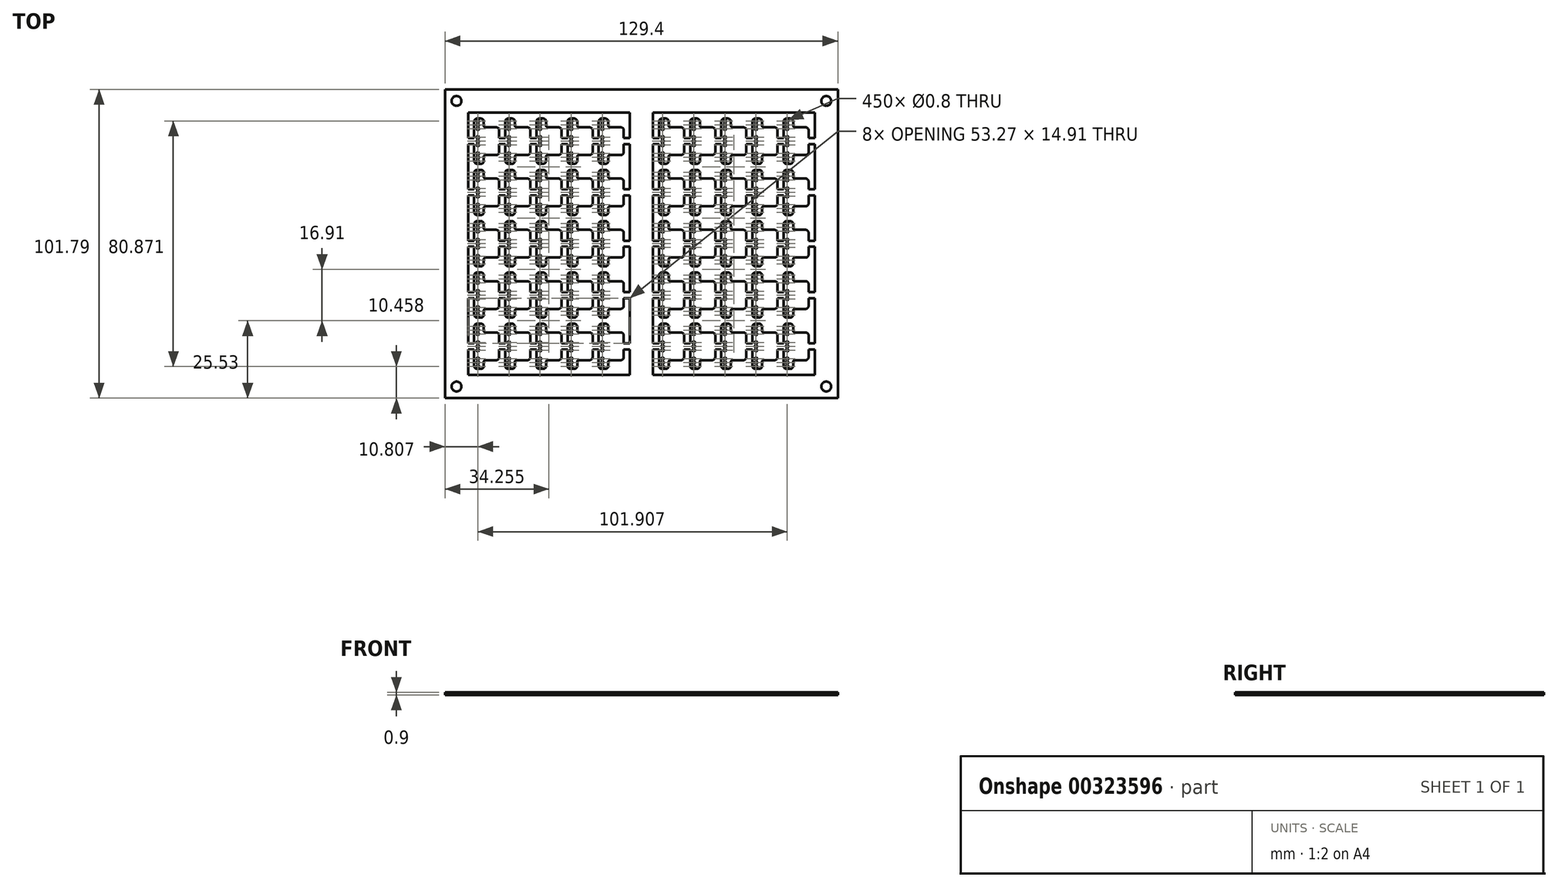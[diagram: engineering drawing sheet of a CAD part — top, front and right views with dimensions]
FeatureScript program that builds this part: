
annotation { "Feature Type Name" : "Feature", "Feature Type Description" : "" }
export const myFeature = defineFeature(function(context is Context, id is Id, definition is map)
    precondition{}
    {
        {
            var Q0;
            Q0=qCreatedBy(makeId("Top.planeOp"),FACE);
            var sketch = newSketch(context, id + "F0", { "sketchPlane" : qUnion([Q0])});
            skLineSegment(sketch, "E0.bottom", {"start": v(0, 0) * mm, "end": v(129.4, 0) * mm});
            skLineSegment(sketch, "E0.top", {"start": v(0, 101.79) * mm, "end": v(129.4, 101.79) * mm});
            skLineSegment(sketch, "E0.left", {"start": v(0, 0) * mm, "end": v(0, 101.79) * mm});
            skLineSegment(sketch, "E0.right", {"start": v(129.4, 0) * mm, "end": v(129.4, 101.79) * mm});
            skCircle(sketch, "E1", {"center": v(3.8, 3.8) * mm, "radius": 1.63 * mm});
            skCircle(sketch, "E2", {"center": v(3.8, 97.98) * mm, "radius": 1.63 * mm});
            skCircle(sketch, "E3", {"center": v(125.6, 97.98) * mm, "radius": 1.63 * mm});
            skCircle(sketch, "E4", {"center": v(125.6, 3.81) * mm, "radius": 1.63 * mm});
            skLineSegment(sketch, "E5.bottom", {"start": v(7.62, 7.62) * mm, "end": v(60.9, 7.62) * mm});
            skLineSegment(sketch, "E5.top", {"start": v(7.62, 94.17) * mm, "end": v(60.9, 94.17) * mm});
            skLineSegment(sketch, "E5.left", {"start": v(7.62, 7.62) * mm, "end": v(7.62, 94.17) * mm});
            skLineSegment(sketch, "E5.right", {"start": v(60.9, 7.62) * mm, "end": v(60.9, 94.17) * mm});
            skLineSegment(sketch, "E6.bottom", {"start": v(68.51, 7.62) * mm, "end": v(121.78, 7.62) * mm});
            skLineSegment(sketch, "E6.top", {"start": v(68.51, 94.17) * mm, "end": v(121.78, 94.17) * mm});
            skLineSegment(sketch, "E6.left", {"start": v(68.51, 7.62) * mm, "end": v(68.51, 94.17) * mm});
            skLineSegment(sketch, "E6.right", {"start": v(121.78, 7.62) * mm, "end": v(121.78, 94.17) * mm});
            skSolve(sketch);
        }
        {
            var Q0;
            Q0 = qSketchRegion(id + "F0", true);
            extrude(context, id + "F1", {"entities" : qUnion([Q0]), "depth" : .9 * mm, "offsetDistance" : 25 * mm});
        }
        {
            var Q0;
            Q0=makeQuery(id+"F1.opExtrude","CAP_FACE",FACE,{"disambiguationData":[OSD([sQuery(id+"F0.wireOp",EDGE,"E0.bottom"),sQuery(id+"F0.wireOp",EDGE,"E0.top"),sQuery(id+"F0.wireOp",EDGE,"E0.left"),sQuery(id+"F0.wireOp",EDGE,"E0.right"),sQuery(id+"F0.wireOp",EDGE,"E1"),sQuery(id+"F0.wireOp",EDGE,"E2"),sQuery(id+"F0.wireOp",EDGE,"E3"),sQuery(id+"F0.wireOp",EDGE,"E4"),sQuery(id+"F0.wireOp",EDGE,"E5.bottom"),sQuery(id+"F0.wireOp",EDGE,"E5.top"),sQuery(id+"F0.wireOp",EDGE,"E5.left"),sQuery(id+"F0.wireOp",EDGE,"E5.right"),sQuery(id+"F0.wireOp",EDGE,"E6.bottom"),sQuery(id+"F0.wireOp",EDGE,"E6.top"),sQuery(id+"F0.wireOp",EDGE,"E6.left"),sQuery(id+"F0.wireOp",EDGE,"E6.right")])],"isStart":false});
            var sketch = newSketch(context, id + "F2", { "sketchPlane" : qUnion([Q0])});
            skLineSegment(sketch, "E7.bottom", {"start": v(10.62, 24.53) * mm, "end": v(11.8, 24.53) * mm});
            skLineSegment(sketch, "E7.top", {"start": v(10.62, 9.62) * mm, "end": v(11.8, 9.62) * mm});
            skLineSegment(sketch, "E7.left", {"start": v(9.62, 23.53) * mm, "end": v(9.62, 18.07) * mm});
            skLineSegment(sketch, "E7.right", {"start": v(12.8, 23.53) * mm, "end": v(12.8, 22.15) * mm});
            skLineSegment(sketch, "E8.bottom", {"start": v(13.3, 21.65) * mm, "end": v(16.87, 21.65) * mm});
            skLineSegment(sketch, "E8.top", {"start": v(13.3, 12.5) * mm, "end": v(16.87, 12.5) * mm});
            skLineSegment(sketch, "E8.right", {"start": v(17.87, 20.65) * mm, "end": v(17.87, 13.5) * mm});
            skLineSegment(sketch, "E9.bottom", {"start": v(9.62, 18.07) * mm, "end": v(7.62, 18.07) * mm});
            skLineSegment(sketch, "E9.top", {"start": v(9.62, 16.07) * mm, "end": v(7.62, 16.07) * mm});
            skLineSegment(sketch, "E9.right", {"start": v(7.62, 18.07) * mm, "end": v(7.62, 16.07) * mm});
            skPoint(sketch, "E10.visualSharp", {"position": v(9.62, 24.53) * mm});
            skArc(sketch, "E10.filletArc", {"start": v(10.62, 24.53) * mm, "mid": v(9.91, 24.24) * mm, "end": v(9.62, 23.53) * mm});
            skPoint(sketch, "E11.visualSharp", {"position": v(12.8, 24.53) * mm});
            skArc(sketch, "E11.filletArc", {"start": v(12.8, 23.53) * mm, "mid": v(12.5, 24.24) * mm, "end": v(11.8, 24.53) * mm});
            skPoint(sketch, "E12.visualSharp", {"position": v(9.62, 9.62) * mm});
            skArc(sketch, "E12.filletArc", {"start": v(9.62, 10.62) * mm, "mid": v(9.91, 9.91) * mm, "end": v(10.62, 9.62) * mm});
            skPoint(sketch, "E13.visualSharp", {"position": v(12.8, 9.62) * mm});
            skArc(sketch, "E13.filletArc", {"start": v(11.8, 9.62) * mm, "mid": v(12.5, 9.91) * mm, "end": v(12.8, 10.62) * mm});
            skPoint(sketch, "E14.visualSharp", {"position": v(17.87, 21.65) * mm});
            skArc(sketch, "E14.filletArc", {"start": v(17.87, 20.65) * mm, "mid": v(17.58, 21.35) * mm, "end": v(16.87, 21.65) * mm});
            skPoint(sketch, "E15.visualSharp", {"position": v(17.87, 12.5) * mm});
            skArc(sketch, "E15.filletArc", {"start": v(16.87, 12.5) * mm, "mid": v(17.58, 12.8) * mm, "end": v(17.87, 13.5) * mm});
            skLineSegment(sketch, "E16.trimOffspring", {"start": v(12.8, 12) * mm, "end": v(12.8, 10.62) * mm});
            skLineSegment(sketch, "E17.trimOffspring", {"start": v(9.62, 16.07) * mm, "end": v(9.62, 10.62) * mm});
            skPoint(sketch, "E18.visualSharp", {"position": v(12.8, 21.65) * mm});
            skArc(sketch, "E18.filletArc", {"start": v(12.8, 22.15) * mm, "mid": v(12.94, 21.8) * mm, "end": v(13.3, 21.65) * mm});
            skPoint(sketch, "E19.visualSharp", {"position": v(12.8, 12.5) * mm});
            skArc(sketch, "E19.filletArc", {"start": v(13.3, 12.5) * mm, "mid": v(12.94, 12.36) * mm, "end": v(12.8, 12) * mm});
            skLineSegment(sketch, "E20.0.1.0", {"start": v(17.87, 37.56) * mm, "end": v(17.87, 30.41) * mm});
            skLineSegment(sketch, "E20.0.1.1", {"start": v(9.62, 34.98) * mm, "end": v(7.62, 34.98) * mm});
            skLineSegment(sketch, "E20.0.1.2", {"start": v(9.62, 40.44) * mm, "end": v(9.62, 34.98) * mm});
            skLineSegment(sketch, "E20.0.1.3", {"start": v(12.8, 40.44) * mm, "end": v(12.8, 39.06) * mm});
            skPoint(sketch, "E20.0.1.4", {"position": v(9.62, 26.53) * mm});
            skPoint(sketch, "E20.0.1.5", {"position": v(12.8, 29.41) * mm});
            skLineSegment(sketch, "E20.0.1.6", {"start": v(13.3, 38.56) * mm, "end": v(16.87, 38.56) * mm});
            skLineSegment(sketch, "E20.0.1.7", {"start": v(12.8, 28.91) * mm, "end": v(12.8, 27.53) * mm});
            skPoint(sketch, "E20.0.1.8", {"position": v(12.8, 41.44) * mm});
            skLineSegment(sketch, "E20.0.1.9", {"start": v(9.62, 32.98) * mm, "end": v(9.62, 27.53) * mm});
            skLineSegment(sketch, "E20.0.1.10", {"start": v(10.62, 41.44) * mm, "end": v(11.8, 41.44) * mm});
            skLineSegment(sketch, "E20.0.1.11", {"start": v(10.62, 26.53) * mm, "end": v(11.8, 26.53) * mm});
            skLineSegment(sketch, "E20.0.1.12", {"start": v(7.62, 34.98) * mm, "end": v(7.62, 32.98) * mm});
            skLineSegment(sketch, "E20.0.1.13", {"start": v(9.62, 32.98) * mm, "end": v(7.62, 32.98) * mm});
            skLineSegment(sketch, "E20.0.1.14", {"start": v(13.3, 29.41) * mm, "end": v(16.87, 29.41) * mm});
            skPoint(sketch, "E20.0.1.15", {"position": v(12.8, 38.56) * mm});
            skPoint(sketch, "E20.0.1.16", {"position": v(12.8, 26.53) * mm});
            skPoint(sketch, "E20.0.1.17", {"position": v(9.62, 41.44) * mm});
            skPoint(sketch, "E20.0.1.18", {"position": v(17.87, 38.56) * mm});
            skPoint(sketch, "E20.0.1.19", {"position": v(17.87, 29.41) * mm});
            skArc(sketch, "E20.0.1.20", {"start": v(10.62, 41.44) * mm, "mid": v(9.91, 41.15) * mm, "end": v(9.62, 40.44) * mm});
            skArc(sketch, "E20.0.1.21", {"start": v(17.87, 37.56) * mm, "mid": v(17.58, 38.26) * mm, "end": v(16.87, 38.56) * mm});
            skArc(sketch, "E20.0.1.22", {"start": v(12.8, 40.44) * mm, "mid": v(12.5, 41.15) * mm, "end": v(11.8, 41.44) * mm});
            skArc(sketch, "E20.0.1.23", {"start": v(9.62, 27.53) * mm, "mid": v(9.91, 26.82) * mm, "end": v(10.62, 26.53) * mm});
            skArc(sketch, "E20.0.1.24", {"start": v(11.8, 26.53) * mm, "mid": v(12.5, 26.82) * mm, "end": v(12.8, 27.53) * mm});
            skArc(sketch, "E20.0.1.25", {"start": v(16.87, 29.41) * mm, "mid": v(17.58, 29.7) * mm, "end": v(17.87, 30.41) * mm});
            skArc(sketch, "E20.0.1.26", {"start": v(13.3, 29.41) * mm, "mid": v(12.94, 29.27) * mm, "end": v(12.8, 28.91) * mm});
            skArc(sketch, "E20.0.1.27", {"start": v(12.8, 39.06) * mm, "mid": v(12.94, 38.7) * mm, "end": v(13.3, 38.56) * mm});
            skLineSegment(sketch, "E20.0.2.0", {"start": v(17.87, 54.47) * mm, "end": v(17.87, 47.32) * mm});
            skLineSegment(sketch, "E20.0.2.1", {"start": v(9.62, 51.9) * mm, "end": v(7.62, 51.9) * mm});
            skLineSegment(sketch, "E20.0.2.2", {"start": v(9.62, 57.35) * mm, "end": v(9.62, 51.9) * mm});
            skLineSegment(sketch, "E20.0.2.3", {"start": v(12.8, 57.35) * mm, "end": v(12.8, 55.97) * mm});
            skPoint(sketch, "E20.0.2.4", {"position": v(9.62, 43.44) * mm});
            skPoint(sketch, "E20.0.2.5", {"position": v(12.8, 46.32) * mm});
            skLineSegment(sketch, "E20.0.2.6", {"start": v(13.3, 55.47) * mm, "end": v(16.87, 55.47) * mm});
            skLineSegment(sketch, "E20.0.2.7", {"start": v(12.8, 45.82) * mm, "end": v(12.8, 44.44) * mm});
            skPoint(sketch, "E20.0.2.8", {"position": v(12.8, 58.35) * mm});
            skLineSegment(sketch, "E20.0.2.9", {"start": v(9.62, 49.9) * mm, "end": v(9.62, 44.44) * mm});
            skLineSegment(sketch, "E20.0.2.10", {"start": v(10.62, 58.35) * mm, "end": v(11.8, 58.35) * mm});
            skLineSegment(sketch, "E20.0.2.11", {"start": v(10.62, 43.44) * mm, "end": v(11.8, 43.44) * mm});
            skLineSegment(sketch, "E20.0.2.12", {"start": v(7.62, 51.9) * mm, "end": v(7.62, 49.9) * mm});
            skLineSegment(sketch, "E20.0.2.13", {"start": v(9.62, 49.9) * mm, "end": v(7.62, 49.9) * mm});
            skLineSegment(sketch, "E20.0.2.14", {"start": v(13.3, 46.32) * mm, "end": v(16.87, 46.32) * mm});
            skPoint(sketch, "E20.0.2.15", {"position": v(12.8, 55.47) * mm});
            skPoint(sketch, "E20.0.2.16", {"position": v(12.8, 43.44) * mm});
            skPoint(sketch, "E20.0.2.17", {"position": v(9.62, 58.35) * mm});
            skPoint(sketch, "E20.0.2.18", {"position": v(17.87, 55.47) * mm});
            skPoint(sketch, "E20.0.2.19", {"position": v(17.87, 46.32) * mm});
            skArc(sketch, "E20.0.2.20", {"start": v(10.62, 58.35) * mm, "mid": v(9.91, 58.06) * mm, "end": v(9.62, 57.35) * mm});
            skArc(sketch, "E20.0.2.21", {"start": v(17.87, 54.47) * mm, "mid": v(17.58, 55.17) * mm, "end": v(16.87, 55.47) * mm});
            skArc(sketch, "E20.0.2.22", {"start": v(12.8, 57.35) * mm, "mid": v(12.5, 58.06) * mm, "end": v(11.8, 58.35) * mm});
            skArc(sketch, "E20.0.2.23", {"start": v(9.62, 44.44) * mm, "mid": v(9.91, 43.73) * mm, "end": v(10.62, 43.44) * mm});
            skArc(sketch, "E20.0.2.24", {"start": v(11.8, 43.44) * mm, "mid": v(12.5, 43.73) * mm, "end": v(12.8, 44.44) * mm});
            skArc(sketch, "E20.0.2.25", {"start": v(16.87, 46.32) * mm, "mid": v(17.58, 46.62) * mm, "end": v(17.87, 47.32) * mm});
            skArc(sketch, "E20.0.2.26", {"start": v(13.3, 46.32) * mm, "mid": v(12.94, 46.18) * mm, "end": v(12.8, 45.82) * mm});
            skArc(sketch, "E20.0.2.27", {"start": v(12.8, 55.97) * mm, "mid": v(12.94, 55.61) * mm, "end": v(13.3, 55.47) * mm});
            skLineSegment(sketch, "E20.0.3.0", {"start": v(17.87, 71.38) * mm, "end": v(17.87, 64.23) * mm});
            skLineSegment(sketch, "E20.0.3.1", {"start": v(9.62, 68.8) * mm, "end": v(7.62, 68.8) * mm});
            skLineSegment(sketch, "E20.0.3.2", {"start": v(9.62, 74.26) * mm, "end": v(9.62, 68.8) * mm});
            skLineSegment(sketch, "E20.0.3.3", {"start": v(12.8, 74.26) * mm, "end": v(12.8, 72.88) * mm});
            skPoint(sketch, "E20.0.3.4", {"position": v(9.62, 60.35) * mm});
            skPoint(sketch, "E20.0.3.5", {"position": v(12.8, 63.23) * mm});
            skLineSegment(sketch, "E20.0.3.6", {"start": v(13.3, 72.38) * mm, "end": v(16.87, 72.38) * mm});
            skLineSegment(sketch, "E20.0.3.7", {"start": v(12.8, 62.73) * mm, "end": v(12.8, 61.35) * mm});
            skPoint(sketch, "E20.0.3.8", {"position": v(12.8, 75.26) * mm});
            skLineSegment(sketch, "E20.0.3.9", {"start": v(9.62, 66.8) * mm, "end": v(9.62, 61.35) * mm});
            skLineSegment(sketch, "E20.0.3.10", {"start": v(10.62, 75.26) * mm, "end": v(11.8, 75.26) * mm});
            skLineSegment(sketch, "E20.0.3.11", {"start": v(10.62, 60.35) * mm, "end": v(11.8, 60.35) * mm});
            skLineSegment(sketch, "E20.0.3.12", {"start": v(7.62, 68.8) * mm, "end": v(7.62, 66.8) * mm});
            skLineSegment(sketch, "E20.0.3.13", {"start": v(9.62, 66.8) * mm, "end": v(7.62, 66.8) * mm});
            skLineSegment(sketch, "E20.0.3.14", {"start": v(13.3, 63.23) * mm, "end": v(16.87, 63.23) * mm});
            skPoint(sketch, "E20.0.3.15", {"position": v(12.8, 72.38) * mm});
            skPoint(sketch, "E20.0.3.16", {"position": v(12.8, 60.35) * mm});
            skPoint(sketch, "E20.0.3.17", {"position": v(9.62, 75.26) * mm});
            skPoint(sketch, "E20.0.3.18", {"position": v(17.87, 72.38) * mm});
            skPoint(sketch, "E20.0.3.19", {"position": v(17.87, 63.23) * mm});
            skArc(sketch, "E20.0.3.20", {"start": v(10.62, 75.26) * mm, "mid": v(9.91, 74.97) * mm, "end": v(9.62, 74.26) * mm});
            skArc(sketch, "E20.0.3.21", {"start": v(17.87, 71.38) * mm, "mid": v(17.58, 72.08) * mm, "end": v(16.87, 72.38) * mm});
            skArc(sketch, "E20.0.3.22", {"start": v(12.8, 74.26) * mm, "mid": v(12.5, 74.97) * mm, "end": v(11.8, 75.26) * mm});
            skArc(sketch, "E20.0.3.23", {"start": v(9.62, 61.35) * mm, "mid": v(9.91, 60.64) * mm, "end": v(10.62, 60.35) * mm});
            skArc(sketch, "E20.0.3.24", {"start": v(11.8, 60.35) * mm, "mid": v(12.5, 60.64) * mm, "end": v(12.8, 61.35) * mm});
            skArc(sketch, "E20.0.3.25", {"start": v(16.87, 63.23) * mm, "mid": v(17.58, 63.53) * mm, "end": v(17.87, 64.23) * mm});
            skArc(sketch, "E20.0.3.26", {"start": v(13.3, 63.23) * mm, "mid": v(12.94, 63.09) * mm, "end": v(12.8, 62.73) * mm});
            skArc(sketch, "E20.0.3.27", {"start": v(12.8, 72.88) * mm, "mid": v(12.94, 72.52) * mm, "end": v(13.3, 72.38) * mm});
            skLineSegment(sketch, "E20.0.4.0", {"start": v(17.87, 88.29) * mm, "end": v(17.87, 81.14) * mm});
            skLineSegment(sketch, "E20.0.4.1", {"start": v(9.62, 85.71) * mm, "end": v(7.62, 85.71) * mm});
            skLineSegment(sketch, "E20.0.4.2", {"start": v(9.62, 91.17) * mm, "end": v(9.62, 85.71) * mm});
            skLineSegment(sketch, "E20.0.4.3", {"start": v(12.8, 91.17) * mm, "end": v(12.8, 89.79) * mm});
            skPoint(sketch, "E20.0.4.4", {"position": v(9.62, 77.26) * mm});
            skPoint(sketch, "E20.0.4.5", {"position": v(12.8, 80.14) * mm});
            skLineSegment(sketch, "E20.0.4.6", {"start": v(13.3, 89.29) * mm, "end": v(16.87, 89.29) * mm});
            skLineSegment(sketch, "E20.0.4.7", {"start": v(12.8, 79.64) * mm, "end": v(12.8, 78.26) * mm});
            skPoint(sketch, "E20.0.4.8", {"position": v(12.8, 92.17) * mm});
            skLineSegment(sketch, "E20.0.4.9", {"start": v(9.62, 83.71) * mm, "end": v(9.62, 78.26) * mm});
            skLineSegment(sketch, "E20.0.4.10", {"start": v(10.62, 92.17) * mm, "end": v(11.8, 92.17) * mm});
            skLineSegment(sketch, "E20.0.4.11", {"start": v(10.62, 77.26) * mm, "end": v(11.8, 77.26) * mm});
            skLineSegment(sketch, "E20.0.4.12", {"start": v(7.62, 85.71) * mm, "end": v(7.62, 83.71) * mm});
            skLineSegment(sketch, "E20.0.4.13", {"start": v(9.62, 83.71) * mm, "end": v(7.62, 83.71) * mm});
            skLineSegment(sketch, "E20.0.4.14", {"start": v(13.3, 80.14) * mm, "end": v(16.87, 80.14) * mm});
            skPoint(sketch, "E20.0.4.15", {"position": v(12.8, 89.29) * mm});
            skPoint(sketch, "E20.0.4.16", {"position": v(12.8, 77.26) * mm});
            skPoint(sketch, "E20.0.4.17", {"position": v(9.62, 92.17) * mm});
            skPoint(sketch, "E20.0.4.18", {"position": v(17.87, 89.29) * mm});
            skPoint(sketch, "E20.0.4.19", {"position": v(17.87, 80.14) * mm});
            skArc(sketch, "E20.0.4.20", {"start": v(10.62, 92.17) * mm, "mid": v(9.91, 91.88) * mm, "end": v(9.62, 91.17) * mm});
            skArc(sketch, "E20.0.4.21", {"start": v(17.87, 88.29) * mm, "mid": v(17.58, 89) * mm, "end": v(16.87, 89.29) * mm});
            skArc(sketch, "E20.0.4.22", {"start": v(12.8, 91.17) * mm, "mid": v(12.5, 91.88) * mm, "end": v(11.8, 92.17) * mm});
            skArc(sketch, "E20.0.4.23", {"start": v(9.62, 78.26) * mm, "mid": v(9.91, 77.55) * mm, "end": v(10.62, 77.26) * mm});
            skArc(sketch, "E20.0.4.24", {"start": v(11.8, 77.26) * mm, "mid": v(12.5, 77.55) * mm, "end": v(12.8, 78.26) * mm});
            skArc(sketch, "E20.0.4.25", {"start": v(16.87, 80.14) * mm, "mid": v(17.58, 80.44) * mm, "end": v(17.87, 81.14) * mm});
            skArc(sketch, "E20.0.4.26", {"start": v(13.3, 80.14) * mm, "mid": v(12.94, 80) * mm, "end": v(12.8, 79.64) * mm});
            skArc(sketch, "E20.0.4.27", {"start": v(12.8, 89.79) * mm, "mid": v(12.94, 89.43) * mm, "end": v(13.3, 89.29) * mm});
            skLineSegment(sketch, "E20.1.0.0", {"start": v(28.13, 20.65) * mm, "end": v(28.13, 13.5) * mm});
            skLineSegment(sketch, "E20.1.0.1", {"start": v(19.87, 18.07) * mm, "end": v(17.87, 18.07) * mm});
            skLineSegment(sketch, "E20.1.0.2", {"start": v(19.87, 23.53) * mm, "end": v(19.87, 18.07) * mm});
            skLineSegment(sketch, "E20.1.0.3", {"start": v(23.05, 23.53) * mm, "end": v(23.05, 22.15) * mm});
            skPoint(sketch, "E20.1.0.4", {"position": v(19.87, 9.62) * mm});
            skPoint(sketch, "E20.1.0.5", {"position": v(23.05, 12.5) * mm});
            skLineSegment(sketch, "E20.1.0.6", {"start": v(23.55, 21.65) * mm, "end": v(27.13, 21.65) * mm});
            skLineSegment(sketch, "E20.1.0.7", {"start": v(23.05, 12) * mm, "end": v(23.05, 10.62) * mm});
            skPoint(sketch, "E20.1.0.8", {"position": v(23.05, 24.53) * mm});
            skLineSegment(sketch, "E20.1.0.9", {"start": v(19.87, 16.07) * mm, "end": v(19.87, 10.62) * mm});
            skLineSegment(sketch, "E20.1.0.10", {"start": v(20.87, 24.53) * mm, "end": v(22.05, 24.53) * mm});
            skLineSegment(sketch, "E20.1.0.11", {"start": v(20.87, 9.62) * mm, "end": v(22.05, 9.62) * mm});
            skLineSegment(sketch, "E20.1.0.12", {"start": v(17.87, 18.07) * mm, "end": v(17.87, 16.07) * mm});
            skLineSegment(sketch, "E20.1.0.13", {"start": v(19.87, 16.07) * mm, "end": v(17.87, 16.07) * mm});
            skLineSegment(sketch, "E20.1.0.14", {"start": v(23.55, 12.5) * mm, "end": v(27.13, 12.5) * mm});
            skPoint(sketch, "E20.1.0.15", {"position": v(23.05, 21.65) * mm});
            skPoint(sketch, "E20.1.0.16", {"position": v(23.05, 9.62) * mm});
            skPoint(sketch, "E20.1.0.17", {"position": v(19.87, 24.53) * mm});
            skPoint(sketch, "E20.1.0.18", {"position": v(28.13, 21.65) * mm});
            skPoint(sketch, "E20.1.0.19", {"position": v(28.13, 12.5) * mm});
            skArc(sketch, "E20.1.0.20", {"start": v(20.87, 24.53) * mm, "mid": v(20.17, 24.24) * mm, "end": v(19.87, 23.53) * mm});
            skArc(sketch, "E20.1.0.21", {"start": v(28.13, 20.65) * mm, "mid": v(27.84, 21.35) * mm, "end": v(27.13, 21.65) * mm});
            skArc(sketch, "E20.1.0.22", {"start": v(23.05, 23.53) * mm, "mid": v(22.76, 24.24) * mm, "end": v(22.05, 24.53) * mm});
            skArc(sketch, "E20.1.0.23", {"start": v(19.87, 10.62) * mm, "mid": v(20.17, 9.91) * mm, "end": v(20.87, 9.62) * mm});
            skArc(sketch, "E20.1.0.24", {"start": v(22.05, 9.62) * mm, "mid": v(22.76, 9.91) * mm, "end": v(23.05, 10.62) * mm});
            skArc(sketch, "E20.1.0.25", {"start": v(27.13, 12.5) * mm, "mid": v(27.84, 12.8) * mm, "end": v(28.13, 13.5) * mm});
            skArc(sketch, "E20.1.0.26", {"start": v(23.55, 12.5) * mm, "mid": v(23.2, 12.36) * mm, "end": v(23.05, 12) * mm});
            skArc(sketch, "E20.1.0.27", {"start": v(23.05, 22.15) * mm, "mid": v(23.2, 21.8) * mm, "end": v(23.55, 21.65) * mm});
            skLineSegment(sketch, "E20.1.1.0", {"start": v(28.13, 37.56) * mm, "end": v(28.13, 30.41) * mm});
            skLineSegment(sketch, "E20.1.1.1", {"start": v(19.87, 34.98) * mm, "end": v(17.87, 34.98) * mm});
            skLineSegment(sketch, "E20.1.1.2", {"start": v(19.87, 40.44) * mm, "end": v(19.87, 34.98) * mm});
            skLineSegment(sketch, "E20.1.1.3", {"start": v(23.05, 40.44) * mm, "end": v(23.05, 39.06) * mm});
            skPoint(sketch, "E20.1.1.4", {"position": v(19.87, 26.53) * mm});
            skPoint(sketch, "E20.1.1.5", {"position": v(23.05, 29.41) * mm});
            skLineSegment(sketch, "E20.1.1.6", {"start": v(23.55, 38.56) * mm, "end": v(27.13, 38.56) * mm});
            skLineSegment(sketch, "E20.1.1.7", {"start": v(23.05, 28.91) * mm, "end": v(23.05, 27.53) * mm});
            skPoint(sketch, "E20.1.1.8", {"position": v(23.05, 41.44) * mm});
            skLineSegment(sketch, "E20.1.1.9", {"start": v(19.87, 32.98) * mm, "end": v(19.87, 27.53) * mm});
            skLineSegment(sketch, "E20.1.1.10", {"start": v(20.87, 41.44) * mm, "end": v(22.05, 41.44) * mm});
            skLineSegment(sketch, "E20.1.1.11", {"start": v(20.87, 26.53) * mm, "end": v(22.05, 26.53) * mm});
            skLineSegment(sketch, "E20.1.1.12", {"start": v(17.87, 34.98) * mm, "end": v(17.87, 32.98) * mm});
            skLineSegment(sketch, "E20.1.1.13", {"start": v(19.87, 32.98) * mm, "end": v(17.87, 32.98) * mm});
            skLineSegment(sketch, "E20.1.1.14", {"start": v(23.55, 29.41) * mm, "end": v(27.13, 29.41) * mm});
            skPoint(sketch, "E20.1.1.15", {"position": v(23.05, 38.56) * mm});
            skPoint(sketch, "E20.1.1.16", {"position": v(23.05, 26.53) * mm});
            skPoint(sketch, "E20.1.1.17", {"position": v(19.87, 41.44) * mm});
            skPoint(sketch, "E20.1.1.18", {"position": v(28.13, 38.56) * mm});
            skPoint(sketch, "E20.1.1.19", {"position": v(28.13, 29.41) * mm});
            skArc(sketch, "E20.1.1.20", {"start": v(20.87, 41.44) * mm, "mid": v(20.17, 41.15) * mm, "end": v(19.87, 40.44) * mm});
            skArc(sketch, "E20.1.1.21", {"start": v(28.13, 37.56) * mm, "mid": v(27.84, 38.26) * mm, "end": v(27.13, 38.56) * mm});
            skArc(sketch, "E20.1.1.22", {"start": v(23.05, 40.44) * mm, "mid": v(22.76, 41.15) * mm, "end": v(22.05, 41.44) * mm});
            skArc(sketch, "E20.1.1.23", {"start": v(19.87, 27.53) * mm, "mid": v(20.17, 26.82) * mm, "end": v(20.87, 26.53) * mm});
            skArc(sketch, "E20.1.1.24", {"start": v(22.05, 26.53) * mm, "mid": v(22.76, 26.82) * mm, "end": v(23.05, 27.53) * mm});
            skArc(sketch, "E20.1.1.25", {"start": v(27.13, 29.41) * mm, "mid": v(27.84, 29.7) * mm, "end": v(28.13, 30.41) * mm});
            skArc(sketch, "E20.1.1.26", {"start": v(23.55, 29.41) * mm, "mid": v(23.2, 29.27) * mm, "end": v(23.05, 28.91) * mm});
            skArc(sketch, "E20.1.1.27", {"start": v(23.05, 39.06) * mm, "mid": v(23.2, 38.7) * mm, "end": v(23.55, 38.56) * mm});
            skLineSegment(sketch, "E20.1.2.0", {"start": v(28.13, 54.47) * mm, "end": v(28.13, 47.32) * mm});
            skLineSegment(sketch, "E20.1.2.1", {"start": v(19.87, 51.9) * mm, "end": v(17.87, 51.9) * mm});
            skLineSegment(sketch, "E20.1.2.2", {"start": v(19.87, 57.35) * mm, "end": v(19.87, 51.9) * mm});
            skLineSegment(sketch, "E20.1.2.3", {"start": v(23.05, 57.35) * mm, "end": v(23.05, 55.97) * mm});
            skPoint(sketch, "E20.1.2.4", {"position": v(19.87, 43.44) * mm});
            skPoint(sketch, "E20.1.2.5", {"position": v(23.05, 46.32) * mm});
            skLineSegment(sketch, "E20.1.2.6", {"start": v(23.55, 55.47) * mm, "end": v(27.13, 55.47) * mm});
            skLineSegment(sketch, "E20.1.2.7", {"start": v(23.05, 45.82) * mm, "end": v(23.05, 44.44) * mm});
            skPoint(sketch, "E20.1.2.8", {"position": v(23.05, 58.35) * mm});
            skLineSegment(sketch, "E20.1.2.9", {"start": v(19.87, 49.9) * mm, "end": v(19.87, 44.44) * mm});
            skLineSegment(sketch, "E20.1.2.10", {"start": v(20.87, 58.35) * mm, "end": v(22.05, 58.35) * mm});
            skLineSegment(sketch, "E20.1.2.11", {"start": v(20.87, 43.44) * mm, "end": v(22.05, 43.44) * mm});
            skLineSegment(sketch, "E20.1.2.12", {"start": v(17.87, 51.9) * mm, "end": v(17.87, 49.9) * mm});
            skLineSegment(sketch, "E20.1.2.13", {"start": v(19.87, 49.9) * mm, "end": v(17.87, 49.9) * mm});
            skLineSegment(sketch, "E20.1.2.14", {"start": v(23.55, 46.32) * mm, "end": v(27.13, 46.32) * mm});
            skPoint(sketch, "E20.1.2.15", {"position": v(23.05, 55.47) * mm});
            skPoint(sketch, "E20.1.2.16", {"position": v(23.05, 43.44) * mm});
            skPoint(sketch, "E20.1.2.17", {"position": v(19.87, 58.35) * mm});
            skPoint(sketch, "E20.1.2.18", {"position": v(28.13, 55.47) * mm});
            skPoint(sketch, "E20.1.2.19", {"position": v(28.13, 46.32) * mm});
            skArc(sketch, "E20.1.2.20", {"start": v(20.87, 58.35) * mm, "mid": v(20.17, 58.06) * mm, "end": v(19.87, 57.35) * mm});
            skArc(sketch, "E20.1.2.21", {"start": v(28.13, 54.47) * mm, "mid": v(27.84, 55.17) * mm, "end": v(27.13, 55.47) * mm});
            skArc(sketch, "E20.1.2.22", {"start": v(23.05, 57.35) * mm, "mid": v(22.76, 58.06) * mm, "end": v(22.05, 58.35) * mm});
            skArc(sketch, "E20.1.2.23", {"start": v(19.87, 44.44) * mm, "mid": v(20.17, 43.73) * mm, "end": v(20.87, 43.44) * mm});
            skArc(sketch, "E20.1.2.24", {"start": v(22.05, 43.44) * mm, "mid": v(22.76, 43.73) * mm, "end": v(23.05, 44.44) * mm});
            skArc(sketch, "E20.1.2.25", {"start": v(27.13, 46.32) * mm, "mid": v(27.84, 46.62) * mm, "end": v(28.13, 47.32) * mm});
            skArc(sketch, "E20.1.2.26", {"start": v(23.55, 46.32) * mm, "mid": v(23.2, 46.18) * mm, "end": v(23.05, 45.82) * mm});
            skArc(sketch, "E20.1.2.27", {"start": v(23.05, 55.97) * mm, "mid": v(23.2, 55.61) * mm, "end": v(23.55, 55.47) * mm});
            skLineSegment(sketch, "E20.1.3.0", {"start": v(28.13, 71.38) * mm, "end": v(28.13, 64.23) * mm});
            skLineSegment(sketch, "E20.1.3.1", {"start": v(19.87, 68.8) * mm, "end": v(17.87, 68.8) * mm});
            skLineSegment(sketch, "E20.1.3.2", {"start": v(19.87, 74.26) * mm, "end": v(19.87, 68.8) * mm});
            skLineSegment(sketch, "E20.1.3.3", {"start": v(23.05, 74.26) * mm, "end": v(23.05, 72.88) * mm});
            skPoint(sketch, "E20.1.3.4", {"position": v(19.87, 60.35) * mm});
            skPoint(sketch, "E20.1.3.5", {"position": v(23.05, 63.23) * mm});
            skLineSegment(sketch, "E20.1.3.6", {"start": v(23.55, 72.38) * mm, "end": v(27.13, 72.38) * mm});
            skLineSegment(sketch, "E20.1.3.7", {"start": v(23.05, 62.73) * mm, "end": v(23.05, 61.35) * mm});
            skPoint(sketch, "E20.1.3.8", {"position": v(23.05, 75.26) * mm});
            skLineSegment(sketch, "E20.1.3.9", {"start": v(19.87, 66.8) * mm, "end": v(19.87, 61.35) * mm});
            skLineSegment(sketch, "E20.1.3.10", {"start": v(20.87, 75.26) * mm, "end": v(22.05, 75.26) * mm});
            skLineSegment(sketch, "E20.1.3.11", {"start": v(20.87, 60.35) * mm, "end": v(22.05, 60.35) * mm});
            skLineSegment(sketch, "E20.1.3.12", {"start": v(17.87, 68.8) * mm, "end": v(17.87, 66.8) * mm});
            skLineSegment(sketch, "E20.1.3.13", {"start": v(19.87, 66.8) * mm, "end": v(17.87, 66.8) * mm});
            skLineSegment(sketch, "E20.1.3.14", {"start": v(23.55, 63.23) * mm, "end": v(27.13, 63.23) * mm});
            skPoint(sketch, "E20.1.3.15", {"position": v(23.05, 72.38) * mm});
            skPoint(sketch, "E20.1.3.16", {"position": v(23.05, 60.35) * mm});
            skPoint(sketch, "E20.1.3.17", {"position": v(19.87, 75.26) * mm});
            skPoint(sketch, "E20.1.3.18", {"position": v(28.13, 72.38) * mm});
            skPoint(sketch, "E20.1.3.19", {"position": v(28.13, 63.23) * mm});
            skArc(sketch, "E20.1.3.20", {"start": v(20.87, 75.26) * mm, "mid": v(20.17, 74.97) * mm, "end": v(19.87, 74.26) * mm});
            skArc(sketch, "E20.1.3.21", {"start": v(28.13, 71.38) * mm, "mid": v(27.84, 72.08) * mm, "end": v(27.13, 72.38) * mm});
            skArc(sketch, "E20.1.3.22", {"start": v(23.05, 74.26) * mm, "mid": v(22.76, 74.97) * mm, "end": v(22.05, 75.26) * mm});
            skArc(sketch, "E20.1.3.23", {"start": v(19.87, 61.35) * mm, "mid": v(20.17, 60.64) * mm, "end": v(20.87, 60.35) * mm});
            skArc(sketch, "E20.1.3.24", {"start": v(22.05, 60.35) * mm, "mid": v(22.76, 60.64) * mm, "end": v(23.05, 61.35) * mm});
            skArc(sketch, "E20.1.3.25", {"start": v(27.13, 63.23) * mm, "mid": v(27.84, 63.53) * mm, "end": v(28.13, 64.23) * mm});
            skArc(sketch, "E20.1.3.26", {"start": v(23.55, 63.23) * mm, "mid": v(23.2, 63.09) * mm, "end": v(23.05, 62.73) * mm});
            skArc(sketch, "E20.1.3.27", {"start": v(23.05, 72.88) * mm, "mid": v(23.2, 72.52) * mm, "end": v(23.55, 72.38) * mm});
            skLineSegment(sketch, "E20.1.4.0", {"start": v(28.13, 88.29) * mm, "end": v(28.13, 81.14) * mm});
            skLineSegment(sketch, "E20.1.4.1", {"start": v(19.87, 85.71) * mm, "end": v(17.87, 85.71) * mm});
            skLineSegment(sketch, "E20.1.4.2", {"start": v(19.87, 91.17) * mm, "end": v(19.87, 85.71) * mm});
            skLineSegment(sketch, "E20.1.4.3", {"start": v(23.05, 91.17) * mm, "end": v(23.05, 89.79) * mm});
            skPoint(sketch, "E20.1.4.4", {"position": v(19.87, 77.26) * mm});
            skPoint(sketch, "E20.1.4.5", {"position": v(23.05, 80.14) * mm});
            skLineSegment(sketch, "E20.1.4.6", {"start": v(23.55, 89.29) * mm, "end": v(27.13, 89.29) * mm});
            skLineSegment(sketch, "E20.1.4.7", {"start": v(23.05, 79.64) * mm, "end": v(23.05, 78.26) * mm});
            skPoint(sketch, "E20.1.4.8", {"position": v(23.05, 92.17) * mm});
            skLineSegment(sketch, "E20.1.4.9", {"start": v(19.87, 83.71) * mm, "end": v(19.87, 78.26) * mm});
            skLineSegment(sketch, "E20.1.4.10", {"start": v(20.87, 92.17) * mm, "end": v(22.05, 92.17) * mm});
            skLineSegment(sketch, "E20.1.4.11", {"start": v(20.87, 77.26) * mm, "end": v(22.05, 77.26) * mm});
            skLineSegment(sketch, "E20.1.4.12", {"start": v(17.87, 85.71) * mm, "end": v(17.87, 83.71) * mm});
            skLineSegment(sketch, "E20.1.4.13", {"start": v(19.87, 83.71) * mm, "end": v(17.87, 83.71) * mm});
            skLineSegment(sketch, "E20.1.4.14", {"start": v(23.55, 80.14) * mm, "end": v(27.13, 80.14) * mm});
            skPoint(sketch, "E20.1.4.15", {"position": v(23.05, 89.29) * mm});
            skPoint(sketch, "E20.1.4.16", {"position": v(23.05, 77.26) * mm});
            skPoint(sketch, "E20.1.4.17", {"position": v(19.87, 92.17) * mm});
            skPoint(sketch, "E20.1.4.18", {"position": v(28.13, 89.29) * mm});
            skPoint(sketch, "E20.1.4.19", {"position": v(28.13, 80.14) * mm});
            skArc(sketch, "E20.1.4.20", {"start": v(20.87, 92.17) * mm, "mid": v(20.17, 91.88) * mm, "end": v(19.87, 91.17) * mm});
            skArc(sketch, "E20.1.4.21", {"start": v(28.13, 88.29) * mm, "mid": v(27.84, 89) * mm, "end": v(27.13, 89.29) * mm});
            skArc(sketch, "E20.1.4.22", {"start": v(23.05, 91.17) * mm, "mid": v(22.76, 91.88) * mm, "end": v(22.05, 92.17) * mm});
            skArc(sketch, "E20.1.4.23", {"start": v(19.87, 78.26) * mm, "mid": v(20.17, 77.55) * mm, "end": v(20.87, 77.26) * mm});
            skArc(sketch, "E20.1.4.24", {"start": v(22.05, 77.26) * mm, "mid": v(22.76, 77.55) * mm, "end": v(23.05, 78.26) * mm});
            skArc(sketch, "E20.1.4.25", {"start": v(27.13, 80.14) * mm, "mid": v(27.84, 80.44) * mm, "end": v(28.13, 81.14) * mm});
            skArc(sketch, "E20.1.4.26", {"start": v(23.55, 80.14) * mm, "mid": v(23.2, 80) * mm, "end": v(23.05, 79.64) * mm});
            skArc(sketch, "E20.1.4.27", {"start": v(23.05, 89.79) * mm, "mid": v(23.2, 89.43) * mm, "end": v(23.55, 89.29) * mm});
            skLineSegment(sketch, "E20.2.0.0", {"start": v(38.38, 20.65) * mm, "end": v(38.38, 13.5) * mm});
            skLineSegment(sketch, "E20.2.0.1", {"start": v(30.13, 18.07) * mm, "end": v(28.13, 18.07) * mm});
            skLineSegment(sketch, "E20.2.0.2", {"start": v(30.13, 23.53) * mm, "end": v(30.13, 18.07) * mm});
            skLineSegment(sketch, "E20.2.0.3", {"start": v(33.3, 23.53) * mm, "end": v(33.3, 22.15) * mm});
            skPoint(sketch, "E20.2.0.4", {"position": v(30.13, 9.62) * mm});
            skPoint(sketch, "E20.2.0.5", {"position": v(33.3, 12.5) * mm});
            skLineSegment(sketch, "E20.2.0.6", {"start": v(33.8, 21.65) * mm, "end": v(37.38, 21.65) * mm});
            skLineSegment(sketch, "E20.2.0.7", {"start": v(33.3, 12) * mm, "end": v(33.3, 10.62) * mm});
            skPoint(sketch, "E20.2.0.8", {"position": v(33.3, 24.53) * mm});
            skLineSegment(sketch, "E20.2.0.9", {"start": v(30.13, 16.07) * mm, "end": v(30.13, 10.62) * mm});
            skLineSegment(sketch, "E20.2.0.10", {"start": v(31.13, 24.53) * mm, "end": v(32.3, 24.53) * mm});
            skLineSegment(sketch, "E20.2.0.11", {"start": v(31.13, 9.62) * mm, "end": v(32.3, 9.62) * mm});
            skLineSegment(sketch, "E20.2.0.12", {"start": v(28.13, 18.07) * mm, "end": v(28.13, 16.07) * mm});
            skLineSegment(sketch, "E20.2.0.13", {"start": v(30.13, 16.07) * mm, "end": v(28.13, 16.07) * mm});
            skLineSegment(sketch, "E20.2.0.14", {"start": v(33.8, 12.5) * mm, "end": v(37.38, 12.5) * mm});
            skPoint(sketch, "E20.2.0.15", {"position": v(33.3, 21.65) * mm});
            skPoint(sketch, "E20.2.0.16", {"position": v(33.3, 9.62) * mm});
            skPoint(sketch, "E20.2.0.17", {"position": v(30.13, 24.53) * mm});
            skPoint(sketch, "E20.2.0.18", {"position": v(38.38, 21.65) * mm});
            skPoint(sketch, "E20.2.0.19", {"position": v(38.38, 12.5) * mm});
            skArc(sketch, "E20.2.0.20", {"start": v(31.13, 24.53) * mm, "mid": v(30.42, 24.24) * mm, "end": v(30.13, 23.53) * mm});
            skArc(sketch, "E20.2.0.21", {"start": v(38.38, 20.65) * mm, "mid": v(38.09, 21.35) * mm, "end": v(37.38, 21.65) * mm});
            skArc(sketch, "E20.2.0.22", {"start": v(33.3, 23.53) * mm, "mid": v(33, 24.24) * mm, "end": v(32.3, 24.53) * mm});
            skArc(sketch, "E20.2.0.23", {"start": v(30.13, 10.62) * mm, "mid": v(30.42, 9.91) * mm, "end": v(31.13, 9.62) * mm});
            skArc(sketch, "E20.2.0.24", {"start": v(32.3, 9.62) * mm, "mid": v(33, 9.91) * mm, "end": v(33.3, 10.62) * mm});
            skArc(sketch, "E20.2.0.25", {"start": v(37.38, 12.5) * mm, "mid": v(38.09, 12.8) * mm, "end": v(38.38, 13.5) * mm});
            skArc(sketch, "E20.2.0.26", {"start": v(33.8, 12.5) * mm, "mid": v(33.45, 12.36) * mm, "end": v(33.3, 12) * mm});
            skArc(sketch, "E20.2.0.27", {"start": v(33.3, 22.15) * mm, "mid": v(33.45, 21.8) * mm, "end": v(33.8, 21.65) * mm});
            skLineSegment(sketch, "E20.2.1.0", {"start": v(38.38, 37.56) * mm, "end": v(38.38, 30.41) * mm});
            skLineSegment(sketch, "E20.2.1.1", {"start": v(30.13, 34.98) * mm, "end": v(28.13, 34.98) * mm});
            skLineSegment(sketch, "E20.2.1.2", {"start": v(30.13, 40.44) * mm, "end": v(30.13, 34.98) * mm});
            skLineSegment(sketch, "E20.2.1.3", {"start": v(33.3, 40.44) * mm, "end": v(33.3, 39.06) * mm});
            skPoint(sketch, "E20.2.1.4", {"position": v(30.13, 26.53) * mm});
            skPoint(sketch, "E20.2.1.5", {"position": v(33.3, 29.41) * mm});
            skLineSegment(sketch, "E20.2.1.6", {"start": v(33.8, 38.56) * mm, "end": v(37.38, 38.56) * mm});
            skLineSegment(sketch, "E20.2.1.7", {"start": v(33.3, 28.91) * mm, "end": v(33.3, 27.53) * mm});
            skPoint(sketch, "E20.2.1.8", {"position": v(33.3, 41.44) * mm});
            skLineSegment(sketch, "E20.2.1.9", {"start": v(30.13, 32.98) * mm, "end": v(30.13, 27.53) * mm});
            skLineSegment(sketch, "E20.2.1.10", {"start": v(31.13, 41.44) * mm, "end": v(32.3, 41.44) * mm});
            skLineSegment(sketch, "E20.2.1.11", {"start": v(31.13, 26.53) * mm, "end": v(32.3, 26.53) * mm});
            skLineSegment(sketch, "E20.2.1.12", {"start": v(28.13, 34.98) * mm, "end": v(28.13, 32.98) * mm});
            skLineSegment(sketch, "E20.2.1.13", {"start": v(30.13, 32.98) * mm, "end": v(28.13, 32.98) * mm});
            skLineSegment(sketch, "E20.2.1.14", {"start": v(33.8, 29.41) * mm, "end": v(37.38, 29.41) * mm});
            skPoint(sketch, "E20.2.1.15", {"position": v(33.3, 38.56) * mm});
            skPoint(sketch, "E20.2.1.16", {"position": v(33.3, 26.53) * mm});
            skPoint(sketch, "E20.2.1.17", {"position": v(30.13, 41.44) * mm});
            skPoint(sketch, "E20.2.1.18", {"position": v(38.38, 38.56) * mm});
            skPoint(sketch, "E20.2.1.19", {"position": v(38.38, 29.41) * mm});
            skArc(sketch, "E20.2.1.20", {"start": v(31.13, 41.44) * mm, "mid": v(30.42, 41.15) * mm, "end": v(30.13, 40.44) * mm});
            skArc(sketch, "E20.2.1.21", {"start": v(38.38, 37.56) * mm, "mid": v(38.09, 38.26) * mm, "end": v(37.38, 38.56) * mm});
            skArc(sketch, "E20.2.1.22", {"start": v(33.3, 40.44) * mm, "mid": v(33, 41.15) * mm, "end": v(32.3, 41.44) * mm});
            skArc(sketch, "E20.2.1.23", {"start": v(30.13, 27.53) * mm, "mid": v(30.42, 26.82) * mm, "end": v(31.13, 26.53) * mm});
            skArc(sketch, "E20.2.1.24", {"start": v(32.3, 26.53) * mm, "mid": v(33, 26.82) * mm, "end": v(33.3, 27.53) * mm});
            skArc(sketch, "E20.2.1.25", {"start": v(37.38, 29.41) * mm, "mid": v(38.09, 29.7) * mm, "end": v(38.38, 30.41) * mm});
            skArc(sketch, "E20.2.1.26", {"start": v(33.8, 29.41) * mm, "mid": v(33.45, 29.27) * mm, "end": v(33.3, 28.91) * mm});
            skArc(sketch, "E20.2.1.27", {"start": v(33.3, 39.06) * mm, "mid": v(33.45, 38.7) * mm, "end": v(33.8, 38.56) * mm});
            skLineSegment(sketch, "E20.2.2.0", {"start": v(38.38, 54.47) * mm, "end": v(38.38, 47.32) * mm});
            skLineSegment(sketch, "E20.2.2.1", {"start": v(30.13, 51.9) * mm, "end": v(28.13, 51.9) * mm});
            skLineSegment(sketch, "E20.2.2.2", {"start": v(30.13, 57.35) * mm, "end": v(30.13, 51.9) * mm});
            skLineSegment(sketch, "E20.2.2.3", {"start": v(33.3, 57.35) * mm, "end": v(33.3, 55.97) * mm});
            skPoint(sketch, "E20.2.2.4", {"position": v(30.13, 43.44) * mm});
            skPoint(sketch, "E20.2.2.5", {"position": v(33.3, 46.32) * mm});
            skLineSegment(sketch, "E20.2.2.6", {"start": v(33.8, 55.47) * mm, "end": v(37.38, 55.47) * mm});
            skLineSegment(sketch, "E20.2.2.7", {"start": v(33.3, 45.82) * mm, "end": v(33.3, 44.44) * mm});
            skPoint(sketch, "E20.2.2.8", {"position": v(33.3, 58.35) * mm});
            skLineSegment(sketch, "E20.2.2.9", {"start": v(30.13, 49.9) * mm, "end": v(30.13, 44.44) * mm});
            skLineSegment(sketch, "E20.2.2.10", {"start": v(31.13, 58.35) * mm, "end": v(32.3, 58.35) * mm});
            skLineSegment(sketch, "E20.2.2.11", {"start": v(31.13, 43.44) * mm, "end": v(32.3, 43.44) * mm});
            skLineSegment(sketch, "E20.2.2.12", {"start": v(28.13, 51.9) * mm, "end": v(28.13, 49.9) * mm});
            skLineSegment(sketch, "E20.2.2.13", {"start": v(30.13, 49.9) * mm, "end": v(28.13, 49.9) * mm});
            skLineSegment(sketch, "E20.2.2.14", {"start": v(33.8, 46.32) * mm, "end": v(37.38, 46.32) * mm});
            skPoint(sketch, "E20.2.2.15", {"position": v(33.3, 55.47) * mm});
            skPoint(sketch, "E20.2.2.16", {"position": v(33.3, 43.44) * mm});
            skPoint(sketch, "E20.2.2.17", {"position": v(30.13, 58.35) * mm});
            skPoint(sketch, "E20.2.2.18", {"position": v(38.38, 55.47) * mm});
            skPoint(sketch, "E20.2.2.19", {"position": v(38.38, 46.32) * mm});
            skArc(sketch, "E20.2.2.20", {"start": v(31.13, 58.35) * mm, "mid": v(30.42, 58.06) * mm, "end": v(30.13, 57.35) * mm});
            skArc(sketch, "E20.2.2.21", {"start": v(38.38, 54.47) * mm, "mid": v(38.09, 55.17) * mm, "end": v(37.38, 55.47) * mm});
            skArc(sketch, "E20.2.2.22", {"start": v(33.3, 57.35) * mm, "mid": v(33, 58.06) * mm, "end": v(32.3, 58.35) * mm});
            skArc(sketch, "E20.2.2.23", {"start": v(30.13, 44.44) * mm, "mid": v(30.42, 43.73) * mm, "end": v(31.13, 43.44) * mm});
            skArc(sketch, "E20.2.2.24", {"start": v(32.3, 43.44) * mm, "mid": v(33, 43.73) * mm, "end": v(33.3, 44.44) * mm});
            skArc(sketch, "E20.2.2.25", {"start": v(37.38, 46.32) * mm, "mid": v(38.09, 46.62) * mm, "end": v(38.38, 47.32) * mm});
            skArc(sketch, "E20.2.2.26", {"start": v(33.8, 46.32) * mm, "mid": v(33.45, 46.18) * mm, "end": v(33.3, 45.82) * mm});
            skArc(sketch, "E20.2.2.27", {"start": v(33.3, 55.97) * mm, "mid": v(33.45, 55.61) * mm, "end": v(33.8, 55.47) * mm});
            skLineSegment(sketch, "E20.2.3.0", {"start": v(38.38, 71.38) * mm, "end": v(38.38, 64.23) * mm});
            skLineSegment(sketch, "E20.2.3.1", {"start": v(30.13, 68.8) * mm, "end": v(28.13, 68.8) * mm});
            skLineSegment(sketch, "E20.2.3.2", {"start": v(30.13, 74.26) * mm, "end": v(30.13, 68.8) * mm});
            skLineSegment(sketch, "E20.2.3.3", {"start": v(33.3, 74.26) * mm, "end": v(33.3, 72.88) * mm});
            skPoint(sketch, "E20.2.3.4", {"position": v(30.13, 60.35) * mm});
            skPoint(sketch, "E20.2.3.5", {"position": v(33.3, 63.23) * mm});
            skLineSegment(sketch, "E20.2.3.6", {"start": v(33.8, 72.38) * mm, "end": v(37.38, 72.38) * mm});
            skLineSegment(sketch, "E20.2.3.7", {"start": v(33.3, 62.73) * mm, "end": v(33.3, 61.35) * mm});
            skPoint(sketch, "E20.2.3.8", {"position": v(33.3, 75.26) * mm});
            skLineSegment(sketch, "E20.2.3.9", {"start": v(30.13, 66.8) * mm, "end": v(30.13, 61.35) * mm});
            skLineSegment(sketch, "E20.2.3.10", {"start": v(31.13, 75.26) * mm, "end": v(32.3, 75.26) * mm});
            skLineSegment(sketch, "E20.2.3.11", {"start": v(31.13, 60.35) * mm, "end": v(32.3, 60.35) * mm});
            skLineSegment(sketch, "E20.2.3.12", {"start": v(28.13, 68.8) * mm, "end": v(28.13, 66.8) * mm});
            skLineSegment(sketch, "E20.2.3.13", {"start": v(30.13, 66.8) * mm, "end": v(28.13, 66.8) * mm});
            skLineSegment(sketch, "E20.2.3.14", {"start": v(33.8, 63.23) * mm, "end": v(37.38, 63.23) * mm});
            skPoint(sketch, "E20.2.3.15", {"position": v(33.3, 72.38) * mm});
            skPoint(sketch, "E20.2.3.16", {"position": v(33.3, 60.35) * mm});
            skPoint(sketch, "E20.2.3.17", {"position": v(30.13, 75.26) * mm});
            skPoint(sketch, "E20.2.3.18", {"position": v(38.38, 72.38) * mm});
            skPoint(sketch, "E20.2.3.19", {"position": v(38.38, 63.23) * mm});
            skArc(sketch, "E20.2.3.20", {"start": v(31.13, 75.26) * mm, "mid": v(30.42, 74.97) * mm, "end": v(30.13, 74.26) * mm});
            skArc(sketch, "E20.2.3.21", {"start": v(38.38, 71.38) * mm, "mid": v(38.09, 72.08) * mm, "end": v(37.38, 72.38) * mm});
            skArc(sketch, "E20.2.3.22", {"start": v(33.3, 74.26) * mm, "mid": v(33, 74.97) * mm, "end": v(32.3, 75.26) * mm});
            skArc(sketch, "E20.2.3.23", {"start": v(30.13, 61.35) * mm, "mid": v(30.42, 60.64) * mm, "end": v(31.13, 60.35) * mm});
            skArc(sketch, "E20.2.3.24", {"start": v(32.3, 60.35) * mm, "mid": v(33, 60.64) * mm, "end": v(33.3, 61.35) * mm});
            skArc(sketch, "E20.2.3.25", {"start": v(37.38, 63.23) * mm, "mid": v(38.09, 63.53) * mm, "end": v(38.38, 64.23) * mm});
            skArc(sketch, "E20.2.3.26", {"start": v(33.8, 63.23) * mm, "mid": v(33.45, 63.09) * mm, "end": v(33.3, 62.73) * mm});
            skArc(sketch, "E20.2.3.27", {"start": v(33.3, 72.88) * mm, "mid": v(33.45, 72.52) * mm, "end": v(33.8, 72.38) * mm});
            skLineSegment(sketch, "E20.2.4.0", {"start": v(38.38, 88.29) * mm, "end": v(38.38, 81.14) * mm});
            skLineSegment(sketch, "E20.2.4.1", {"start": v(30.13, 85.71) * mm, "end": v(28.13, 85.71) * mm});
            skLineSegment(sketch, "E20.2.4.2", {"start": v(30.13, 91.17) * mm, "end": v(30.13, 85.71) * mm});
            skLineSegment(sketch, "E20.2.4.3", {"start": v(33.3, 91.17) * mm, "end": v(33.3, 89.79) * mm});
            skPoint(sketch, "E20.2.4.4", {"position": v(30.13, 77.26) * mm});
            skPoint(sketch, "E20.2.4.5", {"position": v(33.3, 80.14) * mm});
            skLineSegment(sketch, "E20.2.4.6", {"start": v(33.8, 89.29) * mm, "end": v(37.38, 89.29) * mm});
            skLineSegment(sketch, "E20.2.4.7", {"start": v(33.3, 79.64) * mm, "end": v(33.3, 78.26) * mm});
            skPoint(sketch, "E20.2.4.8", {"position": v(33.3, 92.17) * mm});
            skLineSegment(sketch, "E20.2.4.9", {"start": v(30.13, 83.71) * mm, "end": v(30.13, 78.26) * mm});
            skLineSegment(sketch, "E20.2.4.10", {"start": v(31.13, 92.17) * mm, "end": v(32.3, 92.17) * mm});
            skLineSegment(sketch, "E20.2.4.11", {"start": v(31.13, 77.26) * mm, "end": v(32.3, 77.26) * mm});
            skLineSegment(sketch, "E20.2.4.12", {"start": v(28.13, 85.71) * mm, "end": v(28.13, 83.71) * mm});
            skLineSegment(sketch, "E20.2.4.13", {"start": v(30.13, 83.71) * mm, "end": v(28.13, 83.71) * mm});
            skLineSegment(sketch, "E20.2.4.14", {"start": v(33.8, 80.14) * mm, "end": v(37.38, 80.14) * mm});
            skPoint(sketch, "E20.2.4.15", {"position": v(33.3, 89.29) * mm});
            skPoint(sketch, "E20.2.4.16", {"position": v(33.3, 77.26) * mm});
            skPoint(sketch, "E20.2.4.17", {"position": v(30.13, 92.17) * mm});
            skPoint(sketch, "E20.2.4.18", {"position": v(38.38, 89.29) * mm});
            skPoint(sketch, "E20.2.4.19", {"position": v(38.38, 80.14) * mm});
            skArc(sketch, "E20.2.4.20", {"start": v(31.13, 92.17) * mm, "mid": v(30.42, 91.88) * mm, "end": v(30.13, 91.17) * mm});
            skArc(sketch, "E20.2.4.21", {"start": v(38.38, 88.29) * mm, "mid": v(38.09, 89) * mm, "end": v(37.38, 89.29) * mm});
            skArc(sketch, "E20.2.4.22", {"start": v(33.3, 91.17) * mm, "mid": v(33, 91.88) * mm, "end": v(32.3, 92.17) * mm});
            skArc(sketch, "E20.2.4.23", {"start": v(30.13, 78.26) * mm, "mid": v(30.42, 77.55) * mm, "end": v(31.13, 77.26) * mm});
            skArc(sketch, "E20.2.4.24", {"start": v(32.3, 77.26) * mm, "mid": v(33, 77.55) * mm, "end": v(33.3, 78.26) * mm});
            skArc(sketch, "E20.2.4.25", {"start": v(37.38, 80.14) * mm, "mid": v(38.09, 80.44) * mm, "end": v(38.38, 81.14) * mm});
            skArc(sketch, "E20.2.4.26", {"start": v(33.8, 80.14) * mm, "mid": v(33.45, 80) * mm, "end": v(33.3, 79.64) * mm});
            skArc(sketch, "E20.2.4.27", {"start": v(33.3, 89.79) * mm, "mid": v(33.45, 89.43) * mm, "end": v(33.8, 89.29) * mm});
            skLineSegment(sketch, "E20.3.0.0", {"start": v(48.64, 20.65) * mm, "end": v(48.64, 13.5) * mm});
            skLineSegment(sketch, "E20.3.0.1", {"start": v(40.38, 18.07) * mm, "end": v(38.38, 18.07) * mm});
            skLineSegment(sketch, "E20.3.0.2", {"start": v(40.38, 23.53) * mm, "end": v(40.38, 18.07) * mm});
            skLineSegment(sketch, "E20.3.0.3", {"start": v(43.56, 23.53) * mm, "end": v(43.56, 22.15) * mm});
            skPoint(sketch, "E20.3.0.4", {"position": v(40.38, 9.62) * mm});
            skPoint(sketch, "E20.3.0.5", {"position": v(43.56, 12.5) * mm});
            skLineSegment(sketch, "E20.3.0.6", {"start": v(44.06, 21.65) * mm, "end": v(47.64, 21.65) * mm});
            skLineSegment(sketch, "E20.3.0.7", {"start": v(43.56, 12) * mm, "end": v(43.56, 10.62) * mm});
            skPoint(sketch, "E20.3.0.8", {"position": v(43.56, 24.53) * mm});
            skLineSegment(sketch, "E20.3.0.9", {"start": v(40.38, 16.07) * mm, "end": v(40.38, 10.62) * mm});
            skLineSegment(sketch, "E20.3.0.10", {"start": v(41.38, 24.53) * mm, "end": v(42.56, 24.53) * mm});
            skLineSegment(sketch, "E20.3.0.11", {"start": v(41.38, 9.62) * mm, "end": v(42.56, 9.62) * mm});
            skLineSegment(sketch, "E20.3.0.12", {"start": v(38.38, 18.07) * mm, "end": v(38.38, 16.07) * mm});
            skLineSegment(sketch, "E20.3.0.13", {"start": v(40.38, 16.07) * mm, "end": v(38.38, 16.07) * mm});
            skLineSegment(sketch, "E20.3.0.14", {"start": v(44.06, 12.5) * mm, "end": v(47.64, 12.5) * mm});
            skPoint(sketch, "E20.3.0.15", {"position": v(43.56, 21.65) * mm});
            skPoint(sketch, "E20.3.0.16", {"position": v(43.56, 9.62) * mm});
            skPoint(sketch, "E20.3.0.17", {"position": v(40.38, 24.53) * mm});
            skPoint(sketch, "E20.3.0.18", {"position": v(48.64, 21.65) * mm});
            skPoint(sketch, "E20.3.0.19", {"position": v(48.64, 12.5) * mm});
            skArc(sketch, "E20.3.0.20", {"start": v(41.38, 24.53) * mm, "mid": v(40.67, 24.24) * mm, "end": v(40.38, 23.53) * mm});
            skArc(sketch, "E20.3.0.21", {"start": v(48.64, 20.65) * mm, "mid": v(48.34, 21.35) * mm, "end": v(47.64, 21.65) * mm});
            skArc(sketch, "E20.3.0.22", {"start": v(43.56, 23.53) * mm, "mid": v(43.26, 24.24) * mm, "end": v(42.56, 24.53) * mm});
            skArc(sketch, "E20.3.0.23", {"start": v(40.38, 10.62) * mm, "mid": v(40.67, 9.91) * mm, "end": v(41.38, 9.62) * mm});
            skArc(sketch, "E20.3.0.24", {"start": v(42.56, 9.62) * mm, "mid": v(43.26, 9.91) * mm, "end": v(43.56, 10.62) * mm});
            skArc(sketch, "E20.3.0.25", {"start": v(47.64, 12.5) * mm, "mid": v(48.34, 12.8) * mm, "end": v(48.64, 13.5) * mm});
            skArc(sketch, "E20.3.0.26", {"start": v(44.06, 12.5) * mm, "mid": v(43.7, 12.36) * mm, "end": v(43.56, 12) * mm});
            skArc(sketch, "E20.3.0.27", {"start": v(43.56, 22.15) * mm, "mid": v(43.7, 21.8) * mm, "end": v(44.06, 21.65) * mm});
            skLineSegment(sketch, "E20.3.1.0", {"start": v(48.64, 37.56) * mm, "end": v(48.64, 30.41) * mm});
            skLineSegment(sketch, "E20.3.1.1", {"start": v(40.38, 34.98) * mm, "end": v(38.38, 34.98) * mm});
            skLineSegment(sketch, "E20.3.1.2", {"start": v(40.38, 40.44) * mm, "end": v(40.38, 34.98) * mm});
            skLineSegment(sketch, "E20.3.1.3", {"start": v(43.56, 40.44) * mm, "end": v(43.56, 39.06) * mm});
            skPoint(sketch, "E20.3.1.4", {"position": v(40.38, 26.53) * mm});
            skPoint(sketch, "E20.3.1.5", {"position": v(43.56, 29.41) * mm});
            skLineSegment(sketch, "E20.3.1.6", {"start": v(44.06, 38.56) * mm, "end": v(47.64, 38.56) * mm});
            skLineSegment(sketch, "E20.3.1.7", {"start": v(43.56, 28.91) * mm, "end": v(43.56, 27.53) * mm});
            skPoint(sketch, "E20.3.1.8", {"position": v(43.56, 41.44) * mm});
            skLineSegment(sketch, "E20.3.1.9", {"start": v(40.38, 32.98) * mm, "end": v(40.38, 27.53) * mm});
            skLineSegment(sketch, "E20.3.1.10", {"start": v(41.38, 41.44) * mm, "end": v(42.56, 41.44) * mm});
            skLineSegment(sketch, "E20.3.1.11", {"start": v(41.38, 26.53) * mm, "end": v(42.56, 26.53) * mm});
            skLineSegment(sketch, "E20.3.1.12", {"start": v(38.38, 34.98) * mm, "end": v(38.38, 32.98) * mm});
            skLineSegment(sketch, "E20.3.1.13", {"start": v(40.38, 32.98) * mm, "end": v(38.38, 32.98) * mm});
            skLineSegment(sketch, "E20.3.1.14", {"start": v(44.06, 29.41) * mm, "end": v(47.64, 29.41) * mm});
            skPoint(sketch, "E20.3.1.15", {"position": v(43.56, 38.56) * mm});
            skPoint(sketch, "E20.3.1.16", {"position": v(43.56, 26.53) * mm});
            skPoint(sketch, "E20.3.1.17", {"position": v(40.38, 41.44) * mm});
            skPoint(sketch, "E20.3.1.18", {"position": v(48.64, 38.56) * mm});
            skPoint(sketch, "E20.3.1.19", {"position": v(48.64, 29.41) * mm});
            skArc(sketch, "E20.3.1.20", {"start": v(41.38, 41.44) * mm, "mid": v(40.67, 41.15) * mm, "end": v(40.38, 40.44) * mm});
            skArc(sketch, "E20.3.1.21", {"start": v(48.64, 37.56) * mm, "mid": v(48.34, 38.26) * mm, "end": v(47.64, 38.56) * mm});
            skArc(sketch, "E20.3.1.22", {"start": v(43.56, 40.44) * mm, "mid": v(43.26, 41.15) * mm, "end": v(42.56, 41.44) * mm});
            skArc(sketch, "E20.3.1.23", {"start": v(40.38, 27.53) * mm, "mid": v(40.67, 26.82) * mm, "end": v(41.38, 26.53) * mm});
            skArc(sketch, "E20.3.1.24", {"start": v(42.56, 26.53) * mm, "mid": v(43.26, 26.82) * mm, "end": v(43.56, 27.53) * mm});
            skArc(sketch, "E20.3.1.25", {"start": v(47.64, 29.41) * mm, "mid": v(48.34, 29.7) * mm, "end": v(48.64, 30.41) * mm});
            skArc(sketch, "E20.3.1.26", {"start": v(44.06, 29.41) * mm, "mid": v(43.7, 29.27) * mm, "end": v(43.56, 28.91) * mm});
            skArc(sketch, "E20.3.1.27", {"start": v(43.56, 39.06) * mm, "mid": v(43.7, 38.7) * mm, "end": v(44.06, 38.56) * mm});
            skLineSegment(sketch, "E20.3.2.0", {"start": v(48.64, 54.47) * mm, "end": v(48.64, 47.32) * mm});
            skLineSegment(sketch, "E20.3.2.1", {"start": v(40.38, 51.9) * mm, "end": v(38.38, 51.9) * mm});
            skLineSegment(sketch, "E20.3.2.2", {"start": v(40.38, 57.35) * mm, "end": v(40.38, 51.9) * mm});
            skLineSegment(sketch, "E20.3.2.3", {"start": v(43.56, 57.35) * mm, "end": v(43.56, 55.97) * mm});
            skPoint(sketch, "E20.3.2.4", {"position": v(40.38, 43.44) * mm});
            skPoint(sketch, "E20.3.2.5", {"position": v(43.56, 46.32) * mm});
            skLineSegment(sketch, "E20.3.2.6", {"start": v(44.06, 55.47) * mm, "end": v(47.64, 55.47) * mm});
            skLineSegment(sketch, "E20.3.2.7", {"start": v(43.56, 45.82) * mm, "end": v(43.56, 44.44) * mm});
            skPoint(sketch, "E20.3.2.8", {"position": v(43.56, 58.35) * mm});
            skLineSegment(sketch, "E20.3.2.9", {"start": v(40.38, 49.9) * mm, "end": v(40.38, 44.44) * mm});
            skLineSegment(sketch, "E20.3.2.10", {"start": v(41.38, 58.35) * mm, "end": v(42.56, 58.35) * mm});
            skLineSegment(sketch, "E20.3.2.11", {"start": v(41.38, 43.44) * mm, "end": v(42.56, 43.44) * mm});
            skLineSegment(sketch, "E20.3.2.12", {"start": v(38.38, 51.9) * mm, "end": v(38.38, 49.9) * mm});
            skLineSegment(sketch, "E20.3.2.13", {"start": v(40.38, 49.9) * mm, "end": v(38.38, 49.9) * mm});
            skLineSegment(sketch, "E20.3.2.14", {"start": v(44.06, 46.32) * mm, "end": v(47.64, 46.32) * mm});
            skPoint(sketch, "E20.3.2.15", {"position": v(43.56, 55.47) * mm});
            skPoint(sketch, "E20.3.2.16", {"position": v(43.56, 43.44) * mm});
            skPoint(sketch, "E20.3.2.17", {"position": v(40.38, 58.35) * mm});
            skPoint(sketch, "E20.3.2.18", {"position": v(48.64, 55.47) * mm});
            skPoint(sketch, "E20.3.2.19", {"position": v(48.64, 46.32) * mm});
            skArc(sketch, "E20.3.2.20", {"start": v(41.38, 58.35) * mm, "mid": v(40.67, 58.06) * mm, "end": v(40.38, 57.35) * mm});
            skArc(sketch, "E20.3.2.21", {"start": v(48.64, 54.47) * mm, "mid": v(48.34, 55.17) * mm, "end": v(47.64, 55.47) * mm});
            skArc(sketch, "E20.3.2.22", {"start": v(43.56, 57.35) * mm, "mid": v(43.26, 58.06) * mm, "end": v(42.56, 58.35) * mm});
            skArc(sketch, "E20.3.2.23", {"start": v(40.38, 44.44) * mm, "mid": v(40.67, 43.73) * mm, "end": v(41.38, 43.44) * mm});
            skArc(sketch, "E20.3.2.24", {"start": v(42.56, 43.44) * mm, "mid": v(43.26, 43.73) * mm, "end": v(43.56, 44.44) * mm});
            skArc(sketch, "E20.3.2.25", {"start": v(47.64, 46.32) * mm, "mid": v(48.34, 46.62) * mm, "end": v(48.64, 47.32) * mm});
            skArc(sketch, "E20.3.2.26", {"start": v(44.06, 46.32) * mm, "mid": v(43.7, 46.18) * mm, "end": v(43.56, 45.82) * mm});
            skArc(sketch, "E20.3.2.27", {"start": v(43.56, 55.97) * mm, "mid": v(43.7, 55.61) * mm, "end": v(44.06, 55.47) * mm});
            skLineSegment(sketch, "E20.3.3.0", {"start": v(48.64, 71.38) * mm, "end": v(48.64, 64.23) * mm});
            skLineSegment(sketch, "E20.3.3.1", {"start": v(40.38, 68.8) * mm, "end": v(38.38, 68.8) * mm});
            skLineSegment(sketch, "E20.3.3.2", {"start": v(40.38, 74.26) * mm, "end": v(40.38, 68.8) * mm});
            skLineSegment(sketch, "E20.3.3.3", {"start": v(43.56, 74.26) * mm, "end": v(43.56, 72.88) * mm});
            skPoint(sketch, "E20.3.3.4", {"position": v(40.38, 60.35) * mm});
            skPoint(sketch, "E20.3.3.5", {"position": v(43.56, 63.23) * mm});
            skLineSegment(sketch, "E20.3.3.6", {"start": v(44.06, 72.38) * mm, "end": v(47.64, 72.38) * mm});
            skLineSegment(sketch, "E20.3.3.7", {"start": v(43.56, 62.73) * mm, "end": v(43.56, 61.35) * mm});
            skPoint(sketch, "E20.3.3.8", {"position": v(43.56, 75.26) * mm});
            skLineSegment(sketch, "E20.3.3.9", {"start": v(40.38, 66.8) * mm, "end": v(40.38, 61.35) * mm});
            skLineSegment(sketch, "E20.3.3.10", {"start": v(41.38, 75.26) * mm, "end": v(42.56, 75.26) * mm});
            skLineSegment(sketch, "E20.3.3.11", {"start": v(41.38, 60.35) * mm, "end": v(42.56, 60.35) * mm});
            skLineSegment(sketch, "E20.3.3.12", {"start": v(38.38, 68.8) * mm, "end": v(38.38, 66.8) * mm});
            skLineSegment(sketch, "E20.3.3.13", {"start": v(40.38, 66.8) * mm, "end": v(38.38, 66.8) * mm});
            skLineSegment(sketch, "E20.3.3.14", {"start": v(44.06, 63.23) * mm, "end": v(47.64, 63.23) * mm});
            skPoint(sketch, "E20.3.3.15", {"position": v(43.56, 72.38) * mm});
            skPoint(sketch, "E20.3.3.16", {"position": v(43.56, 60.35) * mm});
            skPoint(sketch, "E20.3.3.17", {"position": v(40.38, 75.26) * mm});
            skPoint(sketch, "E20.3.3.18", {"position": v(48.64, 72.38) * mm});
            skPoint(sketch, "E20.3.3.19", {"position": v(48.64, 63.23) * mm});
            skArc(sketch, "E20.3.3.20", {"start": v(41.38, 75.26) * mm, "mid": v(40.67, 74.97) * mm, "end": v(40.38, 74.26) * mm});
            skArc(sketch, "E20.3.3.21", {"start": v(48.64, 71.38) * mm, "mid": v(48.34, 72.08) * mm, "end": v(47.64, 72.38) * mm});
            skArc(sketch, "E20.3.3.22", {"start": v(43.56, 74.26) * mm, "mid": v(43.26, 74.97) * mm, "end": v(42.56, 75.26) * mm});
            skArc(sketch, "E20.3.3.23", {"start": v(40.38, 61.35) * mm, "mid": v(40.67, 60.64) * mm, "end": v(41.38, 60.35) * mm});
            skArc(sketch, "E20.3.3.24", {"start": v(42.56, 60.35) * mm, "mid": v(43.26, 60.64) * mm, "end": v(43.56, 61.35) * mm});
            skArc(sketch, "E20.3.3.25", {"start": v(47.64, 63.23) * mm, "mid": v(48.34, 63.53) * mm, "end": v(48.64, 64.23) * mm});
            skArc(sketch, "E20.3.3.26", {"start": v(44.06, 63.23) * mm, "mid": v(43.7, 63.09) * mm, "end": v(43.56, 62.73) * mm});
            skArc(sketch, "E20.3.3.27", {"start": v(43.56, 72.88) * mm, "mid": v(43.7, 72.52) * mm, "end": v(44.06, 72.38) * mm});
            skLineSegment(sketch, "E20.3.4.0", {"start": v(48.64, 88.29) * mm, "end": v(48.64, 81.14) * mm});
            skLineSegment(sketch, "E20.3.4.1", {"start": v(40.38, 85.71) * mm, "end": v(38.38, 85.71) * mm});
            skLineSegment(sketch, "E20.3.4.2", {"start": v(40.38, 91.17) * mm, "end": v(40.38, 85.71) * mm});
            skLineSegment(sketch, "E20.3.4.3", {"start": v(43.56, 91.17) * mm, "end": v(43.56, 89.79) * mm});
            skPoint(sketch, "E20.3.4.4", {"position": v(40.38, 77.26) * mm});
            skPoint(sketch, "E20.3.4.5", {"position": v(43.56, 80.14) * mm});
            skLineSegment(sketch, "E20.3.4.6", {"start": v(44.06, 89.29) * mm, "end": v(47.64, 89.29) * mm});
            skLineSegment(sketch, "E20.3.4.7", {"start": v(43.56, 79.64) * mm, "end": v(43.56, 78.26) * mm});
            skPoint(sketch, "E20.3.4.8", {"position": v(43.56, 92.17) * mm});
            skLineSegment(sketch, "E20.3.4.9", {"start": v(40.38, 83.71) * mm, "end": v(40.38, 78.26) * mm});
            skLineSegment(sketch, "E20.3.4.10", {"start": v(41.38, 92.17) * mm, "end": v(42.56, 92.17) * mm});
            skLineSegment(sketch, "E20.3.4.11", {"start": v(41.38, 77.26) * mm, "end": v(42.56, 77.26) * mm});
            skLineSegment(sketch, "E20.3.4.12", {"start": v(38.38, 85.71) * mm, "end": v(38.38, 83.71) * mm});
            skLineSegment(sketch, "E20.3.4.13", {"start": v(40.38, 83.71) * mm, "end": v(38.38, 83.71) * mm});
            skLineSegment(sketch, "E20.3.4.14", {"start": v(44.06, 80.14) * mm, "end": v(47.64, 80.14) * mm});
            skPoint(sketch, "E20.3.4.15", {"position": v(43.56, 89.29) * mm});
            skPoint(sketch, "E20.3.4.16", {"position": v(43.56, 77.26) * mm});
            skPoint(sketch, "E20.3.4.17", {"position": v(40.38, 92.17) * mm});
            skPoint(sketch, "E20.3.4.18", {"position": v(48.64, 89.29) * mm});
            skPoint(sketch, "E20.3.4.19", {"position": v(48.64, 80.14) * mm});
            skArc(sketch, "E20.3.4.20", {"start": v(41.38, 92.17) * mm, "mid": v(40.67, 91.88) * mm, "end": v(40.38, 91.17) * mm});
            skArc(sketch, "E20.3.4.21", {"start": v(48.64, 88.29) * mm, "mid": v(48.34, 89) * mm, "end": v(47.64, 89.29) * mm});
            skArc(sketch, "E20.3.4.22", {"start": v(43.56, 91.17) * mm, "mid": v(43.26, 91.88) * mm, "end": v(42.56, 92.17) * mm});
            skArc(sketch, "E20.3.4.23", {"start": v(40.38, 78.26) * mm, "mid": v(40.67, 77.55) * mm, "end": v(41.38, 77.26) * mm});
            skArc(sketch, "E20.3.4.24", {"start": v(42.56, 77.26) * mm, "mid": v(43.26, 77.55) * mm, "end": v(43.56, 78.26) * mm});
            skArc(sketch, "E20.3.4.25", {"start": v(47.64, 80.14) * mm, "mid": v(48.34, 80.44) * mm, "end": v(48.64, 81.14) * mm});
            skArc(sketch, "E20.3.4.26", {"start": v(44.06, 80.14) * mm, "mid": v(43.7, 80) * mm, "end": v(43.56, 79.64) * mm});
            skArc(sketch, "E20.3.4.27", {"start": v(43.56, 89.79) * mm, "mid": v(43.7, 89.43) * mm, "end": v(44.06, 89.29) * mm});
            skLineSegment(sketch, "E20.4.0.0", {"start": v(58.9, 20.65) * mm, "end": v(58.9, 13.5) * mm});
            skLineSegment(sketch, "E20.4.0.1", {"start": v(50.64, 18.07) * mm, "end": v(48.64, 18.07) * mm});
            skLineSegment(sketch, "E20.4.0.2", {"start": v(50.64, 23.53) * mm, "end": v(50.64, 18.07) * mm});
            skLineSegment(sketch, "E20.4.0.3", {"start": v(53.81, 23.53) * mm, "end": v(53.81, 22.15) * mm});
            skPoint(sketch, "E20.4.0.4", {"position": v(50.64, 9.62) * mm});
            skPoint(sketch, "E20.4.0.5", {"position": v(53.81, 12.5) * mm});
            skLineSegment(sketch, "E20.4.0.6", {"start": v(54.31, 21.65) * mm, "end": v(57.9, 21.65) * mm});
            skLineSegment(sketch, "E20.4.0.7", {"start": v(53.81, 12) * mm, "end": v(53.81, 10.62) * mm});
            skPoint(sketch, "E20.4.0.8", {"position": v(53.81, 24.53) * mm});
            skLineSegment(sketch, "E20.4.0.9", {"start": v(50.64, 16.07) * mm, "end": v(50.64, 10.62) * mm});
            skLineSegment(sketch, "E20.4.0.10", {"start": v(51.64, 24.53) * mm, "end": v(52.81, 24.53) * mm});
            skLineSegment(sketch, "E20.4.0.11", {"start": v(51.64, 9.62) * mm, "end": v(52.81, 9.62) * mm});
            skLineSegment(sketch, "E20.4.0.12", {"start": v(48.64, 18.07) * mm, "end": v(48.64, 16.07) * mm});
            skLineSegment(sketch, "E20.4.0.13", {"start": v(50.64, 16.07) * mm, "end": v(48.64, 16.07) * mm});
            skLineSegment(sketch, "E20.4.0.14", {"start": v(54.31, 12.5) * mm, "end": v(57.9, 12.5) * mm});
            skPoint(sketch, "E20.4.0.15", {"position": v(53.81, 21.65) * mm});
            skPoint(sketch, "E20.4.0.16", {"position": v(53.81, 9.62) * mm});
            skPoint(sketch, "E20.4.0.17", {"position": v(50.64, 24.53) * mm});
            skPoint(sketch, "E20.4.0.18", {"position": v(58.9, 21.65) * mm});
            skPoint(sketch, "E20.4.0.19", {"position": v(58.9, 12.5) * mm});
            skArc(sketch, "E20.4.0.20", {"start": v(51.64, 24.53) * mm, "mid": v(50.93, 24.24) * mm, "end": v(50.64, 23.53) * mm});
            skArc(sketch, "E20.4.0.21", {"start": v(58.9, 20.65) * mm, "mid": v(58.6, 21.35) * mm, "end": v(57.9, 21.65) * mm});
            skArc(sketch, "E20.4.0.22", {"start": v(53.81, 23.53) * mm, "mid": v(53.52, 24.24) * mm, "end": v(52.81, 24.53) * mm});
            skArc(sketch, "E20.4.0.23", {"start": v(50.64, 10.62) * mm, "mid": v(50.93, 9.91) * mm, "end": v(51.64, 9.62) * mm});
            skArc(sketch, "E20.4.0.24", {"start": v(52.81, 9.62) * mm, "mid": v(53.52, 9.91) * mm, "end": v(53.81, 10.62) * mm});
            skArc(sketch, "E20.4.0.25", {"start": v(57.9, 12.5) * mm, "mid": v(58.6, 12.8) * mm, "end": v(58.9, 13.5) * mm});
            skArc(sketch, "E20.4.0.26", {"start": v(54.31, 12.5) * mm, "mid": v(53.96, 12.36) * mm, "end": v(53.81, 12) * mm});
            skArc(sketch, "E20.4.0.27", {"start": v(53.81, 22.15) * mm, "mid": v(53.96, 21.8) * mm, "end": v(54.31, 21.65) * mm});
            skLineSegment(sketch, "E20.4.1.0", {"start": v(58.9, 37.56) * mm, "end": v(58.9, 30.41) * mm});
            skLineSegment(sketch, "E20.4.1.1", {"start": v(50.64, 34.98) * mm, "end": v(48.64, 34.98) * mm});
            skLineSegment(sketch, "E20.4.1.2", {"start": v(50.64, 40.44) * mm, "end": v(50.64, 34.98) * mm});
            skLineSegment(sketch, "E20.4.1.3", {"start": v(53.81, 40.44) * mm, "end": v(53.81, 39.06) * mm});
            skPoint(sketch, "E20.4.1.4", {"position": v(50.64, 26.53) * mm});
            skPoint(sketch, "E20.4.1.5", {"position": v(53.81, 29.41) * mm});
            skLineSegment(sketch, "E20.4.1.6", {"start": v(54.31, 38.56) * mm, "end": v(57.9, 38.56) * mm});
            skLineSegment(sketch, "E20.4.1.7", {"start": v(53.81, 28.91) * mm, "end": v(53.81, 27.53) * mm});
            skPoint(sketch, "E20.4.1.8", {"position": v(53.81, 41.44) * mm});
            skLineSegment(sketch, "E20.4.1.9", {"start": v(50.64, 32.98) * mm, "end": v(50.64, 27.53) * mm});
            skLineSegment(sketch, "E20.4.1.10", {"start": v(51.64, 41.44) * mm, "end": v(52.81, 41.44) * mm});
            skLineSegment(sketch, "E20.4.1.11", {"start": v(51.64, 26.53) * mm, "end": v(52.81, 26.53) * mm});
            skLineSegment(sketch, "E20.4.1.12", {"start": v(48.64, 34.98) * mm, "end": v(48.64, 32.98) * mm});
            skLineSegment(sketch, "E20.4.1.13", {"start": v(50.64, 32.98) * mm, "end": v(48.64, 32.98) * mm});
            skLineSegment(sketch, "E20.4.1.14", {"start": v(54.31, 29.41) * mm, "end": v(57.9, 29.41) * mm});
            skPoint(sketch, "E20.4.1.15", {"position": v(53.81, 38.56) * mm});
            skPoint(sketch, "E20.4.1.16", {"position": v(53.81, 26.53) * mm});
            skPoint(sketch, "E20.4.1.17", {"position": v(50.64, 41.44) * mm});
            skPoint(sketch, "E20.4.1.18", {"position": v(58.9, 38.56) * mm});
            skPoint(sketch, "E20.4.1.19", {"position": v(58.9, 29.41) * mm});
            skArc(sketch, "E20.4.1.20", {"start": v(51.64, 41.44) * mm, "mid": v(50.93, 41.15) * mm, "end": v(50.64, 40.44) * mm});
            skArc(sketch, "E20.4.1.21", {"start": v(58.9, 37.56) * mm, "mid": v(58.6, 38.26) * mm, "end": v(57.9, 38.56) * mm});
            skArc(sketch, "E20.4.1.22", {"start": v(53.81, 40.44) * mm, "mid": v(53.52, 41.15) * mm, "end": v(52.81, 41.44) * mm});
            skArc(sketch, "E20.4.1.23", {"start": v(50.64, 27.53) * mm, "mid": v(50.93, 26.82) * mm, "end": v(51.64, 26.53) * mm});
            skArc(sketch, "E20.4.1.24", {"start": v(52.81, 26.53) * mm, "mid": v(53.52, 26.82) * mm, "end": v(53.81, 27.53) * mm});
            skArc(sketch, "E20.4.1.25", {"start": v(57.9, 29.41) * mm, "mid": v(58.6, 29.7) * mm, "end": v(58.9, 30.41) * mm});
            skArc(sketch, "E20.4.1.26", {"start": v(54.31, 29.41) * mm, "mid": v(53.96, 29.27) * mm, "end": v(53.81, 28.91) * mm});
            skArc(sketch, "E20.4.1.27", {"start": v(53.81, 39.06) * mm, "mid": v(53.96, 38.7) * mm, "end": v(54.31, 38.56) * mm});
            skLineSegment(sketch, "E20.4.2.0", {"start": v(58.9, 54.47) * mm, "end": v(58.9, 47.32) * mm});
            skLineSegment(sketch, "E20.4.2.1", {"start": v(50.64, 51.9) * mm, "end": v(48.64, 51.9) * mm});
            skLineSegment(sketch, "E20.4.2.2", {"start": v(50.64, 57.35) * mm, "end": v(50.64, 51.9) * mm});
            skLineSegment(sketch, "E20.4.2.3", {"start": v(53.81, 57.35) * mm, "end": v(53.81, 55.97) * mm});
            skPoint(sketch, "E20.4.2.4", {"position": v(50.64, 43.44) * mm});
            skPoint(sketch, "E20.4.2.5", {"position": v(53.81, 46.32) * mm});
            skLineSegment(sketch, "E20.4.2.6", {"start": v(54.31, 55.47) * mm, "end": v(57.9, 55.47) * mm});
            skLineSegment(sketch, "E20.4.2.7", {"start": v(53.81, 45.82) * mm, "end": v(53.81, 44.44) * mm});
            skPoint(sketch, "E20.4.2.8", {"position": v(53.81, 58.35) * mm});
            skLineSegment(sketch, "E20.4.2.9", {"start": v(50.64, 49.9) * mm, "end": v(50.64, 44.44) * mm});
            skLineSegment(sketch, "E20.4.2.10", {"start": v(51.64, 58.35) * mm, "end": v(52.81, 58.35) * mm});
            skLineSegment(sketch, "E20.4.2.11", {"start": v(51.64, 43.44) * mm, "end": v(52.81, 43.44) * mm});
            skLineSegment(sketch, "E20.4.2.12", {"start": v(48.64, 51.9) * mm, "end": v(48.64, 49.9) * mm});
            skLineSegment(sketch, "E20.4.2.13", {"start": v(50.64, 49.9) * mm, "end": v(48.64, 49.9) * mm});
            skLineSegment(sketch, "E20.4.2.14", {"start": v(54.31, 46.32) * mm, "end": v(57.9, 46.32) * mm});
            skPoint(sketch, "E20.4.2.15", {"position": v(53.81, 55.47) * mm});
            skPoint(sketch, "E20.4.2.16", {"position": v(53.81, 43.44) * mm});
            skPoint(sketch, "E20.4.2.17", {"position": v(50.64, 58.35) * mm});
            skPoint(sketch, "E20.4.2.18", {"position": v(58.9, 55.47) * mm});
            skPoint(sketch, "E20.4.2.19", {"position": v(58.9, 46.32) * mm});
            skArc(sketch, "E20.4.2.20", {"start": v(51.64, 58.35) * mm, "mid": v(50.93, 58.06) * mm, "end": v(50.64, 57.35) * mm});
            skArc(sketch, "E20.4.2.21", {"start": v(58.9, 54.47) * mm, "mid": v(58.6, 55.17) * mm, "end": v(57.9, 55.47) * mm});
            skArc(sketch, "E20.4.2.22", {"start": v(53.81, 57.35) * mm, "mid": v(53.52, 58.06) * mm, "end": v(52.81, 58.35) * mm});
            skArc(sketch, "E20.4.2.23", {"start": v(50.64, 44.44) * mm, "mid": v(50.93, 43.73) * mm, "end": v(51.64, 43.44) * mm});
            skArc(sketch, "E20.4.2.24", {"start": v(52.81, 43.44) * mm, "mid": v(53.52, 43.73) * mm, "end": v(53.81, 44.44) * mm});
            skArc(sketch, "E20.4.2.25", {"start": v(57.9, 46.32) * mm, "mid": v(58.6, 46.62) * mm, "end": v(58.9, 47.32) * mm});
            skArc(sketch, "E20.4.2.26", {"start": v(54.31, 46.32) * mm, "mid": v(53.96, 46.18) * mm, "end": v(53.81, 45.82) * mm});
            skArc(sketch, "E20.4.2.27", {"start": v(53.81, 55.97) * mm, "mid": v(53.96, 55.61) * mm, "end": v(54.31, 55.47) * mm});
            skLineSegment(sketch, "E20.4.3.0", {"start": v(58.9, 71.38) * mm, "end": v(58.9, 64.23) * mm});
            skLineSegment(sketch, "E20.4.3.1", {"start": v(50.64, 68.8) * mm, "end": v(48.64, 68.8) * mm});
            skLineSegment(sketch, "E20.4.3.2", {"start": v(50.64, 74.26) * mm, "end": v(50.64, 68.8) * mm});
            skLineSegment(sketch, "E20.4.3.3", {"start": v(53.81, 74.26) * mm, "end": v(53.81, 72.88) * mm});
            skPoint(sketch, "E20.4.3.4", {"position": v(50.64, 60.35) * mm});
            skPoint(sketch, "E20.4.3.5", {"position": v(53.81, 63.23) * mm});
            skLineSegment(sketch, "E20.4.3.6", {"start": v(54.31, 72.38) * mm, "end": v(57.9, 72.38) * mm});
            skLineSegment(sketch, "E20.4.3.7", {"start": v(53.81, 62.73) * mm, "end": v(53.81, 61.35) * mm});
            skPoint(sketch, "E20.4.3.8", {"position": v(53.81, 75.26) * mm});
            skLineSegment(sketch, "E20.4.3.9", {"start": v(50.64, 66.8) * mm, "end": v(50.64, 61.35) * mm});
            skLineSegment(sketch, "E20.4.3.10", {"start": v(51.64, 75.26) * mm, "end": v(52.81, 75.26) * mm});
            skLineSegment(sketch, "E20.4.3.11", {"start": v(51.64, 60.35) * mm, "end": v(52.81, 60.35) * mm});
            skLineSegment(sketch, "E20.4.3.12", {"start": v(48.64, 68.8) * mm, "end": v(48.64, 66.8) * mm});
            skLineSegment(sketch, "E20.4.3.13", {"start": v(50.64, 66.8) * mm, "end": v(48.64, 66.8) * mm});
            skLineSegment(sketch, "E20.4.3.14", {"start": v(54.31, 63.23) * mm, "end": v(57.9, 63.23) * mm});
            skPoint(sketch, "E20.4.3.15", {"position": v(53.81, 72.38) * mm});
            skPoint(sketch, "E20.4.3.16", {"position": v(53.81, 60.35) * mm});
            skPoint(sketch, "E20.4.3.17", {"position": v(50.64, 75.26) * mm});
            skPoint(sketch, "E20.4.3.18", {"position": v(58.9, 72.38) * mm});
            skPoint(sketch, "E20.4.3.19", {"position": v(58.9, 63.23) * mm});
            skArc(sketch, "E20.4.3.20", {"start": v(51.64, 75.26) * mm, "mid": v(50.93, 74.97) * mm, "end": v(50.64, 74.26) * mm});
            skArc(sketch, "E20.4.3.21", {"start": v(58.9, 71.38) * mm, "mid": v(58.6, 72.08) * mm, "end": v(57.9, 72.38) * mm});
            skArc(sketch, "E20.4.3.22", {"start": v(53.81, 74.26) * mm, "mid": v(53.52, 74.97) * mm, "end": v(52.81, 75.26) * mm});
            skArc(sketch, "E20.4.3.23", {"start": v(50.64, 61.35) * mm, "mid": v(50.93, 60.64) * mm, "end": v(51.64, 60.35) * mm});
            skArc(sketch, "E20.4.3.24", {"start": v(52.81, 60.35) * mm, "mid": v(53.52, 60.64) * mm, "end": v(53.81, 61.35) * mm});
            skArc(sketch, "E20.4.3.25", {"start": v(57.9, 63.23) * mm, "mid": v(58.6, 63.53) * mm, "end": v(58.9, 64.23) * mm});
            skArc(sketch, "E20.4.3.26", {"start": v(54.31, 63.23) * mm, "mid": v(53.96, 63.09) * mm, "end": v(53.81, 62.73) * mm});
            skArc(sketch, "E20.4.3.27", {"start": v(53.81, 72.88) * mm, "mid": v(53.96, 72.52) * mm, "end": v(54.31, 72.38) * mm});
            skLineSegment(sketch, "E20.4.4.0", {"start": v(58.9, 88.29) * mm, "end": v(58.9, 81.14) * mm});
            skLineSegment(sketch, "E20.4.4.1", {"start": v(50.64, 85.71) * mm, "end": v(48.64, 85.71) * mm});
            skLineSegment(sketch, "E20.4.4.2", {"start": v(50.64, 91.17) * mm, "end": v(50.64, 85.71) * mm});
            skLineSegment(sketch, "E20.4.4.3", {"start": v(53.81, 91.17) * mm, "end": v(53.81, 89.79) * mm});
            skPoint(sketch, "E20.4.4.4", {"position": v(50.64, 77.26) * mm});
            skPoint(sketch, "E20.4.4.5", {"position": v(53.81, 80.14) * mm});
            skLineSegment(sketch, "E20.4.4.6", {"start": v(54.31, 89.29) * mm, "end": v(57.9, 89.29) * mm});
            skLineSegment(sketch, "E20.4.4.7", {"start": v(53.81, 79.64) * mm, "end": v(53.81, 78.26) * mm});
            skPoint(sketch, "E20.4.4.8", {"position": v(53.81, 92.17) * mm});
            skLineSegment(sketch, "E20.4.4.9", {"start": v(50.64, 83.71) * mm, "end": v(50.64, 78.26) * mm});
            skLineSegment(sketch, "E20.4.4.10", {"start": v(51.64, 92.17) * mm, "end": v(52.81, 92.17) * mm});
            skLineSegment(sketch, "E20.4.4.11", {"start": v(51.64, 77.26) * mm, "end": v(52.81, 77.26) * mm});
            skLineSegment(sketch, "E20.4.4.12", {"start": v(48.64, 85.71) * mm, "end": v(48.64, 83.71) * mm});
            skLineSegment(sketch, "E20.4.4.13", {"start": v(50.64, 83.71) * mm, "end": v(48.64, 83.71) * mm});
            skLineSegment(sketch, "E20.4.4.14", {"start": v(54.31, 80.14) * mm, "end": v(57.9, 80.14) * mm});
            skPoint(sketch, "E20.4.4.15", {"position": v(53.81, 89.29) * mm});
            skPoint(sketch, "E20.4.4.16", {"position": v(53.81, 77.26) * mm});
            skPoint(sketch, "E20.4.4.17", {"position": v(50.64, 92.17) * mm});
            skPoint(sketch, "E20.4.4.18", {"position": v(58.9, 89.29) * mm});
            skPoint(sketch, "E20.4.4.19", {"position": v(58.9, 80.14) * mm});
            skArc(sketch, "E20.4.4.20", {"start": v(51.64, 92.17) * mm, "mid": v(50.93, 91.88) * mm, "end": v(50.64, 91.17) * mm});
            skArc(sketch, "E20.4.4.21", {"start": v(58.9, 88.29) * mm, "mid": v(58.6, 89) * mm, "end": v(57.9, 89.29) * mm});
            skArc(sketch, "E20.4.4.22", {"start": v(53.81, 91.17) * mm, "mid": v(53.52, 91.88) * mm, "end": v(52.81, 92.17) * mm});
            skArc(sketch, "E20.4.4.23", {"start": v(50.64, 78.26) * mm, "mid": v(50.93, 77.55) * mm, "end": v(51.64, 77.26) * mm});
            skArc(sketch, "E20.4.4.24", {"start": v(52.81, 77.26) * mm, "mid": v(53.52, 77.55) * mm, "end": v(53.81, 78.26) * mm});
            skArc(sketch, "E20.4.4.25", {"start": v(57.9, 80.14) * mm, "mid": v(58.6, 80.44) * mm, "end": v(58.9, 81.14) * mm});
            skArc(sketch, "E20.4.4.26", {"start": v(54.31, 80.14) * mm, "mid": v(53.96, 80) * mm, "end": v(53.81, 79.64) * mm});
            skArc(sketch, "E20.4.4.27", {"start": v(53.81, 89.79) * mm, "mid": v(53.96, 89.43) * mm, "end": v(54.31, 89.29) * mm});
            skLineSegment(sketch, "E20.direction1", {"start": v(9.62, 9.62) * mm, "end": v(19.87, 9.62) * mm, "construction": true});
            skLineSegment(sketch, "E20.direction2", {"start": v(9.62, 9.62) * mm, "end": v(9.62, 26.53) * mm, "construction": true});
            skLineSegment(sketch, "E21.bottom", {"start": v(58.9, 16.07) * mm, "end": v(60.9, 16.07) * mm});
            skLineSegment(sketch, "E21.top", {"start": v(58.9, 18.07) * mm, "end": v(60.9, 18.07) * mm});
            skLineSegment(sketch, "E21.left", {"start": v(58.9, 16.07) * mm, "end": v(58.9, 18.07) * mm});
            skLineSegment(sketch, "E21.right", {"start": v(60.9, 16.07) * mm, "end": v(60.9, 18.07) * mm});
            skLineSegment(sketch, "E22.bottom", {"start": v(58.9, 32.98) * mm, "end": v(60.9, 32.98) * mm});
            skLineSegment(sketch, "E22.top", {"start": v(58.9, 34.98) * mm, "end": v(60.9, 34.98) * mm});
            skLineSegment(sketch, "E22.left", {"start": v(58.9, 32.98) * mm, "end": v(58.9, 34.98) * mm});
            skLineSegment(sketch, "E22.right", {"start": v(60.9, 32.98) * mm, "end": v(60.9, 34.98) * mm});
            skLineSegment(sketch, "E23.bottom", {"start": v(58.9, 49.9) * mm, "end": v(60.9, 49.9) * mm});
            skLineSegment(sketch, "E23.top", {"start": v(58.9, 51.9) * mm, "end": v(60.9, 51.9) * mm});
            skLineSegment(sketch, "E23.left", {"start": v(58.9, 49.9) * mm, "end": v(58.9, 51.9) * mm});
            skLineSegment(sketch, "E23.right", {"start": v(60.9, 49.9) * mm, "end": v(60.9, 51.9) * mm});
            skLineSegment(sketch, "E24.bottom", {"start": v(58.9, 66.8) * mm, "end": v(60.9, 66.8) * mm});
            skLineSegment(sketch, "E24.top", {"start": v(58.9, 68.8) * mm, "end": v(60.9, 68.8) * mm});
            skLineSegment(sketch, "E24.left", {"start": v(58.9, 66.8) * mm, "end": v(58.9, 68.8) * mm});
            skLineSegment(sketch, "E24.right", {"start": v(60.9, 66.8) * mm, "end": v(60.9, 68.8) * mm});
            skLineSegment(sketch, "E25.bottom", {"start": v(58.9, 83.71) * mm, "end": v(60.9, 83.71) * mm});
            skLineSegment(sketch, "E25.top", {"start": v(58.9, 85.71) * mm, "end": v(60.9, 85.71) * mm});
            skLineSegment(sketch, "E25.left", {"start": v(58.9, 83.71) * mm, "end": v(58.9, 85.71) * mm});
            skLineSegment(sketch, "E25.right", {"start": v(60.9, 83.71) * mm, "end": v(60.9, 85.71) * mm});
            skPoint(sketch, "E26.1.0.0", {"position": v(89.02, 72.38) * mm});
            skPoint(sketch, "E26.1.0.1", {"position": v(104.45, 29.41) * mm});
            skPoint(sketch, "E26.1.0.2", {"position": v(114.7, 80.14) * mm});
            skPoint(sketch, "E26.1.0.3", {"position": v(111.53, 26.53) * mm});
            skPoint(sketch, "E26.1.0.4", {"position": v(104.45, 72.38) * mm});
            skPoint(sketch, "E26.1.0.5", {"position": v(104.45, 80.14) * mm});
            skPoint(sketch, "E26.1.0.6", {"position": v(83.94, 29.41) * mm});
            skPoint(sketch, "E26.1.0.7", {"position": v(104.45, 46.32) * mm});
            skPoint(sketch, "E26.1.0.8", {"position": v(91.02, 77.26) * mm});
            skPoint(sketch, "E26.1.0.9", {"position": v(73.69, 89.29) * mm});
            skPoint(sketch, "E26.1.0.10", {"position": v(70.51, 41.44) * mm});
            skPoint(sketch, "E26.1.0.11", {"position": v(83.94, 24.53) * mm});
            skPoint(sketch, "E26.1.0.12", {"position": v(104.45, 41.44) * mm});
            skPoint(sketch, "E26.1.0.13", {"position": v(119.78, 12.5) * mm});
            skPoint(sketch, "E26.1.0.14", {"position": v(83.94, 92.17) * mm});
            skPoint(sketch, "E26.1.0.15", {"position": v(109.53, 38.56) * mm});
            skLineSegment(sketch, "E26.1.0.16", {"start": v(91.02, 66.8) * mm, "end": v(91.02, 61.35) * mm});
            skLineSegment(sketch, "E26.1.0.17", {"start": v(70.51, 74.26) * mm, "end": v(70.51, 68.8) * mm});
            skPoint(sketch, "E26.1.0.18", {"position": v(111.53, 43.44) * mm});
            skPoint(sketch, "E26.1.0.19", {"position": v(104.45, 75.26) * mm});
            skPoint(sketch, "E26.1.0.20", {"position": v(111.53, 9.62) * mm});
            skPoint(sketch, "E26.1.0.21", {"position": v(114.7, 29.41) * mm});
            skPoint(sketch, "E26.1.0.22", {"position": v(78.77, 63.23) * mm});
            skPoint(sketch, "E26.1.0.23", {"position": v(70.51, 9.62) * mm});
            skPoint(sketch, "E26.1.0.24", {"position": v(94.2, 9.62) * mm});
            skLineSegment(sketch, "E26.1.0.25", {"start": v(91.02, 16.07) * mm, "end": v(91.02, 10.62) * mm});
            skPoint(sketch, "E26.1.0.26", {"position": v(114.7, 58.35) * mm});
            skLineSegment(sketch, "E26.1.0.27", {"start": v(91.02, 74.26) * mm, "end": v(91.02, 68.8) * mm});
            skPoint(sketch, "E26.1.0.28", {"position": v(114.7, 12.5) * mm});
            skPoint(sketch, "E26.1.0.29", {"position": v(94.2, 80.14) * mm});
            skPoint(sketch, "E26.1.0.30", {"position": v(104.45, 38.56) * mm});
            skLineSegment(sketch, "E26.1.0.31", {"start": v(70.51, 49.9) * mm, "end": v(70.51, 44.44) * mm});
            skPoint(sketch, "E26.1.0.32", {"position": v(94.2, 75.26) * mm});
            skPoint(sketch, "E26.1.0.33", {"position": v(111.53, 92.17) * mm});
            skPoint(sketch, "E26.1.0.34", {"position": v(94.2, 46.32) * mm});
            skPoint(sketch, "E26.1.0.35", {"position": v(83.94, 89.29) * mm});
            skPoint(sketch, "E26.1.0.36", {"position": v(99.27, 12.5) * mm});
            skPoint(sketch, "E26.1.0.37", {"position": v(78.77, 12.5) * mm});
            skPoint(sketch, "E26.1.0.38", {"position": v(78.77, 38.56) * mm});
            skPoint(sketch, "E26.1.0.39", {"position": v(114.7, 24.53) * mm});
            skPoint(sketch, "E26.1.0.40", {"position": v(104.45, 12.5) * mm});
            skPoint(sketch, "E26.1.0.41", {"position": v(94.2, 72.38) * mm});
            skPoint(sketch, "E26.1.0.42", {"position": v(91.02, 43.44) * mm});
            skPoint(sketch, "E26.1.0.43", {"position": v(101.27, 26.53) * mm});
            skPoint(sketch, "E26.1.0.44", {"position": v(119.78, 38.56) * mm});
            skPoint(sketch, "E26.1.0.45", {"position": v(89.02, 55.47) * mm});
            skPoint(sketch, "E26.1.0.46", {"position": v(91.02, 26.53) * mm});
            skPoint(sketch, "E26.1.0.47", {"position": v(80.76, 26.53) * mm});
            skPoint(sketch, "E26.1.0.48", {"position": v(73.69, 9.62) * mm});
            skPoint(sketch, "E26.1.0.49", {"position": v(104.45, 21.65) * mm});
            skPoint(sketch, "E26.1.0.50", {"position": v(70.51, 92.17) * mm});
            skPoint(sketch, "E26.1.0.51", {"position": v(91.02, 92.17) * mm});
            skPoint(sketch, "E26.1.0.52", {"position": v(119.78, 80.14) * mm});
            skPoint(sketch, "E26.1.0.53", {"position": v(80.76, 77.26) * mm});
            skPoint(sketch, "E26.1.0.54", {"position": v(78.77, 46.32) * mm});
            skPoint(sketch, "E26.1.0.55", {"position": v(83.94, 80.14) * mm});
            skPoint(sketch, "E26.1.0.56", {"position": v(109.53, 46.32) * mm});
            skPoint(sketch, "E26.1.0.57", {"position": v(94.2, 21.65) * mm});
            skPoint(sketch, "E26.1.0.58", {"position": v(104.45, 92.17) * mm});
            skPoint(sketch, "E26.1.0.59", {"position": v(101.27, 43.44) * mm});
            skPoint(sketch, "E26.1.0.60", {"position": v(70.51, 43.44) * mm});
            skPoint(sketch, "E26.1.0.61", {"position": v(99.27, 21.65) * mm});
            skPoint(sketch, "E26.1.0.62", {"position": v(101.27, 77.26) * mm});
            skPoint(sketch, "E26.1.0.63", {"position": v(83.94, 12.5) * mm});
            skPoint(sketch, "E26.1.0.64", {"position": v(101.27, 92.17) * mm});
            skPoint(sketch, "E26.1.0.65", {"position": v(109.53, 63.23) * mm});
            skLineSegment(sketch, "E26.1.0.66", {"start": v(91.02, 57.35) * mm, "end": v(91.02, 51.9) * mm});
            skPoint(sketch, "E26.1.0.67", {"position": v(89.02, 89.29) * mm});
            skPoint(sketch, "E26.1.0.68", {"position": v(99.27, 72.38) * mm});
            skPoint(sketch, "E26.1.0.69", {"position": v(73.69, 38.56) * mm});
            skPoint(sketch, "E26.1.0.70", {"position": v(73.69, 63.23) * mm});
            skLineSegment(sketch, "E26.1.0.71", {"start": v(91.02, 23.53) * mm, "end": v(91.02, 18.07) * mm});
            skPoint(sketch, "E26.1.0.72", {"position": v(89.02, 46.32) * mm});
            skPoint(sketch, "E26.1.0.73", {"position": v(104.45, 58.35) * mm});
            skPoint(sketch, "E26.1.0.74", {"position": v(94.2, 55.47) * mm});
            skPoint(sketch, "E26.1.0.75", {"position": v(114.7, 38.56) * mm});
            skPoint(sketch, "E26.1.0.76", {"position": v(73.69, 41.44) * mm});
            skPoint(sketch, "E26.1.0.77", {"position": v(89.02, 21.65) * mm});
            skPoint(sketch, "E26.1.0.78", {"position": v(119.78, 29.41) * mm});
            skPoint(sketch, "E26.1.0.79", {"position": v(119.78, 21.65) * mm});
            skPoint(sketch, "E26.1.0.80", {"position": v(78.77, 29.41) * mm});
            skPoint(sketch, "E26.1.0.81", {"position": v(119.78, 89.29) * mm});
            skPoint(sketch, "E26.1.0.82", {"position": v(104.45, 9.62) * mm});
            skPoint(sketch, "E26.1.0.83", {"position": v(94.2, 92.17) * mm});
            skPoint(sketch, "E26.1.0.84", {"position": v(89.02, 38.56) * mm});
            skPoint(sketch, "E26.1.0.85", {"position": v(78.77, 89.29) * mm});
            skPoint(sketch, "E26.1.0.86", {"position": v(91.02, 60.35) * mm});
            skPoint(sketch, "E26.1.0.87", {"position": v(94.2, 12.5) * mm});
            skPoint(sketch, "E26.1.0.88", {"position": v(83.94, 58.35) * mm});
            skPoint(sketch, "E26.1.0.89", {"position": v(94.2, 58.35) * mm});
            skPoint(sketch, "E26.1.0.90", {"position": v(111.53, 60.35) * mm});
            skPoint(sketch, "E26.1.0.91", {"position": v(94.2, 63.23) * mm});
            skPoint(sketch, "E26.1.0.92", {"position": v(80.76, 60.35) * mm});
            skPoint(sketch, "E26.1.0.93", {"position": v(73.69, 24.53) * mm});
            skPoint(sketch, "E26.1.0.94", {"position": v(111.53, 58.35) * mm});
            skPoint(sketch, "E26.1.0.95", {"position": v(99.27, 38.56) * mm});
            skPoint(sketch, "E26.1.0.96", {"position": v(119.78, 55.47) * mm});
            skPoint(sketch, "E26.1.0.97", {"position": v(109.53, 89.29) * mm});
            skPoint(sketch, "E26.1.0.98", {"position": v(94.2, 38.56) * mm});
            skPoint(sketch, "E26.1.0.99", {"position": v(104.45, 24.53) * mm});
            skPoint(sketch, "E26.1.0.100", {"position": v(99.27, 89.29) * mm});
            skPoint(sketch, "E26.1.0.101", {"position": v(89.02, 29.41) * mm});
            skPoint(sketch, "E26.1.0.102", {"position": v(99.27, 46.32) * mm});
            skPoint(sketch, "E26.1.0.103", {"position": v(73.69, 72.38) * mm});
            skPoint(sketch, "E26.1.0.104", {"position": v(99.27, 80.14) * mm});
            skPoint(sketch, "E26.1.0.105", {"position": v(109.53, 80.14) * mm});
            skPoint(sketch, "E26.1.0.106", {"position": v(80.76, 43.44) * mm});
            skPoint(sketch, "E26.1.0.107", {"position": v(94.2, 29.41) * mm});
            skPoint(sketch, "E26.1.0.108", {"position": v(83.94, 55.47) * mm});
            skPoint(sketch, "E26.1.0.109", {"position": v(101.27, 60.35) * mm});
            skPoint(sketch, "E26.1.0.110", {"position": v(80.76, 24.53) * mm});
            skPoint(sketch, "E26.1.0.111", {"position": v(109.53, 21.65) * mm});
            skPoint(sketch, "E26.1.0.112", {"position": v(73.69, 80.14) * mm});
            skLineSegment(sketch, "E26.1.0.113", {"start": v(91.02, 91.17) * mm, "end": v(91.02, 85.71) * mm});
            skPoint(sketch, "E26.1.0.114", {"position": v(73.69, 55.47) * mm});
            skPoint(sketch, "E26.1.0.115", {"position": v(73.69, 92.17) * mm});
            skPoint(sketch, "E26.1.0.116", {"position": v(83.94, 9.62) * mm});
            skLineSegment(sketch, "E26.1.0.117", {"start": v(91.02, 83.71) * mm, "end": v(91.02, 78.26) * mm});
            skPoint(sketch, "E26.1.0.118", {"position": v(119.78, 63.23) * mm});
            skPoint(sketch, "E26.1.0.119", {"position": v(109.53, 29.41) * mm});
            skPoint(sketch, "E26.1.0.120", {"position": v(73.69, 58.35) * mm});
            skPoint(sketch, "E26.1.0.121", {"position": v(80.76, 41.44) * mm});
            skPoint(sketch, "E26.1.0.122", {"position": v(111.53, 75.26) * mm});
            skPoint(sketch, "E26.1.0.123", {"position": v(94.2, 89.29) * mm});
            skPoint(sketch, "E26.1.0.124", {"position": v(114.7, 46.32) * mm});
            skPoint(sketch, "E26.1.0.125", {"position": v(94.2, 24.53) * mm});
            skPoint(sketch, "E26.1.0.126", {"position": v(73.69, 46.32) * mm});
            skPoint(sketch, "E26.1.0.127", {"position": v(104.45, 55.47) * mm});
            skPoint(sketch, "E26.1.0.128", {"position": v(70.51, 75.26) * mm});
            skPoint(sketch, "E26.1.0.129", {"position": v(114.7, 92.17) * mm});
            skPoint(sketch, "E26.1.0.130", {"position": v(111.53, 41.44) * mm});
            skPoint(sketch, "E26.1.0.131", {"position": v(114.7, 21.65) * mm});
            skPoint(sketch, "E26.1.0.132", {"position": v(83.94, 75.26) * mm});
            skPoint(sketch, "E26.1.0.133", {"position": v(114.7, 75.26) * mm});
            skPoint(sketch, "E26.1.0.134", {"position": v(83.94, 63.23) * mm});
            skPoint(sketch, "E26.1.0.135", {"position": v(78.77, 55.47) * mm});
            skPoint(sketch, "E26.1.0.136", {"position": v(99.27, 29.41) * mm});
            skPoint(sketch, "E26.1.0.137", {"position": v(73.69, 75.26) * mm});
            skLineSegment(sketch, "E26.1.0.138", {"start": v(70.51, 66.8) * mm, "end": v(70.51, 61.35) * mm});
            skPoint(sketch, "E26.1.0.139", {"position": v(78.77, 80.14) * mm});
            skPoint(sketch, "E26.1.0.140", {"position": v(109.53, 55.47) * mm});
            skPoint(sketch, "E26.1.0.141", {"position": v(70.51, 58.35) * mm});
            skPoint(sketch, "E26.1.0.142", {"position": v(73.69, 29.41) * mm});
            skPoint(sketch, "E26.1.0.143", {"position": v(80.76, 92.17) * mm});
            skLineSegment(sketch, "E26.1.0.144", {"start": v(70.51, 83.71) * mm, "end": v(70.51, 78.26) * mm});
            skPoint(sketch, "E26.1.0.145", {"position": v(114.7, 41.44) * mm});
            skPoint(sketch, "E26.1.0.146", {"position": v(70.51, 77.26) * mm});
            skLineSegment(sketch, "E26.1.0.147", {"start": v(70.51, 57.35) * mm, "end": v(70.51, 51.9) * mm});
            skPoint(sketch, "E26.1.0.148", {"position": v(83.94, 38.56) * mm});
            skLineSegment(sketch, "E26.1.0.149", {"start": v(91.02, 49.9) * mm, "end": v(91.02, 44.44) * mm});
            skPoint(sketch, "E26.1.0.150", {"position": v(109.53, 12.5) * mm});
            skLineSegment(sketch, "E26.1.0.151", {"start": v(70.51, 40.44) * mm, "end": v(70.51, 34.98) * mm});
            skPoint(sketch, "E26.1.0.152", {"position": v(114.7, 9.62) * mm});
            skPoint(sketch, "E26.1.0.153", {"position": v(101.27, 9.62) * mm});
            skPoint(sketch, "E26.1.0.154", {"position": v(114.7, 89.29) * mm});
            skPoint(sketch, "E26.1.0.155", {"position": v(99.27, 55.47) * mm});
            skPoint(sketch, "E26.1.0.156", {"position": v(111.53, 24.53) * mm});
            skPoint(sketch, "E26.1.0.157", {"position": v(70.51, 60.35) * mm});
            skPoint(sketch, "E26.1.0.158", {"position": v(91.02, 41.44) * mm});
            skPoint(sketch, "E26.1.0.159", {"position": v(80.76, 9.62) * mm});
            skPoint(sketch, "E26.1.0.160", {"position": v(91.02, 75.26) * mm});
            skPoint(sketch, "E26.1.0.161", {"position": v(83.94, 72.38) * mm});
            skPoint(sketch, "E26.1.0.162", {"position": v(119.78, 46.32) * mm});
            skPoint(sketch, "E26.1.0.163", {"position": v(99.27, 63.23) * mm});
            skPoint(sketch, "E26.1.0.164", {"position": v(111.53, 77.26) * mm});
            skPoint(sketch, "E26.1.0.165", {"position": v(70.51, 26.53) * mm});
            skPoint(sketch, "E26.1.0.166", {"position": v(83.94, 41.44) * mm});
            skPoint(sketch, "E26.1.0.167", {"position": v(89.02, 80.14) * mm});
            skLineSegment(sketch, "E26.1.0.168", {"start": v(91.02, 32.98) * mm, "end": v(91.02, 27.53) * mm});
            skPoint(sketch, "E26.1.0.169", {"position": v(83.94, 46.32) * mm});
            skPoint(sketch, "E26.1.0.170", {"position": v(78.77, 72.38) * mm});
            skLineSegment(sketch, "E26.1.0.171", {"start": v(70.51, 91.17) * mm, "end": v(70.51, 85.71) * mm});
            skPoint(sketch, "E26.1.0.172", {"position": v(114.7, 55.47) * mm});
            skPoint(sketch, "E26.1.0.173", {"position": v(89.02, 12.5) * mm});
            skPoint(sketch, "E26.1.0.174", {"position": v(109.53, 72.38) * mm});
            skPoint(sketch, "E26.1.0.175", {"position": v(80.76, 58.35) * mm});
            skPoint(sketch, "E26.1.0.176", {"position": v(89.02, 63.23) * mm});
            skPoint(sketch, "E26.1.0.177", {"position": v(73.69, 21.65) * mm});
            skLineSegment(sketch, "E26.1.0.178", {"start": v(70.51, 32.98) * mm, "end": v(70.51, 27.53) * mm});
            skPoint(sketch, "E26.1.0.179", {"position": v(104.45, 63.23) * mm});
            skPoint(sketch, "E26.1.0.180", {"position": v(119.78, 72.38) * mm});
            skLineSegment(sketch, "E26.1.0.181", {"start": v(91.02, 40.44) * mm, "end": v(91.02, 34.98) * mm});
            skPoint(sketch, "E26.1.0.182", {"position": v(80.76, 75.26) * mm});
            skPoint(sketch, "E26.1.0.183", {"position": v(114.7, 63.23) * mm});
            skPoint(sketch, "E26.1.0.184", {"position": v(91.02, 9.62) * mm});
            skPoint(sketch, "E26.1.0.185", {"position": v(91.02, 58.35) * mm});
            skPoint(sketch, "E26.1.0.186", {"position": v(91.02, 24.53) * mm});
            skPoint(sketch, "E26.1.0.187", {"position": v(114.7, 72.38) * mm});
            skPoint(sketch, "E26.1.0.188", {"position": v(94.2, 41.44) * mm});
            skPoint(sketch, "E26.1.0.189", {"position": v(104.45, 89.29) * mm});
            skLineSegment(sketch, "E26.1.0.190", {"start": v(111.53, 23.53) * mm, "end": v(111.53, 18.07) * mm});
            skLineSegment(sketch, "E26.1.0.191", {"start": v(111.53, 83.71) * mm, "end": v(111.53, 78.26) * mm});
            skLineSegment(sketch, "E26.1.0.192", {"start": v(101.27, 32.98) * mm, "end": v(101.27, 27.53) * mm});
            skPoint(sketch, "E26.1.0.193", {"position": v(73.69, 43.44) * mm});
            skLineSegment(sketch, "E26.1.0.194", {"start": v(101.27, 57.35) * mm, "end": v(101.27, 51.9) * mm});
            skPoint(sketch, "E26.1.0.195", {"position": v(104.45, 60.35) * mm});
            skPoint(sketch, "E26.1.0.196", {"position": v(73.69, 26.53) * mm});
            skLineSegment(sketch, "E26.1.0.197", {"start": v(101.27, 49.9) * mm, "end": v(101.27, 44.44) * mm});
            skLineSegment(sketch, "E26.1.0.198", {"start": v(111.53, 74.26) * mm, "end": v(111.53, 68.8) * mm});
            skPoint(sketch, "E26.1.0.199", {"position": v(83.94, 43.44) * mm});
            skPoint(sketch, "E26.1.0.200", {"position": v(104.45, 77.26) * mm});
            skPoint(sketch, "E26.1.0.201", {"position": v(94.2, 43.44) * mm});
            skLineSegment(sketch, "E26.1.0.202", {"start": v(101.27, 91.17) * mm, "end": v(101.27, 85.71) * mm});
            skLineSegment(sketch, "E26.1.0.203", {"start": v(111.53, 91.17) * mm, "end": v(111.53, 85.71) * mm});
            skLineSegment(sketch, "E26.1.0.204", {"start": v(111.53, 57.35) * mm, "end": v(111.53, 51.9) * mm});
            skPoint(sketch, "E26.1.0.205", {"position": v(114.7, 60.35) * mm});
            skPoint(sketch, "E26.1.0.206", {"position": v(104.45, 26.53) * mm});
            skLineSegment(sketch, "E26.1.0.207", {"start": v(80.76, 16.07) * mm, "end": v(80.76, 10.62) * mm});
            skPoint(sketch, "E26.1.0.208", {"position": v(73.69, 12.5) * mm});
            skPoint(sketch, "E26.1.0.209", {"position": v(104.45, 43.44) * mm});
            skLineSegment(sketch, "E26.1.0.210", {"start": v(101.27, 16.07) * mm, "end": v(101.27, 10.62) * mm});
            skPoint(sketch, "E26.1.0.211", {"position": v(73.69, 77.26) * mm});
            skPoint(sketch, "E26.1.0.212", {"position": v(114.7, 77.26) * mm});
            skPoint(sketch, "E26.1.0.213", {"position": v(101.27, 58.35) * mm});
            skLineSegment(sketch, "E26.1.0.214", {"start": v(80.76, 91.17) * mm, "end": v(80.76, 85.71) * mm});
            skPoint(sketch, "E26.1.0.215", {"position": v(70.51, 24.53) * mm});
            skLineSegment(sketch, "E26.1.0.216", {"start": v(111.53, 16.07) * mm, "end": v(111.53, 10.62) * mm});
            skLineSegment(sketch, "E26.1.0.217", {"start": v(111.53, 49.9) * mm, "end": v(111.53, 44.44) * mm});
            skLineSegment(sketch, "E26.1.0.218", {"start": v(101.27, 66.8) * mm, "end": v(101.27, 61.35) * mm});
            skPoint(sketch, "E26.1.0.219", {"position": v(94.2, 77.26) * mm});
            skLineSegment(sketch, "E26.1.0.220", {"start": v(101.27, 23.53) * mm, "end": v(101.27, 18.07) * mm});
            skLineSegment(sketch, "E26.1.0.221", {"start": v(80.76, 32.98) * mm, "end": v(80.76, 27.53) * mm});
            skLineSegment(sketch, "E26.1.0.222", {"start": v(80.76, 83.71) * mm, "end": v(80.76, 78.26) * mm});
            skPoint(sketch, "E26.1.0.223", {"position": v(83.94, 26.53) * mm});
            skLineSegment(sketch, "E26.1.0.224", {"start": v(70.51, 9.62) * mm, "end": v(70.51, 26.53) * mm, "construction": true});
            skLineSegment(sketch, "E26.1.0.225", {"start": v(101.27, 74.26) * mm, "end": v(101.27, 68.8) * mm});
            skPoint(sketch, "E26.1.0.226", {"position": v(83.94, 21.65) * mm});
            skLineSegment(sketch, "E26.1.0.227", {"start": v(101.27, 40.44) * mm, "end": v(101.27, 34.98) * mm});
            skLineSegment(sketch, "E26.1.0.228", {"start": v(80.76, 57.35) * mm, "end": v(80.76, 51.9) * mm});
            skLineSegment(sketch, "E26.1.0.229", {"start": v(80.76, 40.44) * mm, "end": v(80.76, 34.98) * mm});
            skPoint(sketch, "E26.1.0.230", {"position": v(73.69, 60.35) * mm});
            skPoint(sketch, "E26.1.0.231", {"position": v(94.2, 26.53) * mm});
            skPoint(sketch, "E26.1.0.232", {"position": v(114.7, 43.44) * mm});
            skPoint(sketch, "E26.1.0.233", {"position": v(83.94, 77.26) * mm});
            skPoint(sketch, "E26.1.0.234", {"position": v(83.94, 60.35) * mm});
            skLineSegment(sketch, "E26.1.0.235", {"start": v(111.53, 40.44) * mm, "end": v(111.53, 34.98) * mm});
            skPoint(sketch, "E26.1.0.236", {"position": v(114.7, 26.53) * mm});
            skLineSegment(sketch, "E26.1.0.237", {"start": v(70.51, 9.62) * mm, "end": v(80.76, 9.62) * mm, "construction": true});
            skLineSegment(sketch, "E26.1.0.238", {"start": v(111.53, 66.8) * mm, "end": v(111.53, 61.35) * mm});
            skLineSegment(sketch, "E26.1.0.239", {"start": v(80.76, 74.26) * mm, "end": v(80.76, 68.8) * mm});
            skPoint(sketch, "E26.1.0.240", {"position": v(78.77, 21.65) * mm});
            skPoint(sketch, "E26.1.0.241", {"position": v(101.27, 75.26) * mm});
            skLineSegment(sketch, "E26.1.0.242", {"start": v(80.76, 66.8) * mm, "end": v(80.76, 61.35) * mm});
            skLineSegment(sketch, "E26.1.0.243", {"start": v(80.76, 49.9) * mm, "end": v(80.76, 44.44) * mm});
            skLineSegment(sketch, "E26.1.0.244", {"start": v(101.27, 83.71) * mm, "end": v(101.27, 78.26) * mm});
            skPoint(sketch, "E26.1.0.245", {"position": v(101.27, 24.53) * mm});
            skPoint(sketch, "E26.1.0.246", {"position": v(94.2, 60.35) * mm});
            skPoint(sketch, "E26.1.0.247", {"position": v(101.27, 41.44) * mm});
            skLineSegment(sketch, "E26.1.0.248", {"start": v(111.53, 32.98) * mm, "end": v(111.53, 27.53) * mm});
            skLineSegment(sketch, "E26.1.0.249", {"start": v(121.78, 32.98) * mm, "end": v(121.78, 34.98) * mm});
            skLineSegment(sketch, "E26.1.0.250", {"start": v(119.78, 71.38) * mm, "end": v(119.78, 64.23) * mm});
            skLineSegment(sketch, "E26.1.0.251", {"start": v(80.76, 85.71) * mm, "end": v(78.77, 85.71) * mm});
            skLineSegment(sketch, "E26.1.0.252", {"start": v(119.78, 83.71) * mm, "end": v(119.78, 85.71) * mm});
            skLineSegment(sketch, "E26.1.0.253", {"start": v(78.77, 37.56) * mm, "end": v(78.77, 30.41) * mm});
            skLineSegment(sketch, "E26.1.0.254", {"start": v(89.02, 71.38) * mm, "end": v(89.02, 64.23) * mm});
            skLineSegment(sketch, "E26.1.0.255", {"start": v(119.78, 54.47) * mm, "end": v(119.78, 47.32) * mm});
            skLineSegment(sketch, "E26.1.0.256", {"start": v(80.76, 34.98) * mm, "end": v(78.77, 34.98) * mm});
            skLineSegment(sketch, "E26.1.0.257", {"start": v(99.27, 18.07) * mm, "end": v(99.27, 16.07) * mm});
            skLineSegment(sketch, "E26.1.0.258", {"start": v(111.53, 85.71) * mm, "end": v(109.53, 85.71) * mm});
            skLineSegment(sketch, "E26.1.0.259", {"start": v(119.78, 34.98) * mm, "end": v(121.78, 34.98) * mm});
            skLineSegment(sketch, "E26.1.0.260", {"start": v(68.51, 68.8) * mm, "end": v(68.51, 66.8) * mm});
            skLineSegment(sketch, "E26.1.0.261", {"start": v(101.27, 66.8) * mm, "end": v(99.27, 66.8) * mm});
            skLineSegment(sketch, "E26.1.0.262", {"start": v(91.02, 66.8) * mm, "end": v(89.02, 66.8) * mm});
            skLineSegment(sketch, "E26.1.0.263", {"start": v(119.78, 49.9) * mm, "end": v(121.78, 49.9) * mm});
            skLineSegment(sketch, "E26.1.0.264", {"start": v(119.78, 18.07) * mm, "end": v(121.78, 18.07) * mm});
            skLineSegment(sketch, "E26.1.0.265", {"start": v(99.27, 20.65) * mm, "end": v(99.27, 13.5) * mm});
            skLineSegment(sketch, "E26.1.0.266", {"start": v(70.51, 68.8) * mm, "end": v(68.51, 68.8) * mm});
            skLineSegment(sketch, "E26.1.0.267", {"start": v(119.78, 32.98) * mm, "end": v(119.78, 34.98) * mm});
            skLineSegment(sketch, "E26.1.0.268", {"start": v(99.27, 37.56) * mm, "end": v(99.27, 30.41) * mm});
            skLineSegment(sketch, "E26.1.0.269", {"start": v(119.78, 20.65) * mm, "end": v(119.78, 13.5) * mm});
            skLineSegment(sketch, "E26.1.0.270", {"start": v(101.27, 16.07) * mm, "end": v(99.27, 16.07) * mm});
            skLineSegment(sketch, "E26.1.0.271", {"start": v(121.78, 66.8) * mm, "end": v(121.78, 68.8) * mm});
            skLineSegment(sketch, "E26.1.0.272", {"start": v(109.53, 85.71) * mm, "end": v(109.53, 83.71) * mm});
            skLineSegment(sketch, "E26.1.0.273", {"start": v(91.02, 34.98) * mm, "end": v(89.02, 34.98) * mm});
            skLineSegment(sketch, "E26.1.0.274", {"start": v(80.76, 68.8) * mm, "end": v(78.77, 68.8) * mm});
            skLineSegment(sketch, "E26.1.0.275", {"start": v(119.78, 16.07) * mm, "end": v(121.78, 16.07) * mm});
            skLineSegment(sketch, "E26.1.0.276", {"start": v(101.27, 32.98) * mm, "end": v(99.27, 32.98) * mm});
            skLineSegment(sketch, "E26.1.0.277", {"start": v(101.27, 83.71) * mm, "end": v(99.27, 83.71) * mm});
            skLineSegment(sketch, "E26.1.0.278", {"start": v(99.27, 88.29) * mm, "end": v(99.27, 81.14) * mm});
            skLineSegment(sketch, "E26.1.0.279", {"start": v(78.77, 88.29) * mm, "end": v(78.77, 81.14) * mm});
            skLineSegment(sketch, "E26.1.0.280", {"start": v(91.02, 85.71) * mm, "end": v(89.02, 85.71) * mm});
            skLineSegment(sketch, "E26.1.0.281", {"start": v(80.76, 16.07) * mm, "end": v(78.77, 16.07) * mm});
            skLineSegment(sketch, "E26.1.0.282", {"start": v(101.27, 51.9) * mm, "end": v(99.27, 51.9) * mm});
            skLineSegment(sketch, "E26.1.0.283", {"start": v(91.02, 68.8) * mm, "end": v(89.02, 68.8) * mm});
            skLineSegment(sketch, "E26.1.0.284", {"start": v(111.53, 66.8) * mm, "end": v(109.53, 66.8) * mm});
            skLineSegment(sketch, "E26.1.0.285", {"start": v(89.02, 51.9) * mm, "end": v(89.02, 49.9) * mm});
            skLineSegment(sketch, "E26.1.0.286", {"start": v(70.51, 32.98) * mm, "end": v(68.51, 32.98) * mm});
            skLineSegment(sketch, "E26.1.0.287", {"start": v(119.78, 66.8) * mm, "end": v(121.78, 66.8) * mm});
            skLineSegment(sketch, "E26.1.0.288", {"start": v(119.78, 32.98) * mm, "end": v(121.78, 32.98) * mm});
            skLineSegment(sketch, "E26.1.0.289", {"start": v(80.76, 51.9) * mm, "end": v(78.77, 51.9) * mm});
            skLineSegment(sketch, "E26.1.0.290", {"start": v(109.53, 54.47) * mm, "end": v(109.53, 47.32) * mm});
            skLineSegment(sketch, "E26.1.0.291", {"start": v(101.27, 49.9) * mm, "end": v(99.27, 49.9) * mm});
            skLineSegment(sketch, "E26.1.0.292", {"start": v(99.27, 34.98) * mm, "end": v(99.27, 32.98) * mm});
            skLineSegment(sketch, "E26.1.0.293", {"start": v(119.78, 51.9) * mm, "end": v(121.78, 51.9) * mm});
            skLineSegment(sketch, "E26.1.0.294", {"start": v(99.27, 71.38) * mm, "end": v(99.27, 64.23) * mm});
            skLineSegment(sketch, "E26.1.0.295", {"start": v(80.76, 49.9) * mm, "end": v(78.77, 49.9) * mm});
            skLineSegment(sketch, "E26.1.0.296", {"start": v(111.53, 49.9) * mm, "end": v(109.53, 49.9) * mm});
            skLineSegment(sketch, "E26.1.0.297", {"start": v(121.78, 16.07) * mm, "end": v(121.78, 18.07) * mm});
            skLineSegment(sketch, "E26.1.0.298", {"start": v(99.27, 85.71) * mm, "end": v(99.27, 83.71) * mm});
            skLineSegment(sketch, "E26.1.0.299", {"start": v(91.02, 51.9) * mm, "end": v(89.02, 51.9) * mm});
            skLineSegment(sketch, "E26.1.0.300", {"start": v(109.53, 20.65) * mm, "end": v(109.53, 13.5) * mm});
            skLineSegment(sketch, "E26.1.0.301", {"start": v(70.51, 16.07) * mm, "end": v(70.51, 10.62) * mm});
            skLineSegment(sketch, "E26.1.0.302", {"start": v(109.53, 88.29) * mm, "end": v(109.53, 81.14) * mm});
            skLineSegment(sketch, "E26.1.0.303", {"start": v(91.02, 16.07) * mm, "end": v(89.02, 16.07) * mm});
            skLineSegment(sketch, "E26.1.0.304", {"start": v(68.51, 85.71) * mm, "end": v(68.51, 83.71) * mm});
            skLineSegment(sketch, "E26.1.0.305", {"start": v(70.51, 51.9) * mm, "end": v(68.51, 51.9) * mm});
            skLineSegment(sketch, "E26.1.0.306", {"start": v(70.51, 85.71) * mm, "end": v(68.51, 85.71) * mm});
            skLineSegment(sketch, "E26.1.0.307", {"start": v(119.78, 88.29) * mm, "end": v(119.78, 81.14) * mm});
            skLineSegment(sketch, "E26.1.0.308", {"start": v(91.02, 83.71) * mm, "end": v(89.02, 83.71) * mm});
            skLineSegment(sketch, "E26.1.0.309", {"start": v(68.51, 18.07) * mm, "end": v(68.51, 16.07) * mm});
            skLineSegment(sketch, "E26.1.0.310", {"start": v(78.77, 71.38) * mm, "end": v(78.77, 64.23) * mm});
            skLineSegment(sketch, "E26.1.0.311", {"start": v(70.51, 18.07) * mm, "end": v(68.51, 18.07) * mm});
            skLineSegment(sketch, "E26.1.0.312", {"start": v(111.53, 68.8) * mm, "end": v(109.53, 68.8) * mm});
            skLineSegment(sketch, "E26.1.0.313", {"start": v(101.27, 18.07) * mm, "end": v(99.27, 18.07) * mm});
            skLineSegment(sketch, "E26.1.0.314", {"start": v(109.53, 37.56) * mm, "end": v(109.53, 30.41) * mm});
            skLineSegment(sketch, "E26.1.0.315", {"start": v(68.51, 51.9) * mm, "end": v(68.51, 49.9) * mm});
            skLineSegment(sketch, "E26.1.0.316", {"start": v(111.53, 83.71) * mm, "end": v(109.53, 83.71) * mm});
            skLineSegment(sketch, "E26.1.0.317", {"start": v(89.02, 88.29) * mm, "end": v(89.02, 81.14) * mm});
            skLineSegment(sketch, "E26.1.0.318", {"start": v(70.51, 49.9) * mm, "end": v(68.51, 49.9) * mm});
            skLineSegment(sketch, "E26.1.0.319", {"start": v(80.76, 66.8) * mm, "end": v(78.77, 66.8) * mm});
            skLineSegment(sketch, "E26.1.0.320", {"start": v(91.02, 32.98) * mm, "end": v(89.02, 32.98) * mm});
            skLineSegment(sketch, "E26.1.0.321", {"start": v(111.53, 51.9) * mm, "end": v(109.53, 51.9) * mm});
            skLineSegment(sketch, "E26.1.0.322", {"start": v(111.53, 32.98) * mm, "end": v(109.53, 32.98) * mm});
            skLineSegment(sketch, "E26.1.0.323", {"start": v(70.51, 23.53) * mm, "end": v(70.51, 18.07) * mm});
            skLineSegment(sketch, "E26.1.0.324", {"start": v(119.78, 85.71) * mm, "end": v(121.78, 85.71) * mm});
            skLineSegment(sketch, "E26.1.0.325", {"start": v(101.27, 34.98) * mm, "end": v(99.27, 34.98) * mm});
            skLineSegment(sketch, "E26.1.0.326", {"start": v(121.78, 83.71) * mm, "end": v(121.78, 85.71) * mm});
            skLineSegment(sketch, "E26.1.0.327", {"start": v(78.77, 68.8) * mm, "end": v(78.77, 66.8) * mm});
            skLineSegment(sketch, "E26.1.0.328", {"start": v(91.02, 18.07) * mm, "end": v(89.02, 18.07) * mm});
            skLineSegment(sketch, "E26.1.0.329", {"start": v(109.53, 71.38) * mm, "end": v(109.53, 64.23) * mm});
            skLineSegment(sketch, "E26.1.0.330", {"start": v(80.76, 23.53) * mm, "end": v(80.76, 18.07) * mm});
            skLineSegment(sketch, "E26.1.0.331", {"start": v(111.53, 16.07) * mm, "end": v(109.53, 16.07) * mm});
            skLineSegment(sketch, "E26.1.0.332", {"start": v(70.51, 66.8) * mm, "end": v(68.51, 66.8) * mm});
            skLineSegment(sketch, "E26.1.0.333", {"start": v(70.51, 83.71) * mm, "end": v(68.51, 83.71) * mm});
            skLineSegment(sketch, "E26.1.0.334", {"start": v(99.27, 54.47) * mm, "end": v(99.27, 47.32) * mm});
            skLineSegment(sketch, "E26.1.0.335", {"start": v(101.27, 68.8) * mm, "end": v(99.27, 68.8) * mm});
            skLineSegment(sketch, "E26.1.0.336", {"start": v(109.53, 68.8) * mm, "end": v(109.53, 66.8) * mm});
            skLineSegment(sketch, "E26.1.0.337", {"start": v(70.51, 34.98) * mm, "end": v(68.51, 34.98) * mm});
            skLineSegment(sketch, "E26.1.0.338", {"start": v(78.77, 54.47) * mm, "end": v(78.77, 47.32) * mm});
            skLineSegment(sketch, "E26.1.0.339", {"start": v(119.78, 83.71) * mm, "end": v(121.78, 83.71) * mm});
            skLineSegment(sketch, "E26.1.0.340", {"start": v(119.78, 68.8) * mm, "end": v(121.78, 68.8) * mm});
            skLineSegment(sketch, "E26.1.0.341", {"start": v(80.76, 83.71) * mm, "end": v(78.77, 83.71) * mm});
            skLineSegment(sketch, "E26.1.0.342", {"start": v(119.78, 16.07) * mm, "end": v(119.78, 18.07) * mm});
            skLineSegment(sketch, "E26.1.0.343", {"start": v(89.02, 37.56) * mm, "end": v(89.02, 30.41) * mm});
            skLineSegment(sketch, "E26.1.0.344", {"start": v(109.53, 18.07) * mm, "end": v(109.53, 16.07) * mm});
            skLineSegment(sketch, "E26.1.0.345", {"start": v(101.27, 85.71) * mm, "end": v(99.27, 85.71) * mm});
            skLineSegment(sketch, "E26.1.0.346", {"start": v(89.02, 34.98) * mm, "end": v(89.02, 32.98) * mm});
            skLineSegment(sketch, "E26.1.0.347", {"start": v(80.76, 32.98) * mm, "end": v(78.77, 32.98) * mm});
            skLineSegment(sketch, "E26.1.0.348", {"start": v(111.53, 18.07) * mm, "end": v(109.53, 18.07) * mm});
            skLineSegment(sketch, "E26.1.0.349", {"start": v(121.78, 49.9) * mm, "end": v(121.78, 51.9) * mm});
            skLineSegment(sketch, "E26.1.0.350", {"start": v(89.02, 20.65) * mm, "end": v(89.02, 13.5) * mm});
            skLineSegment(sketch, "E26.1.0.351", {"start": v(89.02, 54.47) * mm, "end": v(89.02, 47.32) * mm});
            skLineSegment(sketch, "E26.1.0.352", {"start": v(78.77, 51.9) * mm, "end": v(78.77, 49.9) * mm});
            skLineSegment(sketch, "E26.1.0.353", {"start": v(111.53, 34.98) * mm, "end": v(109.53, 34.98) * mm});
            skLineSegment(sketch, "E26.1.0.354", {"start": v(91.02, 49.9) * mm, "end": v(89.02, 49.9) * mm});
            skLineSegment(sketch, "E26.1.0.355", {"start": v(68.51, 34.98) * mm, "end": v(68.51, 32.98) * mm});
            skLineSegment(sketch, "E26.1.0.356", {"start": v(119.78, 37.56) * mm, "end": v(119.78, 30.41) * mm});
            skLineSegment(sketch, "E26.1.0.357", {"start": v(119.78, 66.8) * mm, "end": v(119.78, 68.8) * mm});
            skLineSegment(sketch, "E26.1.0.358", {"start": v(119.78, 49.9) * mm, "end": v(119.78, 51.9) * mm});
            skArc(sketch, "E26.1.0.359", {"start": v(70.51, 44.44) * mm, "mid": v(70.8, 43.73) * mm, "end": v(71.51, 43.44) * mm});
            skArc(sketch, "E26.1.0.360", {"start": v(89.02, 88.29) * mm, "mid": v(88.73, 89) * mm, "end": v(88.02, 89.29) * mm});
            skLineSegment(sketch, "E26.1.0.361", {"start": v(109.53, 34.98) * mm, "end": v(109.53, 32.98) * mm});
            skArc(sketch, "E26.1.0.362", {"start": v(94.2, 22.15) * mm, "mid": v(94.34, 21.8) * mm, "end": v(94.7, 21.65) * mm});
            skArc(sketch, "E26.1.0.363", {"start": v(78.77, 54.47) * mm, "mid": v(78.47, 55.17) * mm, "end": v(77.77, 55.47) * mm});
            skLineSegment(sketch, "E26.1.0.364", {"start": v(94.7, 89.29) * mm, "end": v(98.27, 89.29) * mm});
            skLineSegment(sketch, "E26.1.0.365", {"start": v(115.2, 21.65) * mm, "end": v(118.78, 21.65) * mm});
            skLineSegment(sketch, "E26.1.0.366", {"start": v(74.19, 89.29) * mm, "end": v(77.77, 89.29) * mm});
            skLineSegment(sketch, "E26.1.0.367", {"start": v(114.7, 12) * mm, "end": v(114.7, 10.62) * mm});
            skArc(sketch, "E26.1.0.368", {"start": v(77.77, 46.32) * mm, "mid": v(78.47, 46.62) * mm, "end": v(78.77, 47.32) * mm});
            skArc(sketch, "E26.1.0.369", {"start": v(99.27, 37.56) * mm, "mid": v(98.98, 38.26) * mm, "end": v(98.27, 38.56) * mm});
            skLineSegment(sketch, "E26.1.0.370", {"start": v(94.7, 46.32) * mm, "end": v(98.27, 46.32) * mm});
            skArc(sketch, "E26.1.0.371", {"start": v(80.76, 10.62) * mm, "mid": v(81.06, 9.91) * mm, "end": v(81.76, 9.62) * mm});
            skArc(sketch, "E26.1.0.372", {"start": v(77.77, 29.41) * mm, "mid": v(78.47, 29.7) * mm, "end": v(78.77, 30.41) * mm});
            skLineSegment(sketch, "E26.1.0.373", {"start": v(94.7, 55.47) * mm, "end": v(98.27, 55.47) * mm});
            skArc(sketch, "E26.1.0.374", {"start": v(112.53, 24.53) * mm, "mid": v(111.82, 24.24) * mm, "end": v(111.53, 23.53) * mm});
            skArc(sketch, "E26.1.0.375", {"start": v(108.53, 80.14) * mm, "mid": v(109.23, 80.44) * mm, "end": v(109.53, 81.14) * mm});
            skLineSegment(sketch, "E26.1.0.376", {"start": v(115.2, 46.32) * mm, "end": v(118.78, 46.32) * mm});
            skArc(sketch, "E26.1.0.377", {"start": v(104.95, 63.23) * mm, "mid": v(104.6, 63.09) * mm, "end": v(104.45, 62.73) * mm});
            skArc(sketch, "E26.1.0.378", {"start": v(89.02, 37.56) * mm, "mid": v(88.73, 38.26) * mm, "end": v(88.02, 38.56) * mm});
            skArc(sketch, "E26.1.0.379", {"start": v(119.78, 71.38) * mm, "mid": v(119.49, 72.08) * mm, "end": v(118.78, 72.38) * mm});
            skLineSegment(sketch, "E26.1.0.380", {"start": v(94.2, 12) * mm, "end": v(94.2, 10.62) * mm});
            skLineSegment(sketch, "E26.1.0.381", {"start": v(70.51, 16.07) * mm, "end": v(68.51, 16.07) * mm});
            skArc(sketch, "E26.1.0.382", {"start": v(78.77, 37.56) * mm, "mid": v(78.47, 38.26) * mm, "end": v(77.77, 38.56) * mm});
            skArc(sketch, "E26.1.0.383", {"start": v(92.02, 58.35) * mm, "mid": v(91.31, 58.06) * mm, "end": v(91.02, 57.35) * mm});
            skLineSegment(sketch, "E26.1.0.384", {"start": v(104.95, 63.23) * mm, "end": v(108.53, 63.23) * mm});
            skArc(sketch, "E26.1.0.385", {"start": v(88.02, 29.41) * mm, "mid": v(88.73, 29.7) * mm, "end": v(89.02, 30.41) * mm});
            skArc(sketch, "E26.1.0.386", {"start": v(89.02, 54.47) * mm, "mid": v(88.73, 55.17) * mm, "end": v(88.02, 55.47) * mm});
            skArc(sketch, "E26.1.0.387", {"start": v(115.2, 63.23) * mm, "mid": v(114.85, 63.09) * mm, "end": v(114.7, 62.73) * mm});
            skArc(sketch, "E26.1.0.388", {"start": v(81.76, 75.26) * mm, "mid": v(81.06, 74.97) * mm, "end": v(80.76, 74.26) * mm});
            skArc(sketch, "E26.1.0.389", {"start": v(91.02, 61.35) * mm, "mid": v(91.31, 60.64) * mm, "end": v(92.02, 60.35) * mm});
            skLineSegment(sketch, "E26.1.0.390", {"start": v(84.44, 21.65) * mm, "end": v(88.02, 21.65) * mm});
            skLineSegment(sketch, "E26.1.0.391", {"start": v(115.2, 38.56) * mm, "end": v(118.78, 38.56) * mm});
            skLineSegment(sketch, "E26.1.0.392", {"start": v(92.02, 92.17) * mm, "end": v(93.2, 92.17) * mm});
            skArc(sketch, "E26.1.0.393", {"start": v(91.02, 78.26) * mm, "mid": v(91.31, 77.55) * mm, "end": v(92.02, 77.26) * mm});
            skArc(sketch, "E26.1.0.394", {"start": v(98.27, 63.23) * mm, "mid": v(98.98, 63.53) * mm, "end": v(99.27, 64.23) * mm});
            skArc(sketch, "E26.1.0.395", {"start": v(74.19, 63.23) * mm, "mid": v(73.83, 63.09) * mm, "end": v(73.69, 62.73) * mm});
            skLineSegment(sketch, "E26.1.0.396", {"start": v(71.51, 92.17) * mm, "end": v(72.69, 92.17) * mm});
            skArc(sketch, "E26.1.0.397", {"start": v(94.7, 63.23) * mm, "mid": v(94.34, 63.09) * mm, "end": v(94.2, 62.73) * mm});
            skLineSegment(sketch, "E26.1.0.398", {"start": v(78.77, 85.71) * mm, "end": v(78.77, 83.71) * mm});
            skArc(sketch, "E26.1.0.399", {"start": v(94.7, 29.41) * mm, "mid": v(94.34, 29.27) * mm, "end": v(94.2, 28.91) * mm});
            skLineSegment(sketch, "E26.1.0.400", {"start": v(115.2, 55.47) * mm, "end": v(118.78, 55.47) * mm});
            skLineSegment(sketch, "E26.1.0.401", {"start": v(74.19, 63.23) * mm, "end": v(77.77, 63.23) * mm});
            skArc(sketch, "E26.1.0.402", {"start": v(70.51, 61.35) * mm, "mid": v(70.8, 60.64) * mm, "end": v(71.51, 60.35) * mm});
            skArc(sketch, "E26.1.0.403", {"start": v(93.2, 9.62) * mm, "mid": v(93.9, 9.91) * mm, "end": v(94.2, 10.62) * mm});
            skArc(sketch, "E26.1.0.404", {"start": v(83.94, 89.79) * mm, "mid": v(84.09, 89.43) * mm, "end": v(84.44, 89.29) * mm});
            skLineSegment(sketch, "E26.1.0.405", {"start": v(84.44, 29.41) * mm, "end": v(88.02, 29.41) * mm});
            skArc(sketch, "E26.1.0.406", {"start": v(119.78, 54.47) * mm, "mid": v(119.49, 55.17) * mm, "end": v(118.78, 55.47) * mm});
            skArc(sketch, "E26.1.0.407", {"start": v(115.2, 46.32) * mm, "mid": v(114.85, 46.18) * mm, "end": v(114.7, 45.82) * mm});
            skArc(sketch, "E26.1.0.408", {"start": v(103.45, 9.62) * mm, "mid": v(104.15, 9.91) * mm, "end": v(104.45, 10.62) * mm});
            skArc(sketch, "E26.1.0.409", {"start": v(109.53, 88.29) * mm, "mid": v(109.23, 89) * mm, "end": v(108.53, 89.29) * mm});
            skArc(sketch, "E26.1.0.410", {"start": v(112.53, 92.17) * mm, "mid": v(111.82, 91.88) * mm, "end": v(111.53, 91.17) * mm});
            skArc(sketch, "E26.1.0.411", {"start": v(80.76, 44.44) * mm, "mid": v(81.06, 43.73) * mm, "end": v(81.76, 43.44) * mm});
            skArc(sketch, "E26.1.0.412", {"start": v(92.02, 92.17) * mm, "mid": v(91.31, 91.88) * mm, "end": v(91.02, 91.17) * mm});
            skLineSegment(sketch, "E26.1.0.413", {"start": v(104.45, 12) * mm, "end": v(104.45, 10.62) * mm});
            skLineSegment(sketch, "E26.1.0.414", {"start": v(104.95, 46.32) * mm, "end": v(108.53, 46.32) * mm});
            skArc(sketch, "E26.1.0.415", {"start": v(109.53, 71.38) * mm, "mid": v(109.23, 72.08) * mm, "end": v(108.53, 72.38) * mm});
            skLineSegment(sketch, "E26.1.0.416", {"start": v(104.95, 12.5) * mm, "end": v(108.53, 12.5) * mm});
            skArc(sketch, "E26.1.0.417", {"start": v(114.7, 22.15) * mm, "mid": v(114.85, 21.8) * mm, "end": v(115.2, 21.65) * mm});
            skLineSegment(sketch, "E26.1.0.418", {"start": v(115.2, 89.29) * mm, "end": v(118.78, 89.29) * mm});
            skArc(sketch, "E26.1.0.419", {"start": v(89.02, 71.38) * mm, "mid": v(88.73, 72.08) * mm, "end": v(88.02, 72.38) * mm});
            skArc(sketch, "E26.1.0.420", {"start": v(94.2, 89.79) * mm, "mid": v(94.34, 89.43) * mm, "end": v(94.7, 89.29) * mm});
            skArc(sketch, "E26.1.0.421", {"start": v(115.2, 29.41) * mm, "mid": v(114.85, 29.27) * mm, "end": v(114.7, 28.91) * mm});
            skArc(sketch, "E26.1.0.422", {"start": v(93.2, 60.35) * mm, "mid": v(93.9, 60.64) * mm, "end": v(94.2, 61.35) * mm});
            skArc(sketch, "E26.1.0.423", {"start": v(78.77, 71.38) * mm, "mid": v(78.47, 72.08) * mm, "end": v(77.77, 72.38) * mm});
            skLineSegment(sketch, "E26.1.0.424", {"start": v(74.19, 80.14) * mm, "end": v(77.77, 80.14) * mm});
            skLineSegment(sketch, "E26.1.0.425", {"start": v(74.19, 46.32) * mm, "end": v(77.77, 46.32) * mm});
            skArc(sketch, "E26.1.0.426", {"start": v(115.2, 12.5) * mm, "mid": v(114.85, 12.36) * mm, "end": v(114.7, 12) * mm});
            skLineSegment(sketch, "E26.1.0.427", {"start": v(81.76, 9.62) * mm, "end": v(82.94, 9.62) * mm});
            skArc(sketch, "E26.1.0.428", {"start": v(119.78, 20.65) * mm, "mid": v(119.49, 21.35) * mm, "end": v(118.78, 21.65) * mm});
            skLineSegment(sketch, "E26.1.0.429", {"start": v(115.2, 12.5) * mm, "end": v(118.78, 12.5) * mm});
            skLineSegment(sketch, "E26.1.0.430", {"start": v(94.7, 29.41) * mm, "end": v(98.27, 29.41) * mm});
            skLineSegment(sketch, "E26.1.0.431", {"start": v(94.7, 80.14) * mm, "end": v(98.27, 80.14) * mm});
            skArc(sketch, "E26.1.0.432", {"start": v(81.76, 92.17) * mm, "mid": v(81.06, 91.88) * mm, "end": v(80.76, 91.17) * mm});
            skLineSegment(sketch, "E26.1.0.433", {"start": v(104.95, 21.65) * mm, "end": v(108.53, 21.65) * mm});
            skArc(sketch, "E26.1.0.434", {"start": v(98.27, 12.5) * mm, "mid": v(98.98, 12.8) * mm, "end": v(99.27, 13.5) * mm});
            skArc(sketch, "E26.1.0.435", {"start": v(119.78, 37.56) * mm, "mid": v(119.49, 38.26) * mm, "end": v(118.78, 38.56) * mm});
            skArc(sketch, "E26.1.0.436", {"start": v(88.02, 12.5) * mm, "mid": v(88.73, 12.8) * mm, "end": v(89.02, 13.5) * mm});
            skLineSegment(sketch, "E26.1.0.437", {"start": v(104.45, 79.64) * mm, "end": v(104.45, 78.26) * mm});
            skArc(sketch, "E26.1.0.438", {"start": v(73.69, 22.15) * mm, "mid": v(73.83, 21.8) * mm, "end": v(74.19, 21.65) * mm});
            skLineSegment(sketch, "E26.1.0.439", {"start": v(104.95, 29.41) * mm, "end": v(108.53, 29.41) * mm});
            skArc(sketch, "E26.1.0.440", {"start": v(98.27, 46.32) * mm, "mid": v(98.98, 46.62) * mm, "end": v(99.27, 47.32) * mm});
            skLineSegment(sketch, "E26.1.0.441", {"start": v(99.27, 68.8) * mm, "end": v(99.27, 66.8) * mm});
            skLineSegment(sketch, "E26.1.0.442", {"start": v(94.7, 21.65) * mm, "end": v(98.27, 21.65) * mm});
            skArc(sketch, "E26.1.0.443", {"start": v(104.45, 91.17) * mm, "mid": v(104.15, 91.88) * mm, "end": v(103.45, 92.17) * mm});
            skArc(sketch, "E26.1.0.444", {"start": v(118.78, 29.41) * mm, "mid": v(119.49, 29.7) * mm, "end": v(119.78, 30.41) * mm});
            skArc(sketch, "E26.1.0.445", {"start": v(108.53, 12.5) * mm, "mid": v(109.23, 12.8) * mm, "end": v(109.53, 13.5) * mm});
            skArc(sketch, "E26.1.0.446", {"start": v(73.69, 91.17) * mm, "mid": v(73.4, 91.88) * mm, "end": v(72.69, 92.17) * mm});
            skArc(sketch, "E26.1.0.447", {"start": v(70.51, 10.62) * mm, "mid": v(70.8, 9.91) * mm, "end": v(71.51, 9.62) * mm});
            skLineSegment(sketch, "E26.1.0.448", {"start": v(83.94, 45.82) * mm, "end": v(83.94, 44.44) * mm});
            skLineSegment(sketch, "E26.1.0.449", {"start": v(92.02, 75.26) * mm, "end": v(93.2, 75.26) * mm});
            skArc(sketch, "E26.1.0.450", {"start": v(108.53, 29.41) * mm, "mid": v(109.23, 29.7) * mm, "end": v(109.53, 30.41) * mm});
            skArc(sketch, "E26.1.0.451", {"start": v(88.02, 63.23) * mm, "mid": v(88.73, 63.53) * mm, "end": v(89.02, 64.23) * mm});
            skArc(sketch, "E26.1.0.452", {"start": v(78.77, 88.29) * mm, "mid": v(78.47, 89) * mm, "end": v(77.77, 89.29) * mm});
            skArc(sketch, "E26.1.0.453", {"start": v(99.27, 54.47) * mm, "mid": v(98.98, 55.17) * mm, "end": v(98.27, 55.47) * mm});
            skLineSegment(sketch, "E26.1.0.454", {"start": v(78.77, 20.65) * mm, "end": v(78.77, 13.5) * mm});
            skLineSegment(sketch, "E26.1.0.455", {"start": v(92.02, 9.62) * mm, "end": v(93.2, 9.62) * mm});
            skLineSegment(sketch, "E26.1.0.456", {"start": v(112.53, 92.17) * mm, "end": v(113.7, 92.17) * mm});
            skLineSegment(sketch, "E26.1.0.457", {"start": v(115.2, 29.41) * mm, "end": v(118.78, 29.41) * mm});
            skArc(sketch, "E26.1.0.458", {"start": v(109.53, 54.47) * mm, "mid": v(109.23, 55.17) * mm, "end": v(108.53, 55.47) * mm});
            skArc(sketch, "E26.1.0.459", {"start": v(92.02, 75.26) * mm, "mid": v(91.31, 74.97) * mm, "end": v(91.02, 74.26) * mm});
            skArc(sketch, "E26.1.0.460", {"start": v(118.78, 12.5) * mm, "mid": v(119.49, 12.8) * mm, "end": v(119.78, 13.5) * mm});
            skLineSegment(sketch, "E26.1.0.461", {"start": v(102.27, 9.62) * mm, "end": v(103.45, 9.62) * mm});
            skLineSegment(sketch, "E26.1.0.462", {"start": v(115.2, 63.23) * mm, "end": v(118.78, 63.23) * mm});
            skLineSegment(sketch, "E26.1.0.463", {"start": v(94.7, 38.56) * mm, "end": v(98.27, 38.56) * mm});
            skArc(sketch, "E26.1.0.464", {"start": v(114.7, 91.17) * mm, "mid": v(114.4, 91.88) * mm, "end": v(113.7, 92.17) * mm});
            skArc(sketch, "E26.1.0.465", {"start": v(84.44, 46.32) * mm, "mid": v(84.09, 46.18) * mm, "end": v(83.94, 45.82) * mm});
            skArc(sketch, "E26.1.0.466", {"start": v(109.53, 20.65) * mm, "mid": v(109.23, 21.35) * mm, "end": v(108.53, 21.65) * mm});
            skArc(sketch, "E26.1.0.467", {"start": v(108.53, 46.32) * mm, "mid": v(109.23, 46.62) * mm, "end": v(109.53, 47.32) * mm});
            skArc(sketch, "E26.1.0.468", {"start": v(71.51, 75.26) * mm, "mid": v(70.8, 74.97) * mm, "end": v(70.51, 74.26) * mm});
            skArc(sketch, "E26.1.0.469", {"start": v(82.94, 9.62) * mm, "mid": v(83.65, 9.91) * mm, "end": v(83.94, 10.62) * mm});
            skArc(sketch, "E26.1.0.470", {"start": v(94.7, 12.5) * mm, "mid": v(94.34, 12.36) * mm, "end": v(94.2, 12) * mm});
            skArc(sketch, "E26.1.0.471", {"start": v(115.2, 80.14) * mm, "mid": v(114.85, 80) * mm, "end": v(114.7, 79.64) * mm});
            skArc(sketch, "E26.1.0.472", {"start": v(91.02, 10.62) * mm, "mid": v(91.31, 9.91) * mm, "end": v(92.02, 9.62) * mm});
            skLineSegment(sketch, "E26.1.0.473", {"start": v(84.44, 55.47) * mm, "end": v(88.02, 55.47) * mm});
            skArc(sketch, "E26.1.0.474", {"start": v(113.7, 9.62) * mm, "mid": v(114.4, 9.91) * mm, "end": v(114.7, 10.62) * mm});
            skLineSegment(sketch, "E26.1.0.475", {"start": v(78.77, 34.98) * mm, "end": v(78.77, 32.98) * mm});
            skArc(sketch, "E26.1.0.476", {"start": v(77.77, 12.5) * mm, "mid": v(78.47, 12.8) * mm, "end": v(78.77, 13.5) * mm});
            skArc(sketch, "E26.1.0.477", {"start": v(84.44, 12.5) * mm, "mid": v(84.09, 12.36) * mm, "end": v(83.94, 12) * mm});
            skLineSegment(sketch, "E26.1.0.478", {"start": v(115.2, 72.38) * mm, "end": v(118.78, 72.38) * mm});
            skLineSegment(sketch, "E26.1.0.479", {"start": v(83.94, 91.17) * mm, "end": v(83.94, 89.79) * mm});
            skArc(sketch, "E26.1.0.480", {"start": v(104.95, 12.5) * mm, "mid": v(104.6, 12.36) * mm, "end": v(104.45, 12) * mm});
            skLineSegment(sketch, "E26.1.0.481", {"start": v(89.02, 85.71) * mm, "end": v(89.02, 83.71) * mm});
            skLineSegment(sketch, "E26.1.0.482", {"start": v(114.7, 91.17) * mm, "end": v(114.7, 89.79) * mm});
            skArc(sketch, "E26.1.0.483", {"start": v(88.02, 80.14) * mm, "mid": v(88.73, 80.44) * mm, "end": v(89.02, 81.14) * mm});
            skArc(sketch, "E26.1.0.484", {"start": v(74.19, 46.32) * mm, "mid": v(73.83, 46.18) * mm, "end": v(73.69, 45.82) * mm});
            skLineSegment(sketch, "E26.1.0.485", {"start": v(74.19, 72.38) * mm, "end": v(77.77, 72.38) * mm});
            skArc(sketch, "E26.1.0.486", {"start": v(83.94, 91.17) * mm, "mid": v(83.65, 91.88) * mm, "end": v(82.94, 92.17) * mm});
            skLineSegment(sketch, "E26.1.0.487", {"start": v(74.19, 55.47) * mm, "end": v(77.77, 55.47) * mm});
            skLineSegment(sketch, "E26.1.0.488", {"start": v(99.27, 51.9) * mm, "end": v(99.27, 49.9) * mm});
            skArc(sketch, "E26.1.0.489", {"start": v(109.53, 37.56) * mm, "mid": v(109.23, 38.26) * mm, "end": v(108.53, 38.56) * mm});
            skLineSegment(sketch, "E26.1.0.490", {"start": v(74.19, 12.5) * mm, "end": v(77.77, 12.5) * mm});
            skLineSegment(sketch, "E26.1.0.491", {"start": v(94.2, 62.73) * mm, "end": v(94.2, 61.35) * mm});
            skArc(sketch, "E26.1.0.492", {"start": v(88.02, 46.32) * mm, "mid": v(88.73, 46.62) * mm, "end": v(89.02, 47.32) * mm});
            skArc(sketch, "E26.1.0.493", {"start": v(89.02, 20.65) * mm, "mid": v(88.73, 21.35) * mm, "end": v(88.02, 21.65) * mm});
            skLineSegment(sketch, "E26.1.0.494", {"start": v(84.44, 46.32) * mm, "end": v(88.02, 46.32) * mm});
            skArc(sketch, "E26.1.0.495", {"start": v(99.27, 20.65) * mm, "mid": v(98.98, 21.35) * mm, "end": v(98.27, 21.65) * mm});
            skLineSegment(sketch, "E26.1.0.496", {"start": v(114.7, 62.73) * mm, "end": v(114.7, 61.35) * mm});
            skArc(sketch, "E26.1.0.497", {"start": v(98.27, 80.14) * mm, "mid": v(98.98, 80.44) * mm, "end": v(99.27, 81.14) * mm});
            skArc(sketch, "E26.1.0.498", {"start": v(104.95, 80.14) * mm, "mid": v(104.6, 80) * mm, "end": v(104.45, 79.64) * mm});
            skArc(sketch, "E26.1.0.499", {"start": v(118.78, 46.32) * mm, "mid": v(119.49, 46.62) * mm, "end": v(119.78, 47.32) * mm});
            skArc(sketch, "E26.1.0.500", {"start": v(118.78, 80.14) * mm, "mid": v(119.49, 80.44) * mm, "end": v(119.78, 81.14) * mm});
            skArc(sketch, "E26.1.0.501", {"start": v(104.45, 89.79) * mm, "mid": v(104.6, 89.43) * mm, "end": v(104.95, 89.29) * mm});
            skArc(sketch, "E26.1.0.502", {"start": v(104.45, 22.15) * mm, "mid": v(104.6, 21.8) * mm, "end": v(104.95, 21.65) * mm});
            skArc(sketch, "E26.1.0.503", {"start": v(119.78, 88.29) * mm, "mid": v(119.49, 89) * mm, "end": v(118.78, 89.29) * mm});
            skArc(sketch, "E26.1.0.504", {"start": v(70.51, 78.26) * mm, "mid": v(70.8, 77.55) * mm, "end": v(71.51, 77.26) * mm});
            skLineSegment(sketch, "E26.1.0.505", {"start": v(104.95, 72.38) * mm, "end": v(108.53, 72.38) * mm});
            skLineSegment(sketch, "E26.1.0.506", {"start": v(84.44, 80.14) * mm, "end": v(88.02, 80.14) * mm});
            skLineSegment(sketch, "E26.1.0.507", {"start": v(92.02, 77.26) * mm, "end": v(93.2, 77.26) * mm});
            skArc(sketch, "E26.1.0.508", {"start": v(98.27, 29.41) * mm, "mid": v(98.98, 29.7) * mm, "end": v(99.27, 30.41) * mm});
            skLineSegment(sketch, "E26.1.0.509", {"start": v(80.76, 18.07) * mm, "end": v(78.77, 18.07) * mm});
            skLineSegment(sketch, "E26.1.0.510", {"start": v(104.95, 89.29) * mm, "end": v(108.53, 89.29) * mm});
            skLineSegment(sketch, "E26.1.0.511", {"start": v(83.94, 12) * mm, "end": v(83.94, 10.62) * mm});
            skLineSegment(sketch, "E26.1.0.512", {"start": v(94.7, 63.23) * mm, "end": v(98.27, 63.23) * mm});
            skArc(sketch, "E26.1.0.513", {"start": v(118.78, 63.23) * mm, "mid": v(119.49, 63.53) * mm, "end": v(119.78, 64.23) * mm});
            skLineSegment(sketch, "E26.1.0.514", {"start": v(84.44, 63.23) * mm, "end": v(88.02, 63.23) * mm});
            skLineSegment(sketch, "E26.1.0.515", {"start": v(94.7, 72.38) * mm, "end": v(98.27, 72.38) * mm});
            skArc(sketch, "E26.1.0.516", {"start": v(114.7, 89.79) * mm, "mid": v(114.85, 89.43) * mm, "end": v(115.2, 89.29) * mm});
            skArc(sketch, "E26.1.0.517", {"start": v(77.77, 63.23) * mm, "mid": v(78.47, 63.53) * mm, "end": v(78.77, 64.23) * mm});
            skLineSegment(sketch, "E26.1.0.518", {"start": v(94.2, 91.17) * mm, "end": v(94.2, 89.79) * mm});
            skLineSegment(sketch, "E26.1.0.519", {"start": v(109.53, 51.9) * mm, "end": v(109.53, 49.9) * mm});
            skLineSegment(sketch, "E26.1.0.520", {"start": v(84.44, 12.5) * mm, "end": v(88.02, 12.5) * mm});
            skLineSegment(sketch, "E26.1.0.521", {"start": v(104.95, 38.56) * mm, "end": v(108.53, 38.56) * mm});
            skArc(sketch, "E26.1.0.522", {"start": v(84.44, 29.41) * mm, "mid": v(84.09, 29.27) * mm, "end": v(83.94, 28.91) * mm});
            skArc(sketch, "E26.1.0.523", {"start": v(108.53, 63.23) * mm, "mid": v(109.23, 63.53) * mm, "end": v(109.53, 64.23) * mm});
            skLineSegment(sketch, "E26.1.0.524", {"start": v(74.19, 29.41) * mm, "end": v(77.77, 29.41) * mm});
            skLineSegment(sketch, "E26.1.0.525", {"start": v(73.69, 62.73) * mm, "end": v(73.69, 61.35) * mm});
            skLineSegment(sketch, "E26.1.0.526", {"start": v(92.02, 60.35) * mm, "end": v(93.2, 60.35) * mm});
            skArc(sketch, "E26.1.0.527", {"start": v(94.2, 91.17) * mm, "mid": v(93.9, 91.88) * mm, "end": v(93.2, 92.17) * mm});
            skLineSegment(sketch, "E26.1.0.528", {"start": v(94.7, 12.5) * mm, "end": v(98.27, 12.5) * mm});
            skArc(sketch, "E26.1.0.529", {"start": v(91.02, 44.44) * mm, "mid": v(91.31, 43.73) * mm, "end": v(92.02, 43.44) * mm});
            skArc(sketch, "E26.1.0.530", {"start": v(101.27, 10.62) * mm, "mid": v(101.57, 9.91) * mm, "end": v(102.27, 9.62) * mm});
            skArc(sketch, "E26.1.0.531", {"start": v(71.51, 41.44) * mm, "mid": v(70.8, 41.15) * mm, "end": v(70.51, 40.44) * mm});
            skLineSegment(sketch, "E26.1.0.532", {"start": v(89.02, 18.07) * mm, "end": v(89.02, 16.07) * mm});
            skArc(sketch, "E26.1.0.533", {"start": v(71.51, 92.17) * mm, "mid": v(70.8, 91.88) * mm, "end": v(70.51, 91.17) * mm});
            skLineSegment(sketch, "E26.1.0.534", {"start": v(74.19, 21.65) * mm, "end": v(77.77, 21.65) * mm});
            skLineSegment(sketch, "E26.1.0.535", {"start": v(81.76, 92.17) * mm, "end": v(82.94, 92.17) * mm});
            skLineSegment(sketch, "E26.1.0.536", {"start": v(78.77, 18.07) * mm, "end": v(78.77, 16.07) * mm});
            skLineSegment(sketch, "E26.1.0.537", {"start": v(104.45, 91.17) * mm, "end": v(104.45, 89.79) * mm});
            skLineSegment(sketch, "E26.1.0.538", {"start": v(115.2, 80.14) * mm, "end": v(118.78, 80.14) * mm});
            skLineSegment(sketch, "E26.1.0.539", {"start": v(84.44, 89.29) * mm, "end": v(88.02, 89.29) * mm});
            skLineSegment(sketch, "E26.1.0.540", {"start": v(84.44, 38.56) * mm, "end": v(88.02, 38.56) * mm});
            skArc(sketch, "E26.1.0.541", {"start": v(77.77, 80.14) * mm, "mid": v(78.47, 80.44) * mm, "end": v(78.77, 81.14) * mm});
            skLineSegment(sketch, "E26.1.0.542", {"start": v(104.95, 55.47) * mm, "end": v(108.53, 55.47) * mm});
            skLineSegment(sketch, "E26.1.0.543", {"start": v(73.69, 91.17) * mm, "end": v(73.69, 89.79) * mm});
            skLineSegment(sketch, "E26.1.0.544", {"start": v(104.95, 80.14) * mm, "end": v(108.53, 80.14) * mm});
            skArc(sketch, "E26.1.0.545", {"start": v(99.27, 88.29) * mm, "mid": v(98.98, 89) * mm, "end": v(98.27, 89.29) * mm});
            skLineSegment(sketch, "E26.1.0.546", {"start": v(84.44, 72.38) * mm, "end": v(88.02, 72.38) * mm});
            skArc(sketch, "E26.1.0.547", {"start": v(84.44, 63.23) * mm, "mid": v(84.09, 63.09) * mm, "end": v(83.94, 62.73) * mm});
            skLineSegment(sketch, "E26.1.0.548", {"start": v(74.19, 38.56) * mm, "end": v(77.77, 38.56) * mm});
            skLineSegment(sketch, "E26.1.0.549", {"start": v(89.02, 68.8) * mm, "end": v(89.02, 66.8) * mm});
            skArc(sketch, "E26.1.0.550", {"start": v(99.27, 71.38) * mm, "mid": v(98.98, 72.08) * mm, "end": v(98.27, 72.38) * mm});
            skArc(sketch, "E26.1.0.551", {"start": v(83.94, 23.53) * mm, "mid": v(83.65, 24.24) * mm, "end": v(82.94, 24.53) * mm});
            skLineSegment(sketch, "E26.1.0.552", {"start": v(112.53, 9.62) * mm, "end": v(113.7, 9.62) * mm});
            skArc(sketch, "E26.1.0.553", {"start": v(102.27, 75.26) * mm, "mid": v(101.57, 74.97) * mm, "end": v(101.27, 74.26) * mm});
            skLineSegment(sketch, "E26.1.0.554", {"start": v(81.76, 58.35) * mm, "end": v(82.94, 58.35) * mm});
            skLineSegment(sketch, "E26.1.0.555", {"start": v(104.45, 23.53) * mm, "end": v(104.45, 22.15) * mm});
            skArc(sketch, "E26.1.0.556", {"start": v(72.69, 43.44) * mm, "mid": v(73.4, 43.73) * mm, "end": v(73.69, 44.44) * mm});
            skArc(sketch, "E26.1.0.557", {"start": v(104.45, 72.88) * mm, "mid": v(104.6, 72.52) * mm, "end": v(104.95, 72.38) * mm});
            skLineSegment(sketch, "E26.1.0.558", {"start": v(114.7, 74.26) * mm, "end": v(114.7, 72.88) * mm});
            skArc(sketch, "E26.1.0.559", {"start": v(92.02, 41.44) * mm, "mid": v(91.31, 41.15) * mm, "end": v(91.02, 40.44) * mm});
            skArc(sketch, "E26.1.0.560", {"start": v(114.7, 57.35) * mm, "mid": v(114.4, 58.06) * mm, "end": v(113.7, 58.35) * mm});
            skArc(sketch, "E26.1.0.561", {"start": v(81.76, 24.53) * mm, "mid": v(81.06, 24.24) * mm, "end": v(80.76, 23.53) * mm});
            skArc(sketch, "E26.1.0.562", {"start": v(83.94, 39.06) * mm, "mid": v(84.09, 38.7) * mm, "end": v(84.44, 38.56) * mm});
            skArc(sketch, "E26.1.0.563", {"start": v(93.2, 26.53) * mm, "mid": v(93.9, 26.82) * mm, "end": v(94.2, 27.53) * mm});
            skLineSegment(sketch, "E26.1.0.564", {"start": v(92.02, 24.53) * mm, "end": v(93.2, 24.53) * mm});
            skArc(sketch, "E26.1.0.565", {"start": v(73.69, 39.06) * mm, "mid": v(73.83, 38.7) * mm, "end": v(74.19, 38.56) * mm});
            skArc(sketch, "E26.1.0.566", {"start": v(94.2, 57.35) * mm, "mid": v(93.9, 58.06) * mm, "end": v(93.2, 58.35) * mm});
            skArc(sketch, "E26.1.0.567", {"start": v(94.2, 39.06) * mm, "mid": v(94.34, 38.7) * mm, "end": v(94.7, 38.56) * mm});
            skLineSegment(sketch, "E26.1.0.568", {"start": v(83.94, 79.64) * mm, "end": v(83.94, 78.26) * mm});
            skArc(sketch, "E26.1.0.569", {"start": v(104.95, 46.32) * mm, "mid": v(104.6, 46.18) * mm, "end": v(104.45, 45.82) * mm});
            skLineSegment(sketch, "E26.1.0.570", {"start": v(83.94, 74.26) * mm, "end": v(83.94, 72.88) * mm});
            skLineSegment(sketch, "E26.1.0.571", {"start": v(112.53, 26.53) * mm, "end": v(113.7, 26.53) * mm});
            skLineSegment(sketch, "E26.1.0.572", {"start": v(102.27, 43.44) * mm, "end": v(103.45, 43.44) * mm});
            skLineSegment(sketch, "E26.1.0.573", {"start": v(94.2, 40.44) * mm, "end": v(94.2, 39.06) * mm});
            skLineSegment(sketch, "E26.1.0.574", {"start": v(81.76, 43.44) * mm, "end": v(82.94, 43.44) * mm});
            skLineSegment(sketch, "E26.1.0.575", {"start": v(102.27, 77.26) * mm, "end": v(103.45, 77.26) * mm});
            skArc(sketch, "E26.1.0.576", {"start": v(82.94, 43.44) * mm, "mid": v(83.65, 43.73) * mm, "end": v(83.94, 44.44) * mm});
            skLineSegment(sketch, "E26.1.0.577", {"start": v(94.2, 23.53) * mm, "end": v(94.2, 22.15) * mm});
            skArc(sketch, "E26.1.0.578", {"start": v(114.7, 55.97) * mm, "mid": v(114.85, 55.61) * mm, "end": v(115.2, 55.47) * mm});
            skLineSegment(sketch, "E26.1.0.579", {"start": v(83.94, 23.53) * mm, "end": v(83.94, 22.15) * mm});
            skArc(sketch, "E26.1.0.580", {"start": v(81.76, 41.44) * mm, "mid": v(81.06, 41.15) * mm, "end": v(80.76, 40.44) * mm});
            skLineSegment(sketch, "E26.1.0.581", {"start": v(112.53, 41.44) * mm, "end": v(113.7, 41.44) * mm});
            skArc(sketch, "E26.1.0.582", {"start": v(83.94, 74.26) * mm, "mid": v(83.65, 74.97) * mm, "end": v(82.94, 75.26) * mm});
            skLineSegment(sketch, "E26.1.0.583", {"start": v(94.2, 57.35) * mm, "end": v(94.2, 55.97) * mm});
            skArc(sketch, "E26.1.0.584", {"start": v(103.45, 77.26) * mm, "mid": v(104.15, 77.55) * mm, "end": v(104.45, 78.26) * mm});
            skArc(sketch, "E26.1.0.585", {"start": v(91.02, 27.53) * mm, "mid": v(91.31, 26.82) * mm, "end": v(92.02, 26.53) * mm});
            skLineSegment(sketch, "E26.1.0.586", {"start": v(92.02, 43.44) * mm, "end": v(93.2, 43.44) * mm});
            skArc(sketch, "E26.1.0.587", {"start": v(71.51, 58.35) * mm, "mid": v(70.8, 58.06) * mm, "end": v(70.51, 57.35) * mm});
            skLineSegment(sketch, "E26.1.0.588", {"start": v(102.27, 58.35) * mm, "end": v(103.45, 58.35) * mm});
            skArc(sketch, "E26.1.0.589", {"start": v(93.2, 77.26) * mm, "mid": v(93.9, 77.55) * mm, "end": v(94.2, 78.26) * mm});
            skArc(sketch, "E26.1.0.590", {"start": v(73.69, 40.44) * mm, "mid": v(73.4, 41.15) * mm, "end": v(72.69, 41.44) * mm});
            skArc(sketch, "E26.1.0.591", {"start": v(73.69, 57.35) * mm, "mid": v(73.4, 58.06) * mm, "end": v(72.69, 58.35) * mm});
            skArc(sketch, "E26.1.0.592", {"start": v(113.7, 60.35) * mm, "mid": v(114.4, 60.64) * mm, "end": v(114.7, 61.35) * mm});
            skArc(sketch, "E26.1.0.593", {"start": v(72.69, 60.35) * mm, "mid": v(73.4, 60.64) * mm, "end": v(73.69, 61.35) * mm});
            skArc(sketch, "E26.1.0.594", {"start": v(82.94, 26.53) * mm, "mid": v(83.65, 26.82) * mm, "end": v(83.94, 27.53) * mm});
            skLineSegment(sketch, "E26.1.0.595", {"start": v(104.45, 45.82) * mm, "end": v(104.45, 44.44) * mm});
            skLineSegment(sketch, "E26.1.0.596", {"start": v(81.76, 41.44) * mm, "end": v(82.94, 41.44) * mm});
            skLineSegment(sketch, "E26.1.0.597", {"start": v(92.02, 41.44) * mm, "end": v(93.2, 41.44) * mm});
            skArc(sketch, "E26.1.0.598", {"start": v(94.2, 55.97) * mm, "mid": v(94.34, 55.61) * mm, "end": v(94.7, 55.47) * mm});
            skArc(sketch, "E26.1.0.599", {"start": v(94.2, 23.53) * mm, "mid": v(93.9, 24.24) * mm, "end": v(93.2, 24.53) * mm});
            skArc(sketch, "E26.1.0.600", {"start": v(111.53, 78.26) * mm, "mid": v(111.82, 77.55) * mm, "end": v(112.53, 77.26) * mm});
            skLineSegment(sketch, "E26.1.0.601", {"start": v(114.7, 45.82) * mm, "end": v(114.7, 44.44) * mm});
            skArc(sketch, "E26.1.0.602", {"start": v(83.94, 55.97) * mm, "mid": v(84.09, 55.61) * mm, "end": v(84.44, 55.47) * mm});
            skArc(sketch, "E26.1.0.603", {"start": v(80.76, 78.26) * mm, "mid": v(81.06, 77.55) * mm, "end": v(81.76, 77.26) * mm});
            skLineSegment(sketch, "E26.1.0.604", {"start": v(73.69, 40.44) * mm, "end": v(73.69, 39.06) * mm});
            skLineSegment(sketch, "E26.1.0.605", {"start": v(81.76, 75.26) * mm, "end": v(82.94, 75.26) * mm});
            skArc(sketch, "E26.1.0.606", {"start": v(83.94, 57.35) * mm, "mid": v(83.65, 58.06) * mm, "end": v(82.94, 58.35) * mm});
            skLineSegment(sketch, "E26.1.0.607", {"start": v(94.2, 74.26) * mm, "end": v(94.2, 72.88) * mm});
            skArc(sketch, "E26.1.0.608", {"start": v(70.51, 27.53) * mm, "mid": v(70.8, 26.82) * mm, "end": v(71.51, 26.53) * mm});
            skArc(sketch, "E26.1.0.609", {"start": v(112.53, 58.35) * mm, "mid": v(111.82, 58.06) * mm, "end": v(111.53, 57.35) * mm});
            skArc(sketch, "E26.1.0.610", {"start": v(83.94, 72.88) * mm, "mid": v(84.09, 72.52) * mm, "end": v(84.44, 72.38) * mm});
            skArc(sketch, "E26.1.0.611", {"start": v(102.27, 24.53) * mm, "mid": v(101.57, 24.24) * mm, "end": v(101.27, 23.53) * mm});
            skArc(sketch, "E26.1.0.612", {"start": v(80.76, 61.35) * mm, "mid": v(81.06, 60.64) * mm, "end": v(81.76, 60.35) * mm});
            skLineSegment(sketch, "E26.1.0.613", {"start": v(114.7, 28.91) * mm, "end": v(114.7, 27.53) * mm});
            skArc(sketch, "E26.1.0.614", {"start": v(104.45, 55.97) * mm, "mid": v(104.6, 55.61) * mm, "end": v(104.95, 55.47) * mm});
            skLineSegment(sketch, "E26.1.0.615", {"start": v(102.27, 92.17) * mm, "end": v(103.45, 92.17) * mm});
            skLineSegment(sketch, "E26.1.0.616", {"start": v(92.02, 58.35) * mm, "end": v(93.2, 58.35) * mm});
            skLineSegment(sketch, "E26.1.0.617", {"start": v(104.45, 74.26) * mm, "end": v(104.45, 72.88) * mm});
            skArc(sketch, "E26.1.0.618", {"start": v(80.76, 27.53) * mm, "mid": v(81.06, 26.82) * mm, "end": v(81.76, 26.53) * mm});
            skLineSegment(sketch, "E26.1.0.619", {"start": v(102.27, 60.35) * mm, "end": v(103.45, 60.35) * mm});
            skArc(sketch, "E26.1.0.620", {"start": v(94.7, 80.14) * mm, "mid": v(94.34, 80) * mm, "end": v(94.2, 79.64) * mm});
            skArc(sketch, "E26.1.0.621", {"start": v(93.2, 43.44) * mm, "mid": v(93.9, 43.73) * mm, "end": v(94.2, 44.44) * mm});
            skArc(sketch, "E26.1.0.622", {"start": v(102.27, 58.35) * mm, "mid": v(101.57, 58.06) * mm, "end": v(101.27, 57.35) * mm});
            skArc(sketch, "E26.1.0.623", {"start": v(104.45, 57.35) * mm, "mid": v(104.15, 58.06) * mm, "end": v(103.45, 58.35) * mm});
            skLineSegment(sketch, "E26.1.0.624", {"start": v(81.76, 26.53) * mm, "end": v(82.94, 26.53) * mm});
            skArc(sketch, "E26.1.0.625", {"start": v(114.7, 72.88) * mm, "mid": v(114.85, 72.52) * mm, "end": v(115.2, 72.38) * mm});
            skArc(sketch, "E26.1.0.626", {"start": v(111.53, 61.35) * mm, "mid": v(111.82, 60.64) * mm, "end": v(112.53, 60.35) * mm});
            skArc(sketch, "E26.1.0.627", {"start": v(73.69, 55.97) * mm, "mid": v(73.83, 55.61) * mm, "end": v(74.19, 55.47) * mm});
            skLineSegment(sketch, "E26.1.0.628", {"start": v(73.69, 45.82) * mm, "end": v(73.69, 44.44) * mm});
            skArc(sketch, "E26.1.0.629", {"start": v(104.95, 29.41) * mm, "mid": v(104.6, 29.27) * mm, "end": v(104.45, 28.91) * mm});
            skArc(sketch, "E26.1.0.630", {"start": v(114.7, 39.06) * mm, "mid": v(114.85, 38.7) * mm, "end": v(115.2, 38.56) * mm});
            skArc(sketch, "E26.1.0.631", {"start": v(94.7, 46.32) * mm, "mid": v(94.34, 46.18) * mm, "end": v(94.2, 45.82) * mm});
            skArc(sketch, "E26.1.0.632", {"start": v(113.7, 43.44) * mm, "mid": v(114.4, 43.73) * mm, "end": v(114.7, 44.44) * mm});
            skArc(sketch, "E26.1.0.633", {"start": v(94.2, 74.26) * mm, "mid": v(93.9, 74.97) * mm, "end": v(93.2, 75.26) * mm});
            skLineSegment(sketch, "E26.1.0.634", {"start": v(114.7, 23.53) * mm, "end": v(114.7, 22.15) * mm});
            skArc(sketch, "E26.1.0.635", {"start": v(73.69, 23.53) * mm, "mid": v(73.4, 24.24) * mm, "end": v(72.69, 24.53) * mm});
            skArc(sketch, "E26.1.0.636", {"start": v(71.51, 24.53) * mm, "mid": v(70.8, 24.24) * mm, "end": v(70.51, 23.53) * mm});
            skArc(sketch, "E26.1.0.637", {"start": v(101.27, 27.53) * mm, "mid": v(101.57, 26.82) * mm, "end": v(102.27, 26.53) * mm});
            skArc(sketch, "E26.1.0.638", {"start": v(111.53, 10.62) * mm, "mid": v(111.82, 9.91) * mm, "end": v(112.53, 9.62) * mm});
            skLineSegment(sketch, "E26.1.0.639", {"start": v(102.27, 75.26) * mm, "end": v(103.45, 75.26) * mm});
            skLineSegment(sketch, "E26.1.0.640", {"start": v(94.2, 79.64) * mm, "end": v(94.2, 78.26) * mm});
            skLineSegment(sketch, "E26.1.0.641", {"start": v(83.94, 28.91) * mm, "end": v(83.94, 27.53) * mm});
            skArc(sketch, "E26.1.0.642", {"start": v(74.19, 29.41) * mm, "mid": v(73.83, 29.27) * mm, "end": v(73.69, 28.91) * mm});
            skArc(sketch, "E26.1.0.643", {"start": v(114.7, 40.44) * mm, "mid": v(114.4, 41.15) * mm, "end": v(113.7, 41.44) * mm});
            skArc(sketch, "E26.1.0.644", {"start": v(78.77, 20.65) * mm, "mid": v(78.47, 21.35) * mm, "end": v(77.77, 21.65) * mm});
            skLineSegment(sketch, "E26.1.0.645", {"start": v(104.45, 62.73) * mm, "end": v(104.45, 61.35) * mm});
            skLineSegment(sketch, "E26.1.0.646", {"start": v(83.94, 62.73) * mm, "end": v(83.94, 61.35) * mm});
            skArc(sketch, "E26.1.0.647", {"start": v(73.69, 89.79) * mm, "mid": v(73.83, 89.43) * mm, "end": v(74.19, 89.29) * mm});
            skLineSegment(sketch, "E26.1.0.648", {"start": v(71.51, 43.44) * mm, "end": v(72.69, 43.44) * mm});
            skArc(sketch, "E26.1.0.649", {"start": v(94.2, 40.44) * mm, "mid": v(93.9, 41.15) * mm, "end": v(93.2, 41.44) * mm});
            skArc(sketch, "E26.1.0.650", {"start": v(72.69, 9.62) * mm, "mid": v(73.4, 9.91) * mm, "end": v(73.69, 10.62) * mm});
            skLineSegment(sketch, "E26.1.0.651", {"start": v(94.2, 45.82) * mm, "end": v(94.2, 44.44) * mm});
            skLineSegment(sketch, "E26.1.0.652", {"start": v(104.45, 28.91) * mm, "end": v(104.45, 27.53) * mm});
            skArc(sketch, "E26.1.0.653", {"start": v(111.53, 27.53) * mm, "mid": v(111.82, 26.82) * mm, "end": v(112.53, 26.53) * mm});
            skLineSegment(sketch, "E26.1.0.654", {"start": v(71.51, 60.35) * mm, "end": v(72.69, 60.35) * mm});
            skArc(sketch, "E26.1.0.655", {"start": v(114.7, 23.53) * mm, "mid": v(114.4, 24.24) * mm, "end": v(113.7, 24.53) * mm});
            skArc(sketch, "E26.1.0.656", {"start": v(102.27, 41.44) * mm, "mid": v(101.57, 41.15) * mm, "end": v(101.27, 40.44) * mm});
            skLineSegment(sketch, "E26.1.0.657", {"start": v(104.45, 57.35) * mm, "end": v(104.45, 55.97) * mm});
            skLineSegment(sketch, "E26.1.0.658", {"start": v(71.51, 41.44) * mm, "end": v(72.69, 41.44) * mm});
            skArc(sketch, "E26.1.0.659", {"start": v(94.2, 72.88) * mm, "mid": v(94.34, 72.52) * mm, "end": v(94.7, 72.38) * mm});
            skArc(sketch, "E26.1.0.660", {"start": v(83.94, 22.15) * mm, "mid": v(84.09, 21.8) * mm, "end": v(84.44, 21.65) * mm});
            skLineSegment(sketch, "E26.1.0.661", {"start": v(114.7, 40.44) * mm, "end": v(114.7, 39.06) * mm});
            skLineSegment(sketch, "E26.1.0.662", {"start": v(73.69, 74.26) * mm, "end": v(73.69, 72.88) * mm});
            skArc(sketch, "E26.1.0.663", {"start": v(73.69, 74.26) * mm, "mid": v(73.4, 74.97) * mm, "end": v(72.69, 75.26) * mm});
            skArc(sketch, "E26.1.0.664", {"start": v(84.44, 80.14) * mm, "mid": v(84.09, 80) * mm, "end": v(83.94, 79.64) * mm});
            skArc(sketch, "E26.1.0.665", {"start": v(112.53, 41.44) * mm, "mid": v(111.82, 41.15) * mm, "end": v(111.53, 40.44) * mm});
            skLineSegment(sketch, "E26.1.0.666", {"start": v(73.69, 23.53) * mm, "end": v(73.69, 22.15) * mm});
            skArc(sketch, "E26.1.0.667", {"start": v(92.02, 24.53) * mm, "mid": v(91.31, 24.24) * mm, "end": v(91.02, 23.53) * mm});
            skLineSegment(sketch, "E26.1.0.668", {"start": v(112.53, 75.26) * mm, "end": v(113.7, 75.26) * mm});
            skLineSegment(sketch, "E26.1.0.669", {"start": v(73.69, 28.91) * mm, "end": v(73.69, 27.53) * mm});
            skLineSegment(sketch, "E26.1.0.670", {"start": v(92.02, 26.53) * mm, "end": v(93.2, 26.53) * mm});
            skLineSegment(sketch, "E26.1.0.671", {"start": v(83.94, 40.44) * mm, "end": v(83.94, 39.06) * mm});
            skLineSegment(sketch, "E26.1.0.672", {"start": v(71.51, 26.53) * mm, "end": v(72.69, 26.53) * mm});
            skArc(sketch, "E26.1.0.673", {"start": v(114.7, 74.26) * mm, "mid": v(114.4, 74.97) * mm, "end": v(113.7, 75.26) * mm});
            skArc(sketch, "E26.1.0.674", {"start": v(101.27, 61.35) * mm, "mid": v(101.57, 60.64) * mm, "end": v(102.27, 60.35) * mm});
            skArc(sketch, "E26.1.0.675", {"start": v(104.45, 74.26) * mm, "mid": v(104.15, 74.97) * mm, "end": v(103.45, 75.26) * mm});
            skLineSegment(sketch, "E26.1.0.676", {"start": v(73.69, 79.64) * mm, "end": v(73.69, 78.26) * mm});
            skLineSegment(sketch, "E26.1.0.677", {"start": v(112.53, 24.53) * mm, "end": v(113.7, 24.53) * mm});
            skArc(sketch, "E26.1.0.678", {"start": v(83.94, 40.44) * mm, "mid": v(83.65, 41.15) * mm, "end": v(82.94, 41.44) * mm});
            skArc(sketch, "E26.1.0.679", {"start": v(103.45, 43.44) * mm, "mid": v(104.15, 43.73) * mm, "end": v(104.45, 44.44) * mm});
            skArc(sketch, "E26.1.0.680", {"start": v(74.19, 12.5) * mm, "mid": v(73.83, 12.36) * mm, "end": v(73.69, 12) * mm});
            skArc(sketch, "E26.1.0.681", {"start": v(102.27, 92.17) * mm, "mid": v(101.57, 91.88) * mm, "end": v(101.27, 91.17) * mm});
            skLineSegment(sketch, "E26.1.0.682", {"start": v(104.45, 40.44) * mm, "end": v(104.45, 39.06) * mm});
            skLineSegment(sketch, "E26.1.0.683", {"start": v(73.69, 57.35) * mm, "end": v(73.69, 55.97) * mm});
            skArc(sketch, "E26.1.0.684", {"start": v(72.69, 77.26) * mm, "mid": v(73.4, 77.55) * mm, "end": v(73.69, 78.26) * mm});
            skLineSegment(sketch, "E26.1.0.685", {"start": v(71.51, 58.35) * mm, "end": v(72.69, 58.35) * mm});
            skArc(sketch, "E26.1.0.686", {"start": v(73.69, 72.88) * mm, "mid": v(73.83, 72.52) * mm, "end": v(74.19, 72.38) * mm});
            skLineSegment(sketch, "E26.1.0.687", {"start": v(83.94, 57.35) * mm, "end": v(83.94, 55.97) * mm});
            skLineSegment(sketch, "E26.1.0.688", {"start": v(112.53, 58.35) * mm, "end": v(113.7, 58.35) * mm});
            skArc(sketch, "E26.1.0.689", {"start": v(111.53, 44.44) * mm, "mid": v(111.82, 43.73) * mm, "end": v(112.53, 43.44) * mm});
            skLineSegment(sketch, "E26.1.0.690", {"start": v(94.2, 28.91) * mm, "end": v(94.2, 27.53) * mm});
            skArc(sketch, "E26.1.0.691", {"start": v(103.45, 60.35) * mm, "mid": v(104.15, 60.64) * mm, "end": v(104.45, 61.35) * mm});
            skArc(sketch, "E26.1.0.692", {"start": v(101.27, 78.26) * mm, "mid": v(101.57, 77.55) * mm, "end": v(102.27, 77.26) * mm});
            skArc(sketch, "E26.1.0.693", {"start": v(112.53, 75.26) * mm, "mid": v(111.82, 74.97) * mm, "end": v(111.53, 74.26) * mm});
            skLineSegment(sketch, "E26.1.0.694", {"start": v(71.51, 77.26) * mm, "end": v(72.69, 77.26) * mm});
            skArc(sketch, "E26.1.0.695", {"start": v(72.69, 26.53) * mm, "mid": v(73.4, 26.82) * mm, "end": v(73.69, 27.53) * mm});
            skLineSegment(sketch, "E26.1.0.696", {"start": v(71.51, 24.53) * mm, "end": v(72.69, 24.53) * mm});
            skLineSegment(sketch, "E26.1.0.697", {"start": v(81.76, 24.53) * mm, "end": v(82.94, 24.53) * mm});
            skLineSegment(sketch, "E26.1.0.698", {"start": v(81.76, 77.26) * mm, "end": v(82.94, 77.26) * mm});
            skArc(sketch, "E26.1.0.699", {"start": v(82.94, 77.26) * mm, "mid": v(83.65, 77.55) * mm, "end": v(83.94, 78.26) * mm});
            skLineSegment(sketch, "E26.1.0.700", {"start": v(73.69, 12) * mm, "end": v(73.69, 10.62) * mm});
            skArc(sketch, "E26.1.0.701", {"start": v(74.19, 80.14) * mm, "mid": v(73.83, 80) * mm, "end": v(73.69, 79.64) * mm});
            skLineSegment(sketch, "E26.1.0.702", {"start": v(112.53, 60.35) * mm, "end": v(113.7, 60.35) * mm});
            skArc(sketch, "E26.1.0.703", {"start": v(81.76, 58.35) * mm, "mid": v(81.06, 58.06) * mm, "end": v(80.76, 57.35) * mm});
            skLineSegment(sketch, "E26.1.0.704", {"start": v(71.51, 9.62) * mm, "end": v(72.69, 9.62) * mm});
            skLineSegment(sketch, "E26.1.0.705", {"start": v(114.7, 79.64) * mm, "end": v(114.7, 78.26) * mm});
            skArc(sketch, "E26.1.0.706", {"start": v(101.27, 44.44) * mm, "mid": v(101.57, 43.73) * mm, "end": v(102.27, 43.44) * mm});
            skLineSegment(sketch, "E26.1.0.707", {"start": v(112.53, 43.44) * mm, "end": v(113.7, 43.44) * mm});
            skArc(sketch, "E26.1.0.708", {"start": v(113.7, 26.53) * mm, "mid": v(114.4, 26.82) * mm, "end": v(114.7, 27.53) * mm});
            skArc(sketch, "E26.1.0.709", {"start": v(104.45, 39.06) * mm, "mid": v(104.6, 38.7) * mm, "end": v(104.95, 38.56) * mm});
            skLineSegment(sketch, "E26.1.0.710", {"start": v(71.51, 75.26) * mm, "end": v(72.69, 75.26) * mm});
            skLineSegment(sketch, "E26.1.0.711", {"start": v(114.7, 57.35) * mm, "end": v(114.7, 55.97) * mm});
            skLineSegment(sketch, "E26.1.0.712", {"start": v(102.27, 26.53) * mm, "end": v(103.45, 26.53) * mm});
            skArc(sketch, "E26.1.0.713", {"start": v(103.45, 26.53) * mm, "mid": v(104.15, 26.82) * mm, "end": v(104.45, 27.53) * mm});
            skLineSegment(sketch, "E26.1.0.714", {"start": v(112.53, 77.26) * mm, "end": v(113.7, 77.26) * mm});
            skLineSegment(sketch, "E26.1.0.715", {"start": v(102.27, 41.44) * mm, "end": v(103.45, 41.44) * mm});
            skArc(sketch, "E26.1.0.716", {"start": v(82.94, 60.35) * mm, "mid": v(83.65, 60.64) * mm, "end": v(83.94, 61.35) * mm});
            skLineSegment(sketch, "E26.1.0.717", {"start": v(81.76, 60.35) * mm, "end": v(82.94, 60.35) * mm});
            skArc(sketch, "E26.1.0.718", {"start": v(113.7, 77.26) * mm, "mid": v(114.4, 77.55) * mm, "end": v(114.7, 78.26) * mm});
            skArc(sketch, "E26.1.0.719", {"start": v(104.45, 23.53) * mm, "mid": v(104.15, 24.24) * mm, "end": v(103.45, 24.53) * mm});
            skArc(sketch, "E26.1.0.720", {"start": v(104.45, 40.44) * mm, "mid": v(104.15, 41.15) * mm, "end": v(103.45, 41.44) * mm});
            skLineSegment(sketch, "E26.1.0.721", {"start": v(102.27, 24.53) * mm, "end": v(103.45, 24.53) * mm});
            skLineSegment(sketch, "E26.direction1", {"start": v(9.62, 9.62) * mm, "end": v(70.51, 9.62) * mm, "construction": true});
            skSolve(sketch);
        }
        {
            var Q0;
            Q0 = qSketchRegion(id + "F2", true);
            extrude(context, id + "F3", {"entities" : qUnion([Q0]), "operationType" : NewBodyOperationType.ADD, "oppositeDirection" : true, "depth" : .9 * mm, "offsetDistance" : 25 * mm});
        }
        {
            var Q0;
            Q0=makeQuery(id+"F3.boolean.opBoolean","MERGE",FACE,{"derivedFrom":[makeQuery(id+"F1.opExtrude","CAP_FACE",FACE,{"disambiguationData":[OSD([sQuery(id+"F0.wireOp",EDGE,"E0.bottom"),sQuery(id+"F0.wireOp",EDGE,"E0.top"),sQuery(id+"F0.wireOp",EDGE,"E0.left"),sQuery(id+"F0.wireOp",EDGE,"E0.right"),sQuery(id+"F0.wireOp",EDGE,"E1"),sQuery(id+"F0.wireOp",EDGE,"E2"),sQuery(id+"F0.wireOp",EDGE,"E3"),sQuery(id+"F0.wireOp",EDGE,"E4"),sQuery(id+"F0.wireOp",EDGE,"E5.bottom"),sQuery(id+"F0.wireOp",EDGE,"E5.top"),sQuery(id+"F0.wireOp",EDGE,"E5.left"),sQuery(id+"F0.wireOp",EDGE,"E5.right"),sQuery(id+"F0.wireOp",EDGE,"E6.bottom"),sQuery(id+"F0.wireOp",EDGE,"E6.top"),sQuery(id+"F0.wireOp",EDGE,"E6.left"),sQuery(id+"F0.wireOp",EDGE,"E6.right")])],"isStart":false}),makeQuery(id+"F3.opExtrude","CAP_FACE",FACE,{"disambiguationData":[OSD([sQuery(id+"F2.wireOp",EDGE,"E7.bottom"),sQuery(id+"F2.wireOp",EDGE,"E7.top"),sQuery(id+"F2.wireOp",EDGE,"E7.left"),sQuery(id+"F2.wireOp",EDGE,"E7.right"),sQuery(id+"F2.wireOp",EDGE,"E8.bottom"),sQuery(id+"F2.wireOp",EDGE,"E8.top"),sQuery(id+"F2.wireOp",EDGE,"E8.right"),sQuery(id+"F2.wireOp",EDGE,"E9.bottom"),sQuery(id+"F2.wireOp",EDGE,"E9.top"),sQuery(id+"F2.wireOp",EDGE,"E9.right"),sQuery(id+"F2.wireOp",EDGE,"E10.filletArc"),sQuery(id+"F2.wireOp",EDGE,"E11.filletArc"),sQuery(id+"F2.wireOp",EDGE,"E12.filletArc"),sQuery(id+"F2.wireOp",EDGE,"E13.filletArc"),sQuery(id+"F2.wireOp",EDGE,"E14.filletArc"),sQuery(id+"F2.wireOp",EDGE,"E15.filletArc"),sQuery(id+"F2.wireOp",EDGE,"E16.trimOffspring"),sQuery(id+"F2.wireOp",EDGE,"E17.trimOffspring"),sQuery(id+"F2.wireOp",EDGE,"E18.filletArc"),sQuery(id+"F2.wireOp",EDGE,"E19.filletArc"),sQuery(id+"F2.wireOp",EDGE,"E20.1.0.0"),sQuery(id+"F2.wireOp",EDGE,"E20.1.0.1"),sQuery(id+"F2.wireOp",EDGE,"E20.1.0.2"),sQuery(id+"F2.wireOp",EDGE,"E20.1.0.3"),sQuery(id+"F2.wireOp",EDGE,"E20.1.0.6"),sQuery(id+"F2.wireOp",EDGE,"E20.1.0.7"),sQuery(id+"F2.wireOp",EDGE,"E20.1.0.9"),sQuery(id+"F2.wireOp",EDGE,"E20.1.0.10"),sQuery(id+"F2.wireOp",EDGE,"E20.1.0.11"),sQuery(id+"F2.wireOp",EDGE,"E20.1.0.13"),sQuery(id+"F2.wireOp",EDGE,"E20.1.0.14"),sQuery(id+"F2.wireOp",EDGE,"E20.1.0.20"),sQuery(id+"F2.wireOp",EDGE,"E20.1.0.21"),sQuery(id+"F2.wireOp",EDGE,"E20.1.0.22"),sQuery(id+"F2.wireOp",EDGE,"E20.1.0.23"),sQuery(id+"F2.wireOp",EDGE,"E20.1.0.24"),sQuery(id+"F2.wireOp",EDGE,"E20.1.0.25"),sQuery(id+"F2.wireOp",EDGE,"E20.1.0.26"),sQuery(id+"F2.wireOp",EDGE,"E20.1.0.27"),sQuery(id+"F2.wireOp",EDGE,"E20.2.0.0"),sQuery(id+"F2.wireOp",EDGE,"E20.2.0.1"),sQuery(id+"F2.wireOp",EDGE,"E20.2.0.2"),sQuery(id+"F2.wireOp",EDGE,"E20.2.0.3"),sQuery(id+"F2.wireOp",EDGE,"E20.2.0.6"),sQuery(id+"F2.wireOp",EDGE,"E20.2.0.7"),sQuery(id+"F2.wireOp",EDGE,"E20.2.0.9"),sQuery(id+"F2.wireOp",EDGE,"E20.2.0.10"),sQuery(id+"F2.wireOp",EDGE,"E20.2.0.11"),sQuery(id+"F2.wireOp",EDGE,"E20.2.0.13"),sQuery(id+"F2.wireOp",EDGE,"E20.2.0.14"),sQuery(id+"F2.wireOp",EDGE,"E20.2.0.20"),sQuery(id+"F2.wireOp",EDGE,"E20.2.0.21"),sQuery(id+"F2.wireOp",EDGE,"E20.2.0.22"),sQuery(id+"F2.wireOp",EDGE,"E20.2.0.23"),sQuery(id+"F2.wireOp",EDGE,"E20.2.0.24"),sQuery(id+"F2.wireOp",EDGE,"E20.2.0.25"),sQuery(id+"F2.wireOp",EDGE,"E20.2.0.26"),sQuery(id+"F2.wireOp",EDGE,"E20.2.0.27"),sQuery(id+"F2.wireOp",EDGE,"E20.3.0.0"),sQuery(id+"F2.wireOp",EDGE,"E20.3.0.1"),sQuery(id+"F2.wireOp",EDGE,"E20.3.0.2"),sQuery(id+"F2.wireOp",EDGE,"E20.3.0.3"),sQuery(id+"F2.wireOp",EDGE,"E20.3.0.6"),sQuery(id+"F2.wireOp",EDGE,"E20.3.0.7"),sQuery(id+"F2.wireOp",EDGE,"E20.3.0.9"),sQuery(id+"F2.wireOp",EDGE,"E20.3.0.10"),sQuery(id+"F2.wireOp",EDGE,"E20.3.0.11"),sQuery(id+"F2.wireOp",EDGE,"E20.3.0.13"),sQuery(id+"F2.wireOp",EDGE,"E20.3.0.14"),sQuery(id+"F2.wireOp",EDGE,"E20.3.0.20"),sQuery(id+"F2.wireOp",EDGE,"E20.3.0.21"),sQuery(id+"F2.wireOp",EDGE,"E20.3.0.22"),sQuery(id+"F2.wireOp",EDGE,"E20.3.0.23"),sQuery(id+"F2.wireOp",EDGE,"E20.3.0.24"),sQuery(id+"F2.wireOp",EDGE,"E20.3.0.25"),sQuery(id+"F2.wireOp",EDGE,"E20.3.0.26"),sQuery(id+"F2.wireOp",EDGE,"E20.3.0.27"),sQuery(id+"F2.wireOp",EDGE,"E20.4.0.0"),sQuery(id+"F2.wireOp",EDGE,"E20.4.0.1"),sQuery(id+"F2.wireOp",EDGE,"E20.4.0.2"),sQuery(id+"F2.wireOp",EDGE,"E20.4.0.3"),sQuery(id+"F2.wireOp",EDGE,"E20.4.0.6"),sQuery(id+"F2.wireOp",EDGE,"E20.4.0.7"),sQuery(id+"F2.wireOp",EDGE,"E20.4.0.9"),sQuery(id+"F2.wireOp",EDGE,"E20.4.0.10"),sQuery(id+"F2.wireOp",EDGE,"E20.4.0.11"),sQuery(id+"F2.wireOp",EDGE,"E20.4.0.13"),sQuery(id+"F2.wireOp",EDGE,"E20.4.0.14"),sQuery(id+"F2.wireOp",EDGE,"E20.4.0.20"),sQuery(id+"F2.wireOp",EDGE,"E20.4.0.21"),sQuery(id+"F2.wireOp",EDGE,"E20.4.0.22"),sQuery(id+"F2.wireOp",EDGE,"E20.4.0.23"),sQuery(id+"F2.wireOp",EDGE,"E20.4.0.24"),sQuery(id+"F2.wireOp",EDGE,"E20.4.0.25"),sQuery(id+"F2.wireOp",EDGE,"E20.4.0.26"),sQuery(id+"F2.wireOp",EDGE,"E20.4.0.27"),sQuery(id+"F2.wireOp",EDGE,"E21.bottom"),sQuery(id+"F2.wireOp",EDGE,"E21.top"),sQuery(id+"F2.wireOp",EDGE,"E21.right")])],"isStart":true}),makeQuery(id+"F3.opExtrude","CAP_FACE",FACE,{"disambiguationData":[OSD([sQuery(id+"F2.wireOp",EDGE,"E20.0.1.0"),sQuery(id+"F2.wireOp",EDGE,"E20.0.1.1"),sQuery(id+"F2.wireOp",EDGE,"E20.0.1.2"),sQuery(id+"F2.wireOp",EDGE,"E20.0.1.3"),sQuery(id+"F2.wireOp",EDGE,"E20.0.1.6"),sQuery(id+"F2.wireOp",EDGE,"E20.0.1.7"),sQuery(id+"F2.wireOp",EDGE,"E20.0.1.9"),sQuery(id+"F2.wireOp",EDGE,"E20.0.1.10"),sQuery(id+"F2.wireOp",EDGE,"E20.0.1.11"),sQuery(id+"F2.wireOp",EDGE,"E20.0.1.12"),sQuery(id+"F2.wireOp",EDGE,"E20.0.1.13"),sQuery(id+"F2.wireOp",EDGE,"E20.0.1.14"),sQuery(id+"F2.wireOp",EDGE,"E20.0.1.20"),sQuery(id+"F2.wireOp",EDGE,"E20.0.1.21"),sQuery(id+"F2.wireOp",EDGE,"E20.0.1.22"),sQuery(id+"F2.wireOp",EDGE,"E20.0.1.23"),sQuery(id+"F2.wireOp",EDGE,"E20.0.1.24"),sQuery(id+"F2.wireOp",EDGE,"E20.0.1.25"),sQuery(id+"F2.wireOp",EDGE,"E20.0.1.26"),sQuery(id+"F2.wireOp",EDGE,"E20.0.1.27"),sQuery(id+"F2.wireOp",EDGE,"E20.1.1.0"),sQuery(id+"F2.wireOp",EDGE,"E20.1.1.1"),sQuery(id+"F2.wireOp",EDGE,"E20.1.1.2"),sQuery(id+"F2.wireOp",EDGE,"E20.1.1.3"),sQuery(id+"F2.wireOp",EDGE,"E20.1.1.6"),sQuery(id+"F2.wireOp",EDGE,"E20.1.1.7"),sQuery(id+"F2.wireOp",EDGE,"E20.1.1.9"),sQuery(id+"F2.wireOp",EDGE,"E20.1.1.10"),sQuery(id+"F2.wireOp",EDGE,"E20.1.1.11"),sQuery(id+"F2.wireOp",EDGE,"E20.1.1.13"),sQuery(id+"F2.wireOp",EDGE,"E20.1.1.14"),sQuery(id+"F2.wireOp",EDGE,"E20.1.1.20"),sQuery(id+"F2.wireOp",EDGE,"E20.1.1.21"),sQuery(id+"F2.wireOp",EDGE,"E20.1.1.22"),sQuery(id+"F2.wireOp",EDGE,"E20.1.1.23"),sQuery(id+"F2.wireOp",EDGE,"E20.1.1.24"),sQuery(id+"F2.wireOp",EDGE,"E20.1.1.25"),sQuery(id+"F2.wireOp",EDGE,"E20.1.1.26"),sQuery(id+"F2.wireOp",EDGE,"E20.1.1.27"),sQuery(id+"F2.wireOp",EDGE,"E20.2.1.0"),sQuery(id+"F2.wireOp",EDGE,"E20.2.1.1"),sQuery(id+"F2.wireOp",EDGE,"E20.2.1.2"),sQuery(id+"F2.wireOp",EDGE,"E20.2.1.3"),sQuery(id+"F2.wireOp",EDGE,"E20.2.1.6"),sQuery(id+"F2.wireOp",EDGE,"E20.2.1.7"),sQuery(id+"F2.wireOp",EDGE,"E20.2.1.9"),sQuery(id+"F2.wireOp",EDGE,"E20.2.1.10"),sQuery(id+"F2.wireOp",EDGE,"E20.2.1.11"),sQuery(id+"F2.wireOp",EDGE,"E20.2.1.13"),sQuery(id+"F2.wireOp",EDGE,"E20.2.1.14"),sQuery(id+"F2.wireOp",EDGE,"E20.2.1.20"),sQuery(id+"F2.wireOp",EDGE,"E20.2.1.21"),sQuery(id+"F2.wireOp",EDGE,"E20.2.1.22"),sQuery(id+"F2.wireOp",EDGE,"E20.2.1.23"),sQuery(id+"F2.wireOp",EDGE,"E20.2.1.24"),sQuery(id+"F2.wireOp",EDGE,"E20.2.1.25"),sQuery(id+"F2.wireOp",EDGE,"E20.2.1.26"),sQuery(id+"F2.wireOp",EDGE,"E20.2.1.27"),sQuery(id+"F2.wireOp",EDGE,"E20.3.1.0"),sQuery(id+"F2.wireOp",EDGE,"E20.3.1.1"),sQuery(id+"F2.wireOp",EDGE,"E20.3.1.2"),sQuery(id+"F2.wireOp",EDGE,"E20.3.1.3"),sQuery(id+"F2.wireOp",EDGE,"E20.3.1.6"),sQuery(id+"F2.wireOp",EDGE,"E20.3.1.7"),sQuery(id+"F2.wireOp",EDGE,"E20.3.1.9"),sQuery(id+"F2.wireOp",EDGE,"E20.3.1.10"),sQuery(id+"F2.wireOp",EDGE,"E20.3.1.11"),sQuery(id+"F2.wireOp",EDGE,"E20.3.1.13"),sQuery(id+"F2.wireOp",EDGE,"E20.3.1.14"),sQuery(id+"F2.wireOp",EDGE,"E20.3.1.20"),sQuery(id+"F2.wireOp",EDGE,"E20.3.1.21"),sQuery(id+"F2.wireOp",EDGE,"E20.3.1.22"),sQuery(id+"F2.wireOp",EDGE,"E20.3.1.23"),sQuery(id+"F2.wireOp",EDGE,"E20.3.1.24"),sQuery(id+"F2.wireOp",EDGE,"E20.3.1.25"),sQuery(id+"F2.wireOp",EDGE,"E20.3.1.26"),sQuery(id+"F2.wireOp",EDGE,"E20.3.1.27"),sQuery(id+"F2.wireOp",EDGE,"E20.4.1.0"),sQuery(id+"F2.wireOp",EDGE,"E20.4.1.1"),sQuery(id+"F2.wireOp",EDGE,"E20.4.1.2"),sQuery(id+"F2.wireOp",EDGE,"E20.4.1.3"),sQuery(id+"F2.wireOp",EDGE,"E20.4.1.6"),sQuery(id+"F2.wireOp",EDGE,"E20.4.1.7"),sQuery(id+"F2.wireOp",EDGE,"E20.4.1.9"),sQuery(id+"F2.wireOp",EDGE,"E20.4.1.10"),sQuery(id+"F2.wireOp",EDGE,"E20.4.1.11"),sQuery(id+"F2.wireOp",EDGE,"E20.4.1.13"),sQuery(id+"F2.wireOp",EDGE,"E20.4.1.14"),sQuery(id+"F2.wireOp",EDGE,"E20.4.1.20"),sQuery(id+"F2.wireOp",EDGE,"E20.4.1.21"),sQuery(id+"F2.wireOp",EDGE,"E20.4.1.22"),sQuery(id+"F2.wireOp",EDGE,"E20.4.1.23"),sQuery(id+"F2.wireOp",EDGE,"E20.4.1.24"),sQuery(id+"F2.wireOp",EDGE,"E20.4.1.25"),sQuery(id+"F2.wireOp",EDGE,"E20.4.1.26"),sQuery(id+"F2.wireOp",EDGE,"E20.4.1.27"),sQuery(id+"F2.wireOp",EDGE,"E22.bottom"),sQuery(id+"F2.wireOp",EDGE,"E22.top"),sQuery(id+"F2.wireOp",EDGE,"E22.right")])],"isStart":true}),makeQuery(id+"F3.opExtrude","CAP_FACE",FACE,{"disambiguationData":[OSD([sQuery(id+"F2.wireOp",EDGE,"E20.0.2.0"),sQuery(id+"F2.wireOp",EDGE,"E20.0.2.1"),sQuery(id+"F2.wireOp",EDGE,"E20.0.2.2"),sQuery(id+"F2.wireOp",EDGE,"E20.0.2.3"),sQuery(id+"F2.wireOp",EDGE,"E20.0.2.6"),sQuery(id+"F2.wireOp",EDGE,"E20.0.2.7"),sQuery(id+"F2.wireOp",EDGE,"E20.0.2.9"),sQuery(id+"F2.wireOp",EDGE,"E20.0.2.10"),sQuery(id+"F2.wireOp",EDGE,"E20.0.2.11"),sQuery(id+"F2.wireOp",EDGE,"E20.0.2.12"),sQuery(id+"F2.wireOp",EDGE,"E20.0.2.13"),sQuery(id+"F2.wireOp",EDGE,"E20.0.2.14"),sQuery(id+"F2.wireOp",EDGE,"E20.0.2.20"),sQuery(id+"F2.wireOp",EDGE,"E20.0.2.21"),sQuery(id+"F2.wireOp",EDGE,"E20.0.2.22"),sQuery(id+"F2.wireOp",EDGE,"E20.0.2.23"),sQuery(id+"F2.wireOp",EDGE,"E20.0.2.24"),sQuery(id+"F2.wireOp",EDGE,"E20.0.2.25"),sQuery(id+"F2.wireOp",EDGE,"E20.0.2.26"),sQuery(id+"F2.wireOp",EDGE,"E20.0.2.27"),sQuery(id+"F2.wireOp",EDGE,"E20.1.2.0"),sQuery(id+"F2.wireOp",EDGE,"E20.1.2.1"),sQuery(id+"F2.wireOp",EDGE,"E20.1.2.2"),sQuery(id+"F2.wireOp",EDGE,"E20.1.2.3"),sQuery(id+"F2.wireOp",EDGE,"E20.1.2.6"),sQuery(id+"F2.wireOp",EDGE,"E20.1.2.7"),sQuery(id+"F2.wireOp",EDGE,"E20.1.2.9"),sQuery(id+"F2.wireOp",EDGE,"E20.1.2.10"),sQuery(id+"F2.wireOp",EDGE,"E20.1.2.11"),sQuery(id+"F2.wireOp",EDGE,"E20.1.2.13"),sQuery(id+"F2.wireOp",EDGE,"E20.1.2.14"),sQuery(id+"F2.wireOp",EDGE,"E20.1.2.20"),sQuery(id+"F2.wireOp",EDGE,"E20.1.2.21"),sQuery(id+"F2.wireOp",EDGE,"E20.1.2.22"),sQuery(id+"F2.wireOp",EDGE,"E20.1.2.23"),sQuery(id+"F2.wireOp",EDGE,"E20.1.2.24"),sQuery(id+"F2.wireOp",EDGE,"E20.1.2.25"),sQuery(id+"F2.wireOp",EDGE,"E20.1.2.26"),sQuery(id+"F2.wireOp",EDGE,"E20.1.2.27"),sQuery(id+"F2.wireOp",EDGE,"E20.2.2.0"),sQuery(id+"F2.wireOp",EDGE,"E20.2.2.1"),sQuery(id+"F2.wireOp",EDGE,"E20.2.2.2"),sQuery(id+"F2.wireOp",EDGE,"E20.2.2.3"),sQuery(id+"F2.wireOp",EDGE,"E20.2.2.6"),sQuery(id+"F2.wireOp",EDGE,"E20.2.2.7"),sQuery(id+"F2.wireOp",EDGE,"E20.2.2.9"),sQuery(id+"F2.wireOp",EDGE,"E20.2.2.10"),sQuery(id+"F2.wireOp",EDGE,"E20.2.2.11"),sQuery(id+"F2.wireOp",EDGE,"E20.2.2.13"),sQuery(id+"F2.wireOp",EDGE,"E20.2.2.14"),sQuery(id+"F2.wireOp",EDGE,"E20.2.2.20"),sQuery(id+"F2.wireOp",EDGE,"E20.2.2.21"),sQuery(id+"F2.wireOp",EDGE,"E20.2.2.22"),sQuery(id+"F2.wireOp",EDGE,"E20.2.2.23"),sQuery(id+"F2.wireOp",EDGE,"E20.2.2.24"),sQuery(id+"F2.wireOp",EDGE,"E20.2.2.25"),sQuery(id+"F2.wireOp",EDGE,"E20.2.2.26"),sQuery(id+"F2.wireOp",EDGE,"E20.2.2.27"),sQuery(id+"F2.wireOp",EDGE,"E20.3.2.0"),sQuery(id+"F2.wireOp",EDGE,"E20.3.2.1"),sQuery(id+"F2.wireOp",EDGE,"E20.3.2.2"),sQuery(id+"F2.wireOp",EDGE,"E20.3.2.3"),sQuery(id+"F2.wireOp",EDGE,"E20.3.2.6"),sQuery(id+"F2.wireOp",EDGE,"E20.3.2.7"),sQuery(id+"F2.wireOp",EDGE,"E20.3.2.9"),sQuery(id+"F2.wireOp",EDGE,"E20.3.2.10"),sQuery(id+"F2.wireOp",EDGE,"E20.3.2.11"),sQuery(id+"F2.wireOp",EDGE,"E20.3.2.13"),sQuery(id+"F2.wireOp",EDGE,"E20.3.2.14"),sQuery(id+"F2.wireOp",EDGE,"E20.3.2.20"),sQuery(id+"F2.wireOp",EDGE,"E20.3.2.21"),sQuery(id+"F2.wireOp",EDGE,"E20.3.2.22"),sQuery(id+"F2.wireOp",EDGE,"E20.3.2.23"),sQuery(id+"F2.wireOp",EDGE,"E20.3.2.24"),sQuery(id+"F2.wireOp",EDGE,"E20.3.2.25"),sQuery(id+"F2.wireOp",EDGE,"E20.3.2.26"),sQuery(id+"F2.wireOp",EDGE,"E20.3.2.27"),sQuery(id+"F2.wireOp",EDGE,"E20.4.2.0"),sQuery(id+"F2.wireOp",EDGE,"E20.4.2.1"),sQuery(id+"F2.wireOp",EDGE,"E20.4.2.2"),sQuery(id+"F2.wireOp",EDGE,"E20.4.2.3"),sQuery(id+"F2.wireOp",EDGE,"E20.4.2.6"),sQuery(id+"F2.wireOp",EDGE,"E20.4.2.7"),sQuery(id+"F2.wireOp",EDGE,"E20.4.2.9"),sQuery(id+"F2.wireOp",EDGE,"E20.4.2.10"),sQuery(id+"F2.wireOp",EDGE,"E20.4.2.11"),sQuery(id+"F2.wireOp",EDGE,"E20.4.2.13"),sQuery(id+"F2.wireOp",EDGE,"E20.4.2.14"),sQuery(id+"F2.wireOp",EDGE,"E20.4.2.20"),sQuery(id+"F2.wireOp",EDGE,"E20.4.2.21"),sQuery(id+"F2.wireOp",EDGE,"E20.4.2.22"),sQuery(id+"F2.wireOp",EDGE,"E20.4.2.23"),sQuery(id+"F2.wireOp",EDGE,"E20.4.2.24"),sQuery(id+"F2.wireOp",EDGE,"E20.4.2.25"),sQuery(id+"F2.wireOp",EDGE,"E20.4.2.26"),sQuery(id+"F2.wireOp",EDGE,"E20.4.2.27"),sQuery(id+"F2.wireOp",EDGE,"E23.bottom"),sQuery(id+"F2.wireOp",EDGE,"E23.top"),sQuery(id+"F2.wireOp",EDGE,"E23.right")])],"isStart":true}),makeQuery(id+"F3.opExtrude","CAP_FACE",FACE,{"disambiguationData":[OSD([sQuery(id+"F2.wireOp",EDGE,"E20.0.3.0"),sQuery(id+"F2.wireOp",EDGE,"E20.0.3.1"),sQuery(id+"F2.wireOp",EDGE,"E20.0.3.2"),sQuery(id+"F2.wireOp",EDGE,"E20.0.3.3"),sQuery(id+"F2.wireOp",EDGE,"E20.0.3.6"),sQuery(id+"F2.wireOp",EDGE,"E20.0.3.7"),sQuery(id+"F2.wireOp",EDGE,"E20.0.3.9"),sQuery(id+"F2.wireOp",EDGE,"E20.0.3.10"),sQuery(id+"F2.wireOp",EDGE,"E20.0.3.11"),sQuery(id+"F2.wireOp",EDGE,"E20.0.3.12"),sQuery(id+"F2.wireOp",EDGE,"E20.0.3.13"),sQuery(id+"F2.wireOp",EDGE,"E20.0.3.14"),sQuery(id+"F2.wireOp",EDGE,"E20.0.3.20"),sQuery(id+"F2.wireOp",EDGE,"E20.0.3.21"),sQuery(id+"F2.wireOp",EDGE,"E20.0.3.22"),sQuery(id+"F2.wireOp",EDGE,"E20.0.3.23"),sQuery(id+"F2.wireOp",EDGE,"E20.0.3.24"),sQuery(id+"F2.wireOp",EDGE,"E20.0.3.25"),sQuery(id+"F2.wireOp",EDGE,"E20.0.3.26"),sQuery(id+"F2.wireOp",EDGE,"E20.0.3.27"),sQuery(id+"F2.wireOp",EDGE,"E20.1.3.0"),sQuery(id+"F2.wireOp",EDGE,"E20.1.3.1"),sQuery(id+"F2.wireOp",EDGE,"E20.1.3.2"),sQuery(id+"F2.wireOp",EDGE,"E20.1.3.3"),sQuery(id+"F2.wireOp",EDGE,"E20.1.3.6"),sQuery(id+"F2.wireOp",EDGE,"E20.1.3.7"),sQuery(id+"F2.wireOp",EDGE,"E20.1.3.9"),sQuery(id+"F2.wireOp",EDGE,"E20.1.3.10"),sQuery(id+"F2.wireOp",EDGE,"E20.1.3.11"),sQuery(id+"F2.wireOp",EDGE,"E20.1.3.13"),sQuery(id+"F2.wireOp",EDGE,"E20.1.3.14"),sQuery(id+"F2.wireOp",EDGE,"E20.1.3.20"),sQuery(id+"F2.wireOp",EDGE,"E20.1.3.21"),sQuery(id+"F2.wireOp",EDGE,"E20.1.3.22"),sQuery(id+"F2.wireOp",EDGE,"E20.1.3.23"),sQuery(id+"F2.wireOp",EDGE,"E20.1.3.24"),sQuery(id+"F2.wireOp",EDGE,"E20.1.3.25"),sQuery(id+"F2.wireOp",EDGE,"E20.1.3.26"),sQuery(id+"F2.wireOp",EDGE,"E20.1.3.27"),sQuery(id+"F2.wireOp",EDGE,"E20.2.3.0"),sQuery(id+"F2.wireOp",EDGE,"E20.2.3.1"),sQuery(id+"F2.wireOp",EDGE,"E20.2.3.2"),sQuery(id+"F2.wireOp",EDGE,"E20.2.3.3"),sQuery(id+"F2.wireOp",EDGE,"E20.2.3.6"),sQuery(id+"F2.wireOp",EDGE,"E20.2.3.7"),sQuery(id+"F2.wireOp",EDGE,"E20.2.3.9"),sQuery(id+"F2.wireOp",EDGE,"E20.2.3.10"),sQuery(id+"F2.wireOp",EDGE,"E20.2.3.11"),sQuery(id+"F2.wireOp",EDGE,"E20.2.3.13"),sQuery(id+"F2.wireOp",EDGE,"E20.2.3.14"),sQuery(id+"F2.wireOp",EDGE,"E20.2.3.20"),sQuery(id+"F2.wireOp",EDGE,"E20.2.3.21"),sQuery(id+"F2.wireOp",EDGE,"E20.2.3.22"),sQuery(id+"F2.wireOp",EDGE,"E20.2.3.23"),sQuery(id+"F2.wireOp",EDGE,"E20.2.3.24"),sQuery(id+"F2.wireOp",EDGE,"E20.2.3.25"),sQuery(id+"F2.wireOp",EDGE,"E20.2.3.26"),sQuery(id+"F2.wireOp",EDGE,"E20.2.3.27"),sQuery(id+"F2.wireOp",EDGE,"E20.3.3.0"),sQuery(id+"F2.wireOp",EDGE,"E20.3.3.1"),sQuery(id+"F2.wireOp",EDGE,"E20.3.3.2"),sQuery(id+"F2.wireOp",EDGE,"E20.3.3.3"),sQuery(id+"F2.wireOp",EDGE,"E20.3.3.6"),sQuery(id+"F2.wireOp",EDGE,"E20.3.3.7"),sQuery(id+"F2.wireOp",EDGE,"E20.3.3.9"),sQuery(id+"F2.wireOp",EDGE,"E20.3.3.10"),sQuery(id+"F2.wireOp",EDGE,"E20.3.3.11"),sQuery(id+"F2.wireOp",EDGE,"E20.3.3.13"),sQuery(id+"F2.wireOp",EDGE,"E20.3.3.14"),sQuery(id+"F2.wireOp",EDGE,"E20.3.3.20"),sQuery(id+"F2.wireOp",EDGE,"E20.3.3.21"),sQuery(id+"F2.wireOp",EDGE,"E20.3.3.22"),sQuery(id+"F2.wireOp",EDGE,"E20.3.3.23"),sQuery(id+"F2.wireOp",EDGE,"E20.3.3.24"),sQuery(id+"F2.wireOp",EDGE,"E20.3.3.25"),sQuery(id+"F2.wireOp",EDGE,"E20.3.3.26"),sQuery(id+"F2.wireOp",EDGE,"E20.3.3.27"),sQuery(id+"F2.wireOp",EDGE,"E20.4.3.0"),sQuery(id+"F2.wireOp",EDGE,"E20.4.3.1"),sQuery(id+"F2.wireOp",EDGE,"E20.4.3.2"),sQuery(id+"F2.wireOp",EDGE,"E20.4.3.3"),sQuery(id+"F2.wireOp",EDGE,"E20.4.3.6"),sQuery(id+"F2.wireOp",EDGE,"E20.4.3.7"),sQuery(id+"F2.wireOp",EDGE,"E20.4.3.9"),sQuery(id+"F2.wireOp",EDGE,"E20.4.3.10"),sQuery(id+"F2.wireOp",EDGE,"E20.4.3.11"),sQuery(id+"F2.wireOp",EDGE,"E20.4.3.13"),sQuery(id+"F2.wireOp",EDGE,"E20.4.3.14"),sQuery(id+"F2.wireOp",EDGE,"E20.4.3.20"),sQuery(id+"F2.wireOp",EDGE,"E20.4.3.21"),sQuery(id+"F2.wireOp",EDGE,"E20.4.3.22"),sQuery(id+"F2.wireOp",EDGE,"E20.4.3.23"),sQuery(id+"F2.wireOp",EDGE,"E20.4.3.24"),sQuery(id+"F2.wireOp",EDGE,"E20.4.3.25"),sQuery(id+"F2.wireOp",EDGE,"E20.4.3.26"),sQuery(id+"F2.wireOp",EDGE,"E20.4.3.27"),sQuery(id+"F2.wireOp",EDGE,"E24.bottom"),sQuery(id+"F2.wireOp",EDGE,"E24.top"),sQuery(id+"F2.wireOp",EDGE,"E24.right")])],"isStart":true}),makeQuery(id+"F3.opExtrude","CAP_FACE",FACE,{"disambiguationData":[OSD([sQuery(id+"F2.wireOp",EDGE,"E20.0.4.0"),sQuery(id+"F2.wireOp",EDGE,"E20.0.4.1"),sQuery(id+"F2.wireOp",EDGE,"E20.0.4.2"),sQuery(id+"F2.wireOp",EDGE,"E20.0.4.3"),sQuery(id+"F2.wireOp",EDGE,"E20.0.4.6"),sQuery(id+"F2.wireOp",EDGE,"E20.0.4.7"),sQuery(id+"F2.wireOp",EDGE,"E20.0.4.9"),sQuery(id+"F2.wireOp",EDGE,"E20.0.4.10"),sQuery(id+"F2.wireOp",EDGE,"E20.0.4.11"),sQuery(id+"F2.wireOp",EDGE,"E20.0.4.12"),sQuery(id+"F2.wireOp",EDGE,"E20.0.4.13"),sQuery(id+"F2.wireOp",EDGE,"E20.0.4.14"),sQuery(id+"F2.wireOp",EDGE,"E20.0.4.20"),sQuery(id+"F2.wireOp",EDGE,"E20.0.4.21"),sQuery(id+"F2.wireOp",EDGE,"E20.0.4.22"),sQuery(id+"F2.wireOp",EDGE,"E20.0.4.23"),sQuery(id+"F2.wireOp",EDGE,"E20.0.4.24"),sQuery(id+"F2.wireOp",EDGE,"E20.0.4.25"),sQuery(id+"F2.wireOp",EDGE,"E20.0.4.26"),sQuery(id+"F2.wireOp",EDGE,"E20.0.4.27"),sQuery(id+"F2.wireOp",EDGE,"E20.1.4.0"),sQuery(id+"F2.wireOp",EDGE,"E20.1.4.1"),sQuery(id+"F2.wireOp",EDGE,"E20.1.4.2"),sQuery(id+"F2.wireOp",EDGE,"E20.1.4.3"),sQuery(id+"F2.wireOp",EDGE,"E20.1.4.6"),sQuery(id+"F2.wireOp",EDGE,"E20.1.4.7"),sQuery(id+"F2.wireOp",EDGE,"E20.1.4.9"),sQuery(id+"F2.wireOp",EDGE,"E20.1.4.10"),sQuery(id+"F2.wireOp",EDGE,"E20.1.4.11"),sQuery(id+"F2.wireOp",EDGE,"E20.1.4.13"),sQuery(id+"F2.wireOp",EDGE,"E20.1.4.14"),sQuery(id+"F2.wireOp",EDGE,"E20.1.4.20"),sQuery(id+"F2.wireOp",EDGE,"E20.1.4.21"),sQuery(id+"F2.wireOp",EDGE,"E20.1.4.22"),sQuery(id+"F2.wireOp",EDGE,"E20.1.4.23"),sQuery(id+"F2.wireOp",EDGE,"E20.1.4.24"),sQuery(id+"F2.wireOp",EDGE,"E20.1.4.25"),sQuery(id+"F2.wireOp",EDGE,"E20.1.4.26"),sQuery(id+"F2.wireOp",EDGE,"E20.1.4.27"),sQuery(id+"F2.wireOp",EDGE,"E20.2.4.0"),sQuery(id+"F2.wireOp",EDGE,"E20.2.4.1"),sQuery(id+"F2.wireOp",EDGE,"E20.2.4.2"),sQuery(id+"F2.wireOp",EDGE,"E20.2.4.3"),sQuery(id+"F2.wireOp",EDGE,"E20.2.4.6"),sQuery(id+"F2.wireOp",EDGE,"E20.2.4.7"),sQuery(id+"F2.wireOp",EDGE,"E20.2.4.9"),sQuery(id+"F2.wireOp",EDGE,"E20.2.4.10"),sQuery(id+"F2.wireOp",EDGE,"E20.2.4.11"),sQuery(id+"F2.wireOp",EDGE,"E20.2.4.13"),sQuery(id+"F2.wireOp",EDGE,"E20.2.4.14"),sQuery(id+"F2.wireOp",EDGE,"E20.2.4.20"),sQuery(id+"F2.wireOp",EDGE,"E20.2.4.21"),sQuery(id+"F2.wireOp",EDGE,"E20.2.4.22"),sQuery(id+"F2.wireOp",EDGE,"E20.2.4.23"),sQuery(id+"F2.wireOp",EDGE,"E20.2.4.24"),sQuery(id+"F2.wireOp",EDGE,"E20.2.4.25"),sQuery(id+"F2.wireOp",EDGE,"E20.2.4.26"),sQuery(id+"F2.wireOp",EDGE,"E20.2.4.27"),sQuery(id+"F2.wireOp",EDGE,"E20.3.4.0"),sQuery(id+"F2.wireOp",EDGE,"E20.3.4.1"),sQuery(id+"F2.wireOp",EDGE,"E20.3.4.2"),sQuery(id+"F2.wireOp",EDGE,"E20.3.4.3"),sQuery(id+"F2.wireOp",EDGE,"E20.3.4.6"),sQuery(id+"F2.wireOp",EDGE,"E20.3.4.7"),sQuery(id+"F2.wireOp",EDGE,"E20.3.4.9"),sQuery(id+"F2.wireOp",EDGE,"E20.3.4.10"),sQuery(id+"F2.wireOp",EDGE,"E20.3.4.11"),sQuery(id+"F2.wireOp",EDGE,"E20.3.4.13"),sQuery(id+"F2.wireOp",EDGE,"E20.3.4.14"),sQuery(id+"F2.wireOp",EDGE,"E20.3.4.20"),sQuery(id+"F2.wireOp",EDGE,"E20.3.4.21"),sQuery(id+"F2.wireOp",EDGE,"E20.3.4.22"),sQuery(id+"F2.wireOp",EDGE,"E20.3.4.23"),sQuery(id+"F2.wireOp",EDGE,"E20.3.4.24"),sQuery(id+"F2.wireOp",EDGE,"E20.3.4.25"),sQuery(id+"F2.wireOp",EDGE,"E20.3.4.26"),sQuery(id+"F2.wireOp",EDGE,"E20.3.4.27"),sQuery(id+"F2.wireOp",EDGE,"E20.4.4.0"),sQuery(id+"F2.wireOp",EDGE,"E20.4.4.1"),sQuery(id+"F2.wireOp",EDGE,"E20.4.4.2"),sQuery(id+"F2.wireOp",EDGE,"E20.4.4.3"),sQuery(id+"F2.wireOp",EDGE,"E20.4.4.6"),sQuery(id+"F2.wireOp",EDGE,"E20.4.4.7"),sQuery(id+"F2.wireOp",EDGE,"E20.4.4.9"),sQuery(id+"F2.wireOp",EDGE,"E20.4.4.10"),sQuery(id+"F2.wireOp",EDGE,"E20.4.4.11"),sQuery(id+"F2.wireOp",EDGE,"E20.4.4.13"),sQuery(id+"F2.wireOp",EDGE,"E20.4.4.14"),sQuery(id+"F2.wireOp",EDGE,"E20.4.4.20"),sQuery(id+"F2.wireOp",EDGE,"E20.4.4.21"),sQuery(id+"F2.wireOp",EDGE,"E20.4.4.22"),sQuery(id+"F2.wireOp",EDGE,"E20.4.4.23"),sQuery(id+"F2.wireOp",EDGE,"E20.4.4.24"),sQuery(id+"F2.wireOp",EDGE,"E20.4.4.25"),sQuery(id+"F2.wireOp",EDGE,"E20.4.4.26"),sQuery(id+"F2.wireOp",EDGE,"E20.4.4.27"),sQuery(id+"F2.wireOp",EDGE,"E25.bottom"),sQuery(id+"F2.wireOp",EDGE,"E25.top"),sQuery(id+"F2.wireOp",EDGE,"E25.right")])],"isStart":true}),makeQuery(id+"F3.opExtrude","CAP_FACE",FACE,{"disambiguationData":[OSD([sQuery(id+"F2.wireOp",EDGE,"E26.1.0.16"),sQuery(id+"F2.wireOp",EDGE,"E26.1.0.17"),sQuery(id+"F2.wireOp",EDGE,"E26.1.0.27"),sQuery(id+"F2.wireOp",EDGE,"E26.1.0.138"),sQuery(id+"F2.wireOp",EDGE,"E26.1.0.198"),sQuery(id+"F2.wireOp",EDGE,"E26.1.0.218"),sQuery(id+"F2.wireOp",EDGE,"E26.1.0.225"),sQuery(id+"F2.wireOp",EDGE,"E26.1.0.238"),sQuery(id+"F2.wireOp",EDGE,"E26.1.0.239"),sQuery(id+"F2.wireOp",EDGE,"E26.1.0.242"),sQuery(id+"F2.wireOp",EDGE,"E26.1.0.250"),sQuery(id+"F2.wireOp",EDGE,"E26.1.0.254"),sQuery(id+"F2.wireOp",EDGE,"E26.1.0.260"),sQuery(id+"F2.wireOp",EDGE,"E26.1.0.261"),sQuery(id+"F2.wireOp",EDGE,"E26.1.0.262"),sQuery(id+"F2.wireOp",EDGE,"E26.1.0.266"),sQuery(id+"F2.wireOp",EDGE,"E26.1.0.271"),sQuery(id+"F2.wireOp",EDGE,"E26.1.0.274"),sQuery(id+"F2.wireOp",EDGE,"E26.1.0.283"),sQuery(id+"F2.wireOp",EDGE,"E26.1.0.284"),sQuery(id+"F2.wireOp",EDGE,"E26.1.0.287"),sQuery(id+"F2.wireOp",EDGE,"E26.1.0.294"),sQuery(id+"F2.wireOp",EDGE,"E26.1.0.310"),sQuery(id+"F2.wireOp",EDGE,"E26.1.0.312"),sQuery(id+"F2.wireOp",EDGE,"E26.1.0.319"),sQuery(id+"F2.wireOp",EDGE,"E26.1.0.329"),sQuery(id+"F2.wireOp",EDGE,"E26.1.0.332"),sQuery(id+"F2.wireOp",EDGE,"E26.1.0.335"),sQuery(id+"F2.wireOp",EDGE,"E26.1.0.340"),sQuery(id+"F2.wireOp",EDGE,"E26.1.0.377"),sQuery(id+"F2.wireOp",EDGE,"E26.1.0.379"),sQuery(id+"F2.wireOp",EDGE,"E26.1.0.384"),sQuery(id+"F2.wireOp",EDGE,"E26.1.0.387"),sQuery(id+"F2.wireOp",EDGE,"E26.1.0.388"),sQuery(id+"F2.wireOp",EDGE,"E26.1.0.389"),sQuery(id+"F2.wireOp",EDGE,"E26.1.0.394"),sQuery(id+"F2.wireOp",EDGE,"E26.1.0.395"),sQuery(id+"F2.wireOp",EDGE,"E26.1.0.397"),sQuery(id+"F2.wireOp",EDGE,"E26.1.0.401"),sQuery(id+"F2.wireOp",EDGE,"E26.1.0.402"),sQuery(id+"F2.wireOp",EDGE,"E26.1.0.415"),sQuery(id+"F2.wireOp",EDGE,"E26.1.0.419"),sQuery(id+"F2.wireOp",EDGE,"E26.1.0.422"),sQuery(id+"F2.wireOp",EDGE,"E26.1.0.423"),sQuery(id+"F2.wireOp",EDGE,"E26.1.0.449"),sQuery(id+"F2.wireOp",EDGE,"E26.1.0.451"),sQuery(id+"F2.wireOp",EDGE,"E26.1.0.459"),sQuery(id+"F2.wireOp",EDGE,"E26.1.0.462"),sQuery(id+"F2.wireOp",EDGE,"E26.1.0.468"),sQuery(id+"F2.wireOp",EDGE,"E26.1.0.478"),sQuery(id+"F2.wireOp",EDGE,"E26.1.0.485"),sQuery(id+"F2.wireOp",EDGE,"E26.1.0.491"),sQuery(id+"F2.wireOp",EDGE,"E26.1.0.496"),sQuery(id+"F2.wireOp",EDGE,"E26.1.0.505"),sQuery(id+"F2.wireOp",EDGE,"E26.1.0.512"),sQuery(id+"F2.wireOp",EDGE,"E26.1.0.513"),sQuery(id+"F2.wireOp",EDGE,"E26.1.0.514"),sQuery(id+"F2.wireOp",EDGE,"E26.1.0.515"),sQuery(id+"F2.wireOp",EDGE,"E26.1.0.517"),sQuery(id+"F2.wireOp",EDGE,"E26.1.0.523"),sQuery(id+"F2.wireOp",EDGE,"E26.1.0.525"),sQuery(id+"F2.wireOp",EDGE,"E26.1.0.526"),sQuery(id+"F2.wireOp",EDGE,"E26.1.0.546"),sQuery(id+"F2.wireOp",EDGE,"E26.1.0.547"),sQuery(id+"F2.wireOp",EDGE,"E26.1.0.550"),sQuery(id+"F2.wireOp",EDGE,"E26.1.0.553"),sQuery(id+"F2.wireOp",EDGE,"E26.1.0.557"),sQuery(id+"F2.wireOp",EDGE,"E26.1.0.558"),sQuery(id+"F2.wireOp",EDGE,"E26.1.0.570"),sQuery(id+"F2.wireOp",EDGE,"E26.1.0.582"),sQuery(id+"F2.wireOp",EDGE,"E26.1.0.592"),sQuery(id+"F2.wireOp",EDGE,"E26.1.0.593"),sQuery(id+"F2.wireOp",EDGE,"E26.1.0.605"),sQuery(id+"F2.wireOp",EDGE,"E26.1.0.607"),sQuery(id+"F2.wireOp",EDGE,"E26.1.0.610"),sQuery(id+"F2.wireOp",EDGE,"E26.1.0.612"),sQuery(id+"F2.wireOp",EDGE,"E26.1.0.617"),sQuery(id+"F2.wireOp",EDGE,"E26.1.0.619"),sQuery(id+"F2.wireOp",EDGE,"E26.1.0.625"),sQuery(id+"F2.wireOp",EDGE,"E26.1.0.626"),sQuery(id+"F2.wireOp",EDGE,"E26.1.0.633"),sQuery(id+"F2.wireOp",EDGE,"E26.1.0.639"),sQuery(id+"F2.wireOp",EDGE,"E26.1.0.645"),sQuery(id+"F2.wireOp",EDGE,"E26.1.0.646"),sQuery(id+"F2.wireOp",EDGE,"E26.1.0.654"),sQuery(id+"F2.wireOp",EDGE,"E26.1.0.659"),sQuery(id+"F2.wireOp",EDGE,"E26.1.0.662"),sQuery(id+"F2.wireOp",EDGE,"E26.1.0.663"),sQuery(id+"F2.wireOp",EDGE,"E26.1.0.668"),sQuery(id+"F2.wireOp",EDGE,"E26.1.0.673"),sQuery(id+"F2.wireOp",EDGE,"E26.1.0.674"),sQuery(id+"F2.wireOp",EDGE,"E26.1.0.675"),sQuery(id+"F2.wireOp",EDGE,"E26.1.0.686"),sQuery(id+"F2.wireOp",EDGE,"E26.1.0.691"),sQuery(id+"F2.wireOp",EDGE,"E26.1.0.693"),sQuery(id+"F2.wireOp",EDGE,"E26.1.0.702"),sQuery(id+"F2.wireOp",EDGE,"E26.1.0.710"),sQuery(id+"F2.wireOp",EDGE,"E26.1.0.716"),sQuery(id+"F2.wireOp",EDGE,"E26.1.0.717")])],"isStart":true}),makeQuery(id+"F3.opExtrude","CAP_FACE",FACE,{"disambiguationData":[OSD([sQuery(id+"F2.wireOp",EDGE,"E26.1.0.25"),sQuery(id+"F2.wireOp",EDGE,"E26.1.0.71"),sQuery(id+"F2.wireOp",EDGE,"E26.1.0.190"),sQuery(id+"F2.wireOp",EDGE,"E26.1.0.207"),sQuery(id+"F2.wireOp",EDGE,"E26.1.0.210"),sQuery(id+"F2.wireOp",EDGE,"E26.1.0.216"),sQuery(id+"F2.wireOp",EDGE,"E26.1.0.220"),sQuery(id+"F2.wireOp",EDGE,"E26.1.0.264"),sQuery(id+"F2.wireOp",EDGE,"E26.1.0.265"),sQuery(id+"F2.wireOp",EDGE,"E26.1.0.269"),sQuery(id+"F2.wireOp",EDGE,"E26.1.0.270"),sQuery(id+"F2.wireOp",EDGE,"E26.1.0.275"),sQuery(id+"F2.wireOp",EDGE,"E26.1.0.281"),sQuery(id+"F2.wireOp",EDGE,"E26.1.0.297"),sQuery(id+"F2.wireOp",EDGE,"E26.1.0.300"),sQuery(id+"F2.wireOp",EDGE,"E26.1.0.301"),sQuery(id+"F2.wireOp",EDGE,"E26.1.0.303"),sQuery(id+"F2.wireOp",EDGE,"E26.1.0.309"),sQuery(id+"F2.wireOp",EDGE,"E26.1.0.311"),sQuery(id+"F2.wireOp",EDGE,"E26.1.0.313"),sQuery(id+"F2.wireOp",EDGE,"E26.1.0.323"),sQuery(id+"F2.wireOp",EDGE,"E26.1.0.328"),sQuery(id+"F2.wireOp",EDGE,"E26.1.0.330"),sQuery(id+"F2.wireOp",EDGE,"E26.1.0.331"),sQuery(id+"F2.wireOp",EDGE,"E26.1.0.348"),sQuery(id+"F2.wireOp",EDGE,"E26.1.0.350"),sQuery(id+"F2.wireOp",EDGE,"E26.1.0.362"),sQuery(id+"F2.wireOp",EDGE,"E26.1.0.365"),sQuery(id+"F2.wireOp",EDGE,"E26.1.0.367"),sQuery(id+"F2.wireOp",EDGE,"E26.1.0.371"),sQuery(id+"F2.wireOp",EDGE,"E26.1.0.374"),sQuery(id+"F2.wireOp",EDGE,"E26.1.0.380"),sQuery(id+"F2.wireOp",EDGE,"E26.1.0.381"),sQuery(id+"F2.wireOp",EDGE,"E26.1.0.390"),sQuery(id+"F2.wireOp",EDGE,"E26.1.0.403"),sQuery(id+"F2.wireOp",EDGE,"E26.1.0.408"),sQuery(id+"F2.wireOp",EDGE,"E26.1.0.413"),sQuery(id+"F2.wireOp",EDGE,"E26.1.0.416"),sQuery(id+"F2.wireOp",EDGE,"E26.1.0.417"),sQuery(id+"F2.wireOp",EDGE,"E26.1.0.426"),sQuery(id+"F2.wireOp",EDGE,"E26.1.0.427"),sQuery(id+"F2.wireOp",EDGE,"E26.1.0.428"),sQuery(id+"F2.wireOp",EDGE,"E26.1.0.429"),sQuery(id+"F2.wireOp",EDGE,"E26.1.0.433"),sQuery(id+"F2.wireOp",EDGE,"E26.1.0.434"),sQuery(id+"F2.wireOp",EDGE,"E26.1.0.436"),sQuery(id+"F2.wireOp",EDGE,"E26.1.0.438"),sQuery(id+"F2.wireOp",EDGE,"E26.1.0.442"),sQuery(id+"F2.wireOp",EDGE,"E26.1.0.445"),sQuery(id+"F2.wireOp",EDGE,"E26.1.0.447"),sQuery(id+"F2.wireOp",EDGE,"E26.1.0.454"),sQuery(id+"F2.wireOp",EDGE,"E26.1.0.455"),sQuery(id+"F2.wireOp",EDGE,"E26.1.0.460"),sQuery(id+"F2.wireOp",EDGE,"E26.1.0.461"),sQuery(id+"F2.wireOp",EDGE,"E26.1.0.466"),sQuery(id+"F2.wireOp",EDGE,"E26.1.0.469"),sQuery(id+"F2.wireOp",EDGE,"E26.1.0.470"),sQuery(id+"F2.wireOp",EDGE,"E26.1.0.472"),sQuery(id+"F2.wireOp",EDGE,"E26.1.0.474"),sQuery(id+"F2.wireOp",EDGE,"E26.1.0.476"),sQuery(id+"F2.wireOp",EDGE,"E26.1.0.477"),sQuery(id+"F2.wireOp",EDGE,"E26.1.0.480"),sQuery(id+"F2.wireOp",EDGE,"E26.1.0.490"),sQuery(id+"F2.wireOp",EDGE,"E26.1.0.493"),sQuery(id+"F2.wireOp",EDGE,"E26.1.0.495"),sQuery(id+"F2.wireOp",EDGE,"E26.1.0.502"),sQuery(id+"F2.wireOp",EDGE,"E26.1.0.509"),sQuery(id+"F2.wireOp",EDGE,"E26.1.0.511"),sQuery(id+"F2.wireOp",EDGE,"E26.1.0.520"),sQuery(id+"F2.wireOp",EDGE,"E26.1.0.528"),sQuery(id+"F2.wireOp",EDGE,"E26.1.0.530"),sQuery(id+"F2.wireOp",EDGE,"E26.1.0.534"),sQuery(id+"F2.wireOp",EDGE,"E26.1.0.551"),sQuery(id+"F2.wireOp",EDGE,"E26.1.0.552"),sQuery(id+"F2.wireOp",EDGE,"E26.1.0.555"),sQuery(id+"F2.wireOp",EDGE,"E26.1.0.561"),sQuery(id+"F2.wireOp",EDGE,"E26.1.0.564"),sQuery(id+"F2.wireOp",EDGE,"E26.1.0.577"),sQuery(id+"F2.wireOp",EDGE,"E26.1.0.579"),sQuery(id+"F2.wireOp",EDGE,"E26.1.0.599"),sQuery(id+"F2.wireOp",EDGE,"E26.1.0.611"),sQuery(id+"F2.wireOp",EDGE,"E26.1.0.634"),sQuery(id+"F2.wireOp",EDGE,"E26.1.0.635"),sQuery(id+"F2.wireOp",EDGE,"E26.1.0.636"),sQuery(id+"F2.wireOp",EDGE,"E26.1.0.638"),sQuery(id+"F2.wireOp",EDGE,"E26.1.0.644"),sQuery(id+"F2.wireOp",EDGE,"E26.1.0.650"),sQuery(id+"F2.wireOp",EDGE,"E26.1.0.655"),sQuery(id+"F2.wireOp",EDGE,"E26.1.0.660"),sQuery(id+"F2.wireOp",EDGE,"E26.1.0.666"),sQuery(id+"F2.wireOp",EDGE,"E26.1.0.667"),sQuery(id+"F2.wireOp",EDGE,"E26.1.0.677"),sQuery(id+"F2.wireOp",EDGE,"E26.1.0.680"),sQuery(id+"F2.wireOp",EDGE,"E26.1.0.696"),sQuery(id+"F2.wireOp",EDGE,"E26.1.0.697"),sQuery(id+"F2.wireOp",EDGE,"E26.1.0.700"),sQuery(id+"F2.wireOp",EDGE,"E26.1.0.704"),sQuery(id+"F2.wireOp",EDGE,"E26.1.0.719"),sQuery(id+"F2.wireOp",EDGE,"E26.1.0.721")])],"isStart":true}),makeQuery(id+"F3.opExtrude","CAP_FACE",FACE,{"disambiguationData":[OSD([sQuery(id+"F2.wireOp",EDGE,"E26.1.0.31"),sQuery(id+"F2.wireOp",EDGE,"E26.1.0.66"),sQuery(id+"F2.wireOp",EDGE,"E26.1.0.147"),sQuery(id+"F2.wireOp",EDGE,"E26.1.0.149"),sQuery(id+"F2.wireOp",EDGE,"E26.1.0.194"),sQuery(id+"F2.wireOp",EDGE,"E26.1.0.197"),sQuery(id+"F2.wireOp",EDGE,"E26.1.0.204"),sQuery(id+"F2.wireOp",EDGE,"E26.1.0.217"),sQuery(id+"F2.wireOp",EDGE,"E26.1.0.228"),sQuery(id+"F2.wireOp",EDGE,"E26.1.0.243"),sQuery(id+"F2.wireOp",EDGE,"E26.1.0.255"),sQuery(id+"F2.wireOp",EDGE,"E26.1.0.263"),sQuery(id+"F2.wireOp",EDGE,"E26.1.0.282"),sQuery(id+"F2.wireOp",EDGE,"E26.1.0.289"),sQuery(id+"F2.wireOp",EDGE,"E26.1.0.290"),sQuery(id+"F2.wireOp",EDGE,"E26.1.0.291"),sQuery(id+"F2.wireOp",EDGE,"E26.1.0.293"),sQuery(id+"F2.wireOp",EDGE,"E26.1.0.295"),sQuery(id+"F2.wireOp",EDGE,"E26.1.0.296"),sQuery(id+"F2.wireOp",EDGE,"E26.1.0.299"),sQuery(id+"F2.wireOp",EDGE,"E26.1.0.305"),sQuery(id+"F2.wireOp",EDGE,"E26.1.0.315"),sQuery(id+"F2.wireOp",EDGE,"E26.1.0.318"),sQuery(id+"F2.wireOp",EDGE,"E26.1.0.321"),sQuery(id+"F2.wireOp",EDGE,"E26.1.0.334"),sQuery(id+"F2.wireOp",EDGE,"E26.1.0.338"),sQuery(id+"F2.wireOp",EDGE,"E26.1.0.349"),sQuery(id+"F2.wireOp",EDGE,"E26.1.0.351"),sQuery(id+"F2.wireOp",EDGE,"E26.1.0.354"),sQuery(id+"F2.wireOp",EDGE,"E26.1.0.359"),sQuery(id+"F2.wireOp",EDGE,"E26.1.0.363"),sQuery(id+"F2.wireOp",EDGE,"E26.1.0.368"),sQuery(id+"F2.wireOp",EDGE,"E26.1.0.370"),sQuery(id+"F2.wireOp",EDGE,"E26.1.0.373"),sQuery(id+"F2.wireOp",EDGE,"E26.1.0.376"),sQuery(id+"F2.wireOp",EDGE,"E26.1.0.383"),sQuery(id+"F2.wireOp",EDGE,"E26.1.0.386"),sQuery(id+"F2.wireOp",EDGE,"E26.1.0.400"),sQuery(id+"F2.wireOp",EDGE,"E26.1.0.406"),sQuery(id+"F2.wireOp",EDGE,"E26.1.0.407"),sQuery(id+"F2.wireOp",EDGE,"E26.1.0.411"),sQuery(id+"F2.wireOp",EDGE,"E26.1.0.414"),sQuery(id+"F2.wireOp",EDGE,"E26.1.0.425"),sQuery(id+"F2.wireOp",EDGE,"E26.1.0.440"),sQuery(id+"F2.wireOp",EDGE,"E26.1.0.448"),sQuery(id+"F2.wireOp",EDGE,"E26.1.0.453"),sQuery(id+"F2.wireOp",EDGE,"E26.1.0.458"),sQuery(id+"F2.wireOp",EDGE,"E26.1.0.465"),sQuery(id+"F2.wireOp",EDGE,"E26.1.0.467"),sQuery(id+"F2.wireOp",EDGE,"E26.1.0.473"),sQuery(id+"F2.wireOp",EDGE,"E26.1.0.484"),sQuery(id+"F2.wireOp",EDGE,"E26.1.0.487"),sQuery(id+"F2.wireOp",EDGE,"E26.1.0.492"),sQuery(id+"F2.wireOp",EDGE,"E26.1.0.494"),sQuery(id+"F2.wireOp",EDGE,"E26.1.0.499"),sQuery(id+"F2.wireOp",EDGE,"E26.1.0.529"),sQuery(id+"F2.wireOp",EDGE,"E26.1.0.542"),sQuery(id+"F2.wireOp",EDGE,"E26.1.0.554"),sQuery(id+"F2.wireOp",EDGE,"E26.1.0.556"),sQuery(id+"F2.wireOp",EDGE,"E26.1.0.560"),sQuery(id+"F2.wireOp",EDGE,"E26.1.0.566"),sQuery(id+"F2.wireOp",EDGE,"E26.1.0.569"),sQuery(id+"F2.wireOp",EDGE,"E26.1.0.572"),sQuery(id+"F2.wireOp",EDGE,"E26.1.0.574"),sQuery(id+"F2.wireOp",EDGE,"E26.1.0.576"),sQuery(id+"F2.wireOp",EDGE,"E26.1.0.578"),sQuery(id+"F2.wireOp",EDGE,"E26.1.0.583"),sQuery(id+"F2.wireOp",EDGE,"E26.1.0.586"),sQuery(id+"F2.wireOp",EDGE,"E26.1.0.587"),sQuery(id+"F2.wireOp",EDGE,"E26.1.0.588"),sQuery(id+"F2.wireOp",EDGE,"E26.1.0.591"),sQuery(id+"F2.wireOp",EDGE,"E26.1.0.595"),sQuery(id+"F2.wireOp",EDGE,"E26.1.0.598"),sQuery(id+"F2.wireOp",EDGE,"E26.1.0.601"),sQuery(id+"F2.wireOp",EDGE,"E26.1.0.602"),sQuery(id+"F2.wireOp",EDGE,"E26.1.0.606"),sQuery(id+"F2.wireOp",EDGE,"E26.1.0.609"),sQuery(id+"F2.wireOp",EDGE,"E26.1.0.614"),sQuery(id+"F2.wireOp",EDGE,"E26.1.0.616"),sQuery(id+"F2.wireOp",EDGE,"E26.1.0.621"),sQuery(id+"F2.wireOp",EDGE,"E26.1.0.622"),sQuery(id+"F2.wireOp",EDGE,"E26.1.0.623"),sQuery(id+"F2.wireOp",EDGE,"E26.1.0.627"),sQuery(id+"F2.wireOp",EDGE,"E26.1.0.628"),sQuery(id+"F2.wireOp",EDGE,"E26.1.0.631"),sQuery(id+"F2.wireOp",EDGE,"E26.1.0.632"),sQuery(id+"F2.wireOp",EDGE,"E26.1.0.648"),sQuery(id+"F2.wireOp",EDGE,"E26.1.0.651"),sQuery(id+"F2.wireOp",EDGE,"E26.1.0.657"),sQuery(id+"F2.wireOp",EDGE,"E26.1.0.679"),sQuery(id+"F2.wireOp",EDGE,"E26.1.0.683"),sQuery(id+"F2.wireOp",EDGE,"E26.1.0.685"),sQuery(id+"F2.wireOp",EDGE,"E26.1.0.687"),sQuery(id+"F2.wireOp",EDGE,"E26.1.0.688"),sQuery(id+"F2.wireOp",EDGE,"E26.1.0.689"),sQuery(id+"F2.wireOp",EDGE,"E26.1.0.703"),sQuery(id+"F2.wireOp",EDGE,"E26.1.0.706"),sQuery(id+"F2.wireOp",EDGE,"E26.1.0.707"),sQuery(id+"F2.wireOp",EDGE,"E26.1.0.711")])],"isStart":true}),makeQuery(id+"F3.opExtrude","CAP_FACE",FACE,{"disambiguationData":[OSD([sQuery(id+"F2.wireOp",EDGE,"E26.1.0.113"),sQuery(id+"F2.wireOp",EDGE,"E26.1.0.117"),sQuery(id+"F2.wireOp",EDGE,"E26.1.0.144"),sQuery(id+"F2.wireOp",EDGE,"E26.1.0.171"),sQuery(id+"F2.wireOp",EDGE,"E26.1.0.191"),sQuery(id+"F2.wireOp",EDGE,"E26.1.0.202"),sQuery(id+"F2.wireOp",EDGE,"E26.1.0.203"),sQuery(id+"F2.wireOp",EDGE,"E26.1.0.214"),sQuery(id+"F2.wireOp",EDGE,"E26.1.0.222"),sQuery(id+"F2.wireOp",EDGE,"E26.1.0.244"),sQuery(id+"F2.wireOp",EDGE,"E26.1.0.251"),sQuery(id+"F2.wireOp",EDGE,"E26.1.0.258"),sQuery(id+"F2.wireOp",EDGE,"E26.1.0.277"),sQuery(id+"F2.wireOp",EDGE,"E26.1.0.278"),sQuery(id+"F2.wireOp",EDGE,"E26.1.0.279"),sQuery(id+"F2.wireOp",EDGE,"E26.1.0.280"),sQuery(id+"F2.wireOp",EDGE,"E26.1.0.302"),sQuery(id+"F2.wireOp",EDGE,"E26.1.0.304"),sQuery(id+"F2.wireOp",EDGE,"E26.1.0.306"),sQuery(id+"F2.wireOp",EDGE,"E26.1.0.307"),sQuery(id+"F2.wireOp",EDGE,"E26.1.0.308"),sQuery(id+"F2.wireOp",EDGE,"E26.1.0.316"),sQuery(id+"F2.wireOp",EDGE,"E26.1.0.317"),sQuery(id+"F2.wireOp",EDGE,"E26.1.0.324"),sQuery(id+"F2.wireOp",EDGE,"E26.1.0.326"),sQuery(id+"F2.wireOp",EDGE,"E26.1.0.333"),sQuery(id+"F2.wireOp",EDGE,"E26.1.0.339"),sQuery(id+"F2.wireOp",EDGE,"E26.1.0.341"),sQuery(id+"F2.wireOp",EDGE,"E26.1.0.345"),sQuery(id+"F2.wireOp",EDGE,"E26.1.0.360"),sQuery(id+"F2.wireOp",EDGE,"E26.1.0.364"),sQuery(id+"F2.wireOp",EDGE,"E26.1.0.366"),sQuery(id+"F2.wireOp",EDGE,"E26.1.0.375"),sQuery(id+"F2.wireOp",EDGE,"E26.1.0.392"),sQuery(id+"F2.wireOp",EDGE,"E26.1.0.393"),sQuery(id+"F2.wireOp",EDGE,"E26.1.0.396"),sQuery(id+"F2.wireOp",EDGE,"E26.1.0.404"),sQuery(id+"F2.wireOp",EDGE,"E26.1.0.409"),sQuery(id+"F2.wireOp",EDGE,"E26.1.0.410"),sQuery(id+"F2.wireOp",EDGE,"E26.1.0.412"),sQuery(id+"F2.wireOp",EDGE,"E26.1.0.418"),sQuery(id+"F2.wireOp",EDGE,"E26.1.0.420"),sQuery(id+"F2.wireOp",EDGE,"E26.1.0.424"),sQuery(id+"F2.wireOp",EDGE,"E26.1.0.431"),sQuery(id+"F2.wireOp",EDGE,"E26.1.0.432"),sQuery(id+"F2.wireOp",EDGE,"E26.1.0.437"),sQuery(id+"F2.wireOp",EDGE,"E26.1.0.443"),sQuery(id+"F2.wireOp",EDGE,"E26.1.0.446"),sQuery(id+"F2.wireOp",EDGE,"E26.1.0.452"),sQuery(id+"F2.wireOp",EDGE,"E26.1.0.456"),sQuery(id+"F2.wireOp",EDGE,"E26.1.0.464"),sQuery(id+"F2.wireOp",EDGE,"E26.1.0.471"),sQuery(id+"F2.wireOp",EDGE,"E26.1.0.479"),sQuery(id+"F2.wireOp",EDGE,"E26.1.0.482"),sQuery(id+"F2.wireOp",EDGE,"E26.1.0.483"),sQuery(id+"F2.wireOp",EDGE,"E26.1.0.486"),sQuery(id+"F2.wireOp",EDGE,"E26.1.0.497"),sQuery(id+"F2.wireOp",EDGE,"E26.1.0.498"),sQuery(id+"F2.wireOp",EDGE,"E26.1.0.500"),sQuery(id+"F2.wireOp",EDGE,"E26.1.0.501"),sQuery(id+"F2.wireOp",EDGE,"E26.1.0.503"),sQuery(id+"F2.wireOp",EDGE,"E26.1.0.504"),sQuery(id+"F2.wireOp",EDGE,"E26.1.0.506"),sQuery(id+"F2.wireOp",EDGE,"E26.1.0.507"),sQuery(id+"F2.wireOp",EDGE,"E26.1.0.510"),sQuery(id+"F2.wireOp",EDGE,"E26.1.0.516"),sQuery(id+"F2.wireOp",EDGE,"E26.1.0.518"),sQuery(id+"F2.wireOp",EDGE,"E26.1.0.527"),sQuery(id+"F2.wireOp",EDGE,"E26.1.0.533"),sQuery(id+"F2.wireOp",EDGE,"E26.1.0.535"),sQuery(id+"F2.wireOp",EDGE,"E26.1.0.537"),sQuery(id+"F2.wireOp",EDGE,"E26.1.0.538"),sQuery(id+"F2.wireOp",EDGE,"E26.1.0.539"),sQuery(id+"F2.wireOp",EDGE,"E26.1.0.541"),sQuery(id+"F2.wireOp",EDGE,"E26.1.0.543"),sQuery(id+"F2.wireOp",EDGE,"E26.1.0.544"),sQuery(id+"F2.wireOp",EDGE,"E26.1.0.545"),sQuery(id+"F2.wireOp",EDGE,"E26.1.0.568"),sQuery(id+"F2.wireOp",EDGE,"E26.1.0.575"),sQuery(id+"F2.wireOp",EDGE,"E26.1.0.584"),sQuery(id+"F2.wireOp",EDGE,"E26.1.0.589"),sQuery(id+"F2.wireOp",EDGE,"E26.1.0.600"),sQuery(id+"F2.wireOp",EDGE,"E26.1.0.603"),sQuery(id+"F2.wireOp",EDGE,"E26.1.0.615"),sQuery(id+"F2.wireOp",EDGE,"E26.1.0.620"),sQuery(id+"F2.wireOp",EDGE,"E26.1.0.640"),sQuery(id+"F2.wireOp",EDGE,"E26.1.0.647"),sQuery(id+"F2.wireOp",EDGE,"E26.1.0.664"),sQuery(id+"F2.wireOp",EDGE,"E26.1.0.676"),sQuery(id+"F2.wireOp",EDGE,"E26.1.0.681"),sQuery(id+"F2.wireOp",EDGE,"E26.1.0.684"),sQuery(id+"F2.wireOp",EDGE,"E26.1.0.692"),sQuery(id+"F2.wireOp",EDGE,"E26.1.0.694"),sQuery(id+"F2.wireOp",EDGE,"E26.1.0.698"),sQuery(id+"F2.wireOp",EDGE,"E26.1.0.699"),sQuery(id+"F2.wireOp",EDGE,"E26.1.0.701"),sQuery(id+"F2.wireOp",EDGE,"E26.1.0.705"),sQuery(id+"F2.wireOp",EDGE,"E26.1.0.714"),sQuery(id+"F2.wireOp",EDGE,"E26.1.0.718")])],"isStart":true}),makeQuery(id+"F3.opExtrude","CAP_FACE",FACE,{"disambiguationData":[OSD([sQuery(id+"F2.wireOp",EDGE,"E26.1.0.151"),sQuery(id+"F2.wireOp",EDGE,"E26.1.0.168"),sQuery(id+"F2.wireOp",EDGE,"E26.1.0.178"),sQuery(id+"F2.wireOp",EDGE,"E26.1.0.181"),sQuery(id+"F2.wireOp",EDGE,"E26.1.0.192"),sQuery(id+"F2.wireOp",EDGE,"E26.1.0.221"),sQuery(id+"F2.wireOp",EDGE,"E26.1.0.227"),sQuery(id+"F2.wireOp",EDGE,"E26.1.0.229"),sQuery(id+"F2.wireOp",EDGE,"E26.1.0.235"),sQuery(id+"F2.wireOp",EDGE,"E26.1.0.248"),sQuery(id+"F2.wireOp",EDGE,"E26.1.0.249"),sQuery(id+"F2.wireOp",EDGE,"E26.1.0.253"),sQuery(id+"F2.wireOp",EDGE,"E26.1.0.256"),sQuery(id+"F2.wireOp",EDGE,"E26.1.0.259"),sQuery(id+"F2.wireOp",EDGE,"E26.1.0.268"),sQuery(id+"F2.wireOp",EDGE,"E26.1.0.273"),sQuery(id+"F2.wireOp",EDGE,"E26.1.0.276"),sQuery(id+"F2.wireOp",EDGE,"E26.1.0.286"),sQuery(id+"F2.wireOp",EDGE,"E26.1.0.288"),sQuery(id+"F2.wireOp",EDGE,"E26.1.0.314"),sQuery(id+"F2.wireOp",EDGE,"E26.1.0.320"),sQuery(id+"F2.wireOp",EDGE,"E26.1.0.322"),sQuery(id+"F2.wireOp",EDGE,"E26.1.0.325"),sQuery(id+"F2.wireOp",EDGE,"E26.1.0.337"),sQuery(id+"F2.wireOp",EDGE,"E26.1.0.343"),sQuery(id+"F2.wireOp",EDGE,"E26.1.0.347"),sQuery(id+"F2.wireOp",EDGE,"E26.1.0.353"),sQuery(id+"F2.wireOp",EDGE,"E26.1.0.355"),sQuery(id+"F2.wireOp",EDGE,"E26.1.0.356"),sQuery(id+"F2.wireOp",EDGE,"E26.1.0.369"),sQuery(id+"F2.wireOp",EDGE,"E26.1.0.372"),sQuery(id+"F2.wireOp",EDGE,"E26.1.0.378"),sQuery(id+"F2.wireOp",EDGE,"E26.1.0.382"),sQuery(id+"F2.wireOp",EDGE,"E26.1.0.385"),sQuery(id+"F2.wireOp",EDGE,"E26.1.0.391"),sQuery(id+"F2.wireOp",EDGE,"E26.1.0.399"),sQuery(id+"F2.wireOp",EDGE,"E26.1.0.405"),sQuery(id+"F2.wireOp",EDGE,"E26.1.0.421"),sQuery(id+"F2.wireOp",EDGE,"E26.1.0.430"),sQuery(id+"F2.wireOp",EDGE,"E26.1.0.435"),sQuery(id+"F2.wireOp",EDGE,"E26.1.0.439"),sQuery(id+"F2.wireOp",EDGE,"E26.1.0.444"),sQuery(id+"F2.wireOp",EDGE,"E26.1.0.450"),sQuery(id+"F2.wireOp",EDGE,"E26.1.0.457"),sQuery(id+"F2.wireOp",EDGE,"E26.1.0.463"),sQuery(id+"F2.wireOp",EDGE,"E26.1.0.489"),sQuery(id+"F2.wireOp",EDGE,"E26.1.0.508"),sQuery(id+"F2.wireOp",EDGE,"E26.1.0.521"),sQuery(id+"F2.wireOp",EDGE,"E26.1.0.522"),sQuery(id+"F2.wireOp",EDGE,"E26.1.0.524"),sQuery(id+"F2.wireOp",EDGE,"E26.1.0.531"),sQuery(id+"F2.wireOp",EDGE,"E26.1.0.540"),sQuery(id+"F2.wireOp",EDGE,"E26.1.0.548"),sQuery(id+"F2.wireOp",EDGE,"E26.1.0.559"),sQuery(id+"F2.wireOp",EDGE,"E26.1.0.562"),sQuery(id+"F2.wireOp",EDGE,"E26.1.0.563"),sQuery(id+"F2.wireOp",EDGE,"E26.1.0.565"),sQuery(id+"F2.wireOp",EDGE,"E26.1.0.567"),sQuery(id+"F2.wireOp",EDGE,"E26.1.0.571"),sQuery(id+"F2.wireOp",EDGE,"E26.1.0.573"),sQuery(id+"F2.wireOp",EDGE,"E26.1.0.580"),sQuery(id+"F2.wireOp",EDGE,"E26.1.0.581"),sQuery(id+"F2.wireOp",EDGE,"E26.1.0.585"),sQuery(id+"F2.wireOp",EDGE,"E26.1.0.590"),sQuery(id+"F2.wireOp",EDGE,"E26.1.0.594"),sQuery(id+"F2.wireOp",EDGE,"E26.1.0.596"),sQuery(id+"F2.wireOp",EDGE,"E26.1.0.597"),sQuery(id+"F2.wireOp",EDGE,"E26.1.0.604"),sQuery(id+"F2.wireOp",EDGE,"E26.1.0.608"),sQuery(id+"F2.wireOp",EDGE,"E26.1.0.613"),sQuery(id+"F2.wireOp",EDGE,"E26.1.0.618"),sQuery(id+"F2.wireOp",EDGE,"E26.1.0.624"),sQuery(id+"F2.wireOp",EDGE,"E26.1.0.629"),sQuery(id+"F2.wireOp",EDGE,"E26.1.0.630"),sQuery(id+"F2.wireOp",EDGE,"E26.1.0.637"),sQuery(id+"F2.wireOp",EDGE,"E26.1.0.641"),sQuery(id+"F2.wireOp",EDGE,"E26.1.0.642"),sQuery(id+"F2.wireOp",EDGE,"E26.1.0.643"),sQuery(id+"F2.wireOp",EDGE,"E26.1.0.649"),sQuery(id+"F2.wireOp",EDGE,"E26.1.0.652"),sQuery(id+"F2.wireOp",EDGE,"E26.1.0.653"),sQuery(id+"F2.wireOp",EDGE,"E26.1.0.656"),sQuery(id+"F2.wireOp",EDGE,"E26.1.0.658"),sQuery(id+"F2.wireOp",EDGE,"E26.1.0.661"),sQuery(id+"F2.wireOp",EDGE,"E26.1.0.665"),sQuery(id+"F2.wireOp",EDGE,"E26.1.0.669"),sQuery(id+"F2.wireOp",EDGE,"E26.1.0.670"),sQuery(id+"F2.wireOp",EDGE,"E26.1.0.671"),sQuery(id+"F2.wireOp",EDGE,"E26.1.0.672"),sQuery(id+"F2.wireOp",EDGE,"E26.1.0.678"),sQuery(id+"F2.wireOp",EDGE,"E26.1.0.682"),sQuery(id+"F2.wireOp",EDGE,"E26.1.0.690"),sQuery(id+"F2.wireOp",EDGE,"E26.1.0.695"),sQuery(id+"F2.wireOp",EDGE,"E26.1.0.708"),sQuery(id+"F2.wireOp",EDGE,"E26.1.0.709"),sQuery(id+"F2.wireOp",EDGE,"E26.1.0.712"),sQuery(id+"F2.wireOp",EDGE,"E26.1.0.713"),sQuery(id+"F2.wireOp",EDGE,"E26.1.0.715"),sQuery(id+"F2.wireOp",EDGE,"E26.1.0.720")])],"isStart":true})]});
            var sketch = newSketch(context, id + "F4", { "sketchPlane" : qUnion([Q0])});
            skCircle(sketch, "E27", {"center": v(10.8, 10.46) * mm, "radius": 0.4 * mm});
            skCircle(sketch, "E28", {"center": v(10.8, 11.73) * mm, "radius": 0.4 * mm});
            skCircle(sketch, "E29", {"center": v(10.8, 13) * mm, "radius": 0.4 * mm});
            skCircle(sketch, "E30.0.1.0", {"center": v(10.8, 15.8) * mm, "radius": 0.4 * mm});
            skCircle(sketch, "E30.0.1.1", {"center": v(10.8, 17.07) * mm, "radius": 0.4 * mm});
            skCircle(sketch, "E30.0.1.2", {"center": v(10.8, 18.34) * mm, "radius": 0.4 * mm});
            skCircle(sketch, "E30.0.2.0", {"center": v(10.8, 21.15) * mm, "radius": 0.4 * mm});
            skCircle(sketch, "E30.0.2.1", {"center": v(10.8, 22.42) * mm, "radius": 0.4 * mm});
            skCircle(sketch, "E30.0.2.2", {"center": v(10.8, 23.7) * mm, "radius": 0.4 * mm});
            skLineSegment(sketch, "E30.direction1", {"start": v(10.8, 10.46) * mm, "end": v(35.8, 10.46) * mm, "construction": true});
            skLineSegment(sketch, "E30.direction2", {"start": v(10.8, 10.46) * mm, "end": v(10.8, 15.8) * mm, "construction": true});
            skLineSegment(sketch, "E31.0.1.0", {"start": v(10.8, 27.37) * mm, "end": v(10.8, 32.71) * mm, "construction": true});
            skCircle(sketch, "E31.0.1.1", {"center": v(10.8, 35.25) * mm, "radius": 0.4 * mm});
            skCircle(sketch, "E31.0.1.2", {"center": v(10.8, 38.06) * mm, "radius": 0.4 * mm});
            skCircle(sketch, "E31.0.1.3", {"center": v(10.8, 39.33) * mm, "radius": 0.4 * mm});
            skCircle(sketch, "E31.0.1.4", {"center": v(10.8, 40.6) * mm, "radius": 0.4 * mm});
            skCircle(sketch, "E31.0.1.5", {"center": v(10.8, 29.9) * mm, "radius": 0.4 * mm});
            skCircle(sketch, "E31.0.1.6", {"center": v(10.8, 33.98) * mm, "radius": 0.4 * mm});
            skCircle(sketch, "E31.0.1.7", {"center": v(10.8, 28.64) * mm, "radius": 0.4 * mm});
            skCircle(sketch, "E31.0.1.8", {"center": v(10.8, 32.71) * mm, "radius": 0.4 * mm});
            skCircle(sketch, "E31.0.1.9", {"center": v(10.8, 27.37) * mm, "radius": 0.4 * mm});
            skLineSegment(sketch, "E31.0.2.0", {"start": v(10.8, 44.28) * mm, "end": v(10.8, 49.62) * mm, "construction": true});
            skCircle(sketch, "E31.0.2.1", {"center": v(10.8, 52.16) * mm, "radius": 0.4 * mm});
            skCircle(sketch, "E31.0.2.2", {"center": v(10.8, 54.97) * mm, "radius": 0.4 * mm});
            skCircle(sketch, "E31.0.2.3", {"center": v(10.8, 56.24) * mm, "radius": 0.4 * mm});
            skCircle(sketch, "E31.0.2.4", {"center": v(10.8, 57.5) * mm, "radius": 0.4 * mm});
            skCircle(sketch, "E31.0.2.5", {"center": v(10.8, 46.82) * mm, "radius": 0.4 * mm});
            skCircle(sketch, "E31.0.2.6", {"center": v(10.8, 50.9) * mm, "radius": 0.4 * mm});
            skCircle(sketch, "E31.0.2.7", {"center": v(10.8, 45.55) * mm, "radius": 0.4 * mm});
            skCircle(sketch, "E31.0.2.8", {"center": v(10.8, 49.62) * mm, "radius": 0.4 * mm});
            skCircle(sketch, "E31.0.2.9", {"center": v(10.8, 44.28) * mm, "radius": 0.4 * mm});
            skLineSegment(sketch, "E31.0.3.0", {"start": v(10.8, 61.19) * mm, "end": v(10.8, 66.53) * mm, "construction": true});
            skCircle(sketch, "E31.0.3.1", {"center": v(10.8, 69.07) * mm, "radius": 0.4 * mm});
            skCircle(sketch, "E31.0.3.2", {"center": v(10.8, 71.88) * mm, "radius": 0.4 * mm});
            skCircle(sketch, "E31.0.3.3", {"center": v(10.8, 73.15) * mm, "radius": 0.4 * mm});
            skCircle(sketch, "E31.0.3.4", {"center": v(10.8, 74.42) * mm, "radius": 0.4 * mm});
            skCircle(sketch, "E31.0.3.5", {"center": v(10.8, 63.73) * mm, "radius": 0.4 * mm});
            skCircle(sketch, "E31.0.3.6", {"center": v(10.8, 67.8) * mm, "radius": 0.4 * mm});
            skCircle(sketch, "E31.0.3.7", {"center": v(10.8, 62.46) * mm, "radius": 0.4 * mm});
            skCircle(sketch, "E31.0.3.8", {"center": v(10.8, 66.53) * mm, "radius": 0.4 * mm});
            skCircle(sketch, "E31.0.3.9", {"center": v(10.8, 61.19) * mm, "radius": 0.4 * mm});
            skLineSegment(sketch, "E31.0.4.0", {"start": v(10.8, 78.1) * mm, "end": v(10.8, 83.44) * mm, "construction": true});
            skCircle(sketch, "E31.0.4.1", {"center": v(10.8, 85.98) * mm, "radius": 0.4 * mm});
            skCircle(sketch, "E31.0.4.2", {"center": v(10.8, 88.79) * mm, "radius": 0.4 * mm});
            skCircle(sketch, "E31.0.4.3", {"center": v(10.8, 90.06) * mm, "radius": 0.4 * mm});
            skCircle(sketch, "E31.0.4.4", {"center": v(10.8, 91.33) * mm, "radius": 0.4 * mm});
            skCircle(sketch, "E31.0.4.5", {"center": v(10.8, 80.64) * mm, "radius": 0.4 * mm});
            skCircle(sketch, "E31.0.4.6", {"center": v(10.8, 84.71) * mm, "radius": 0.4 * mm});
            skCircle(sketch, "E31.0.4.7", {"center": v(10.8, 79.37) * mm, "radius": 0.4 * mm});
            skCircle(sketch, "E31.0.4.8", {"center": v(10.8, 83.44) * mm, "radius": 0.4 * mm});
            skCircle(sketch, "E31.0.4.9", {"center": v(10.8, 78.1) * mm, "radius": 0.4 * mm});
            skLineSegment(sketch, "E31.1.0.0", {"start": v(21.06, 10.46) * mm, "end": v(21.06, 15.8) * mm, "construction": true});
            skCircle(sketch, "E31.1.0.1", {"center": v(21.06, 18.34) * mm, "radius": 0.4 * mm});
            skCircle(sketch, "E31.1.0.2", {"center": v(21.06, 21.15) * mm, "radius": 0.4 * mm});
            skCircle(sketch, "E31.1.0.3", {"center": v(21.06, 22.42) * mm, "radius": 0.4 * mm});
            skCircle(sketch, "E31.1.0.4", {"center": v(21.06, 23.7) * mm, "radius": 0.4 * mm});
            skCircle(sketch, "E31.1.0.5", {"center": v(21.06, 13) * mm, "radius": 0.4 * mm});
            skCircle(sketch, "E31.1.0.6", {"center": v(21.06, 17.07) * mm, "radius": 0.4 * mm});
            skCircle(sketch, "E31.1.0.7", {"center": v(21.06, 11.73) * mm, "radius": 0.4 * mm});
            skCircle(sketch, "E31.1.0.8", {"center": v(21.06, 15.8) * mm, "radius": 0.4 * mm});
            skCircle(sketch, "E31.1.0.9", {"center": v(21.06, 10.46) * mm, "radius": 0.4 * mm});
            skLineSegment(sketch, "E31.1.1.0", {"start": v(21.06, 27.37) * mm, "end": v(21.06, 32.71) * mm, "construction": true});
            skCircle(sketch, "E31.1.1.1", {"center": v(21.06, 35.25) * mm, "radius": 0.4 * mm});
            skCircle(sketch, "E31.1.1.2", {"center": v(21.06, 38.06) * mm, "radius": 0.4 * mm});
            skCircle(sketch, "E31.1.1.3", {"center": v(21.06, 39.33) * mm, "radius": 0.4 * mm});
            skCircle(sketch, "E31.1.1.4", {"center": v(21.06, 40.6) * mm, "radius": 0.4 * mm});
            skCircle(sketch, "E31.1.1.5", {"center": v(21.06, 29.9) * mm, "radius": 0.4 * mm});
            skCircle(sketch, "E31.1.1.6", {"center": v(21.06, 33.98) * mm, "radius": 0.4 * mm});
            skCircle(sketch, "E31.1.1.7", {"center": v(21.06, 28.64) * mm, "radius": 0.4 * mm});
            skCircle(sketch, "E31.1.1.8", {"center": v(21.06, 32.71) * mm, "radius": 0.4 * mm});
            skCircle(sketch, "E31.1.1.9", {"center": v(21.06, 27.37) * mm, "radius": 0.4 * mm});
            skLineSegment(sketch, "E31.1.2.0", {"start": v(21.06, 44.28) * mm, "end": v(21.06, 49.62) * mm, "construction": true});
            skCircle(sketch, "E31.1.2.1", {"center": v(21.06, 52.16) * mm, "radius": 0.4 * mm});
            skCircle(sketch, "E31.1.2.2", {"center": v(21.06, 54.97) * mm, "radius": 0.4 * mm});
            skCircle(sketch, "E31.1.2.3", {"center": v(21.06, 56.24) * mm, "radius": 0.4 * mm});
            skCircle(sketch, "E31.1.2.4", {"center": v(21.06, 57.5) * mm, "radius": 0.4 * mm});
            skCircle(sketch, "E31.1.2.5", {"center": v(21.06, 46.82) * mm, "radius": 0.4 * mm});
            skCircle(sketch, "E31.1.2.6", {"center": v(21.06, 50.9) * mm, "radius": 0.4 * mm});
            skCircle(sketch, "E31.1.2.7", {"center": v(21.06, 45.55) * mm, "radius": 0.4 * mm});
            skCircle(sketch, "E31.1.2.8", {"center": v(21.06, 49.62) * mm, "radius": 0.4 * mm});
            skCircle(sketch, "E31.1.2.9", {"center": v(21.06, 44.28) * mm, "radius": 0.4 * mm});
            skLineSegment(sketch, "E31.1.3.0", {"start": v(21.06, 61.19) * mm, "end": v(21.06, 66.53) * mm, "construction": true});
            skCircle(sketch, "E31.1.3.1", {"center": v(21.06, 69.07) * mm, "radius": 0.4 * mm});
            skCircle(sketch, "E31.1.3.2", {"center": v(21.06, 71.88) * mm, "radius": 0.4 * mm});
            skCircle(sketch, "E31.1.3.3", {"center": v(21.06, 73.15) * mm, "radius": 0.4 * mm});
            skCircle(sketch, "E31.1.3.4", {"center": v(21.06, 74.42) * mm, "radius": 0.4 * mm});
            skCircle(sketch, "E31.1.3.5", {"center": v(21.06, 63.73) * mm, "radius": 0.4 * mm});
            skCircle(sketch, "E31.1.3.6", {"center": v(21.06, 67.8) * mm, "radius": 0.4 * mm});
            skCircle(sketch, "E31.1.3.7", {"center": v(21.06, 62.46) * mm, "radius": 0.4 * mm});
            skCircle(sketch, "E31.1.3.8", {"center": v(21.06, 66.53) * mm, "radius": 0.4 * mm});
            skCircle(sketch, "E31.1.3.9", {"center": v(21.06, 61.19) * mm, "radius": 0.4 * mm});
            skLineSegment(sketch, "E31.1.4.0", {"start": v(21.06, 78.1) * mm, "end": v(21.06, 83.44) * mm, "construction": true});
            skCircle(sketch, "E31.1.4.1", {"center": v(21.06, 85.98) * mm, "radius": 0.4 * mm});
            skCircle(sketch, "E31.1.4.2", {"center": v(21.06, 88.79) * mm, "radius": 0.4 * mm});
            skCircle(sketch, "E31.1.4.3", {"center": v(21.06, 90.06) * mm, "radius": 0.4 * mm});
            skCircle(sketch, "E31.1.4.4", {"center": v(21.06, 91.33) * mm, "radius": 0.4 * mm});
            skCircle(sketch, "E31.1.4.5", {"center": v(21.06, 80.64) * mm, "radius": 0.4 * mm});
            skCircle(sketch, "E31.1.4.6", {"center": v(21.06, 84.71) * mm, "radius": 0.4 * mm});
            skCircle(sketch, "E31.1.4.7", {"center": v(21.06, 79.37) * mm, "radius": 0.4 * mm});
            skCircle(sketch, "E31.1.4.8", {"center": v(21.06, 83.44) * mm, "radius": 0.4 * mm});
            skCircle(sketch, "E31.1.4.9", {"center": v(21.06, 78.1) * mm, "radius": 0.4 * mm});
            skLineSegment(sketch, "E31.2.0.0", {"start": v(31.32, 10.46) * mm, "end": v(31.32, 15.8) * mm, "construction": true});
            skCircle(sketch, "E31.2.0.1", {"center": v(31.32, 18.34) * mm, "radius": 0.4 * mm});
            skCircle(sketch, "E31.2.0.2", {"center": v(31.32, 21.15) * mm, "radius": 0.4 * mm});
            skCircle(sketch, "E31.2.0.3", {"center": v(31.32, 22.42) * mm, "radius": 0.4 * mm});
            skCircle(sketch, "E31.2.0.4", {"center": v(31.32, 23.7) * mm, "radius": 0.4 * mm});
            skCircle(sketch, "E31.2.0.5", {"center": v(31.32, 13) * mm, "radius": 0.4 * mm});
            skCircle(sketch, "E31.2.0.6", {"center": v(31.32, 17.07) * mm, "radius": 0.4 * mm});
            skCircle(sketch, "E31.2.0.7", {"center": v(31.32, 11.73) * mm, "radius": 0.4 * mm});
            skCircle(sketch, "E31.2.0.8", {"center": v(31.32, 15.8) * mm, "radius": 0.4 * mm});
            skCircle(sketch, "E31.2.0.9", {"center": v(31.32, 10.46) * mm, "radius": 0.4 * mm});
            skLineSegment(sketch, "E31.2.1.0", {"start": v(31.32, 27.37) * mm, "end": v(31.32, 32.71) * mm, "construction": true});
            skCircle(sketch, "E31.2.1.1", {"center": v(31.32, 35.25) * mm, "radius": 0.4 * mm});
            skCircle(sketch, "E31.2.1.2", {"center": v(31.32, 38.06) * mm, "radius": 0.4 * mm});
            skCircle(sketch, "E31.2.1.3", {"center": v(31.32, 39.33) * mm, "radius": 0.4 * mm});
            skCircle(sketch, "E31.2.1.4", {"center": v(31.32, 40.6) * mm, "radius": 0.4 * mm});
            skCircle(sketch, "E31.2.1.5", {"center": v(31.32, 29.9) * mm, "radius": 0.4 * mm});
            skCircle(sketch, "E31.2.1.6", {"center": v(31.32, 33.98) * mm, "radius": 0.4 * mm});
            skCircle(sketch, "E31.2.1.7", {"center": v(31.32, 28.64) * mm, "radius": 0.4 * mm});
            skCircle(sketch, "E31.2.1.8", {"center": v(31.32, 32.71) * mm, "radius": 0.4 * mm});
            skCircle(sketch, "E31.2.1.9", {"center": v(31.32, 27.37) * mm, "radius": 0.4 * mm});
            skLineSegment(sketch, "E31.2.2.0", {"start": v(31.32, 44.28) * mm, "end": v(31.32, 49.62) * mm, "construction": true});
            skCircle(sketch, "E31.2.2.1", {"center": v(31.32, 52.16) * mm, "radius": 0.4 * mm});
            skCircle(sketch, "E31.2.2.2", {"center": v(31.32, 54.97) * mm, "radius": 0.4 * mm});
            skCircle(sketch, "E31.2.2.3", {"center": v(31.32, 56.24) * mm, "radius": 0.4 * mm});
            skCircle(sketch, "E31.2.2.4", {"center": v(31.32, 57.5) * mm, "radius": 0.4 * mm});
            skCircle(sketch, "E31.2.2.5", {"center": v(31.32, 46.82) * mm, "radius": 0.4 * mm});
            skCircle(sketch, "E31.2.2.6", {"center": v(31.32, 50.9) * mm, "radius": 0.4 * mm});
            skCircle(sketch, "E31.2.2.7", {"center": v(31.32, 45.55) * mm, "radius": 0.4 * mm});
            skCircle(sketch, "E31.2.2.8", {"center": v(31.32, 49.62) * mm, "radius": 0.4 * mm});
            skCircle(sketch, "E31.2.2.9", {"center": v(31.32, 44.28) * mm, "radius": 0.4 * mm});
            skLineSegment(sketch, "E31.2.3.0", {"start": v(31.32, 61.19) * mm, "end": v(31.32, 66.53) * mm, "construction": true});
            skCircle(sketch, "E31.2.3.1", {"center": v(31.32, 69.07) * mm, "radius": 0.4 * mm});
            skCircle(sketch, "E31.2.3.2", {"center": v(31.32, 71.88) * mm, "radius": 0.4 * mm});
            skCircle(sketch, "E31.2.3.3", {"center": v(31.32, 73.15) * mm, "radius": 0.4 * mm});
            skCircle(sketch, "E31.2.3.4", {"center": v(31.32, 74.42) * mm, "radius": 0.4 * mm});
            skCircle(sketch, "E31.2.3.5", {"center": v(31.32, 63.73) * mm, "radius": 0.4 * mm});
            skCircle(sketch, "E31.2.3.6", {"center": v(31.32, 67.8) * mm, "radius": 0.4 * mm});
            skCircle(sketch, "E31.2.3.7", {"center": v(31.32, 62.46) * mm, "radius": 0.4 * mm});
            skCircle(sketch, "E31.2.3.8", {"center": v(31.32, 66.53) * mm, "radius": 0.4 * mm});
            skCircle(sketch, "E31.2.3.9", {"center": v(31.32, 61.19) * mm, "radius": 0.4 * mm});
            skLineSegment(sketch, "E31.2.4.0", {"start": v(31.32, 78.1) * mm, "end": v(31.32, 83.44) * mm, "construction": true});
            skCircle(sketch, "E31.2.4.1", {"center": v(31.32, 85.98) * mm, "radius": 0.4 * mm});
            skCircle(sketch, "E31.2.4.2", {"center": v(31.32, 88.79) * mm, "radius": 0.4 * mm});
            skCircle(sketch, "E31.2.4.3", {"center": v(31.32, 90.06) * mm, "radius": 0.4 * mm});
            skCircle(sketch, "E31.2.4.4", {"center": v(31.32, 91.33) * mm, "radius": 0.4 * mm});
            skCircle(sketch, "E31.2.4.5", {"center": v(31.32, 80.64) * mm, "radius": 0.4 * mm});
            skCircle(sketch, "E31.2.4.6", {"center": v(31.32, 84.71) * mm, "radius": 0.4 * mm});
            skCircle(sketch, "E31.2.4.7", {"center": v(31.32, 79.37) * mm, "radius": 0.4 * mm});
            skCircle(sketch, "E31.2.4.8", {"center": v(31.32, 83.44) * mm, "radius": 0.4 * mm});
            skCircle(sketch, "E31.2.4.9", {"center": v(31.32, 78.1) * mm, "radius": 0.4 * mm});
            skLineSegment(sketch, "E31.3.0.0", {"start": v(41.57, 10.46) * mm, "end": v(41.57, 15.8) * mm, "construction": true});
            skCircle(sketch, "E31.3.0.1", {"center": v(41.57, 18.34) * mm, "radius": 0.4 * mm});
            skCircle(sketch, "E31.3.0.2", {"center": v(41.57, 21.15) * mm, "radius": 0.4 * mm});
            skCircle(sketch, "E31.3.0.3", {"center": v(41.57, 22.42) * mm, "radius": 0.4 * mm});
            skCircle(sketch, "E31.3.0.4", {"center": v(41.57, 23.7) * mm, "radius": 0.4 * mm});
            skCircle(sketch, "E31.3.0.5", {"center": v(41.57, 13) * mm, "radius": 0.4 * mm});
            skCircle(sketch, "E31.3.0.6", {"center": v(41.57, 17.07) * mm, "radius": 0.4 * mm});
            skCircle(sketch, "E31.3.0.7", {"center": v(41.57, 11.73) * mm, "radius": 0.4 * mm});
            skCircle(sketch, "E31.3.0.8", {"center": v(41.57, 15.8) * mm, "radius": 0.4 * mm});
            skCircle(sketch, "E31.3.0.9", {"center": v(41.57, 10.46) * mm, "radius": 0.4 * mm});
            skLineSegment(sketch, "E31.3.1.0", {"start": v(41.57, 27.37) * mm, "end": v(41.57, 32.71) * mm, "construction": true});
            skCircle(sketch, "E31.3.1.1", {"center": v(41.57, 35.25) * mm, "radius": 0.4 * mm});
            skCircle(sketch, "E31.3.1.2", {"center": v(41.57, 38.06) * mm, "radius": 0.4 * mm});
            skCircle(sketch, "E31.3.1.3", {"center": v(41.57, 39.33) * mm, "radius": 0.4 * mm});
            skCircle(sketch, "E31.3.1.4", {"center": v(41.57, 40.6) * mm, "radius": 0.4 * mm});
            skCircle(sketch, "E31.3.1.5", {"center": v(41.57, 29.9) * mm, "radius": 0.4 * mm});
            skCircle(sketch, "E31.3.1.6", {"center": v(41.57, 33.98) * mm, "radius": 0.4 * mm});
            skCircle(sketch, "E31.3.1.7", {"center": v(41.57, 28.64) * mm, "radius": 0.4 * mm});
            skCircle(sketch, "E31.3.1.8", {"center": v(41.57, 32.71) * mm, "radius": 0.4 * mm});
            skCircle(sketch, "E31.3.1.9", {"center": v(41.57, 27.37) * mm, "radius": 0.4 * mm});
            skLineSegment(sketch, "E31.3.2.0", {"start": v(41.57, 44.28) * mm, "end": v(41.57, 49.62) * mm, "construction": true});
            skCircle(sketch, "E31.3.2.1", {"center": v(41.57, 52.16) * mm, "radius": 0.4 * mm});
            skCircle(sketch, "E31.3.2.2", {"center": v(41.57, 54.97) * mm, "radius": 0.4 * mm});
            skCircle(sketch, "E31.3.2.3", {"center": v(41.57, 56.24) * mm, "radius": 0.4 * mm});
            skCircle(sketch, "E31.3.2.4", {"center": v(41.57, 57.5) * mm, "radius": 0.4 * mm});
            skCircle(sketch, "E31.3.2.5", {"center": v(41.57, 46.82) * mm, "radius": 0.4 * mm});
            skCircle(sketch, "E31.3.2.6", {"center": v(41.57, 50.9) * mm, "radius": 0.4 * mm});
            skCircle(sketch, "E31.3.2.7", {"center": v(41.57, 45.55) * mm, "radius": 0.4 * mm});
            skCircle(sketch, "E31.3.2.8", {"center": v(41.57, 49.62) * mm, "radius": 0.4 * mm});
            skCircle(sketch, "E31.3.2.9", {"center": v(41.57, 44.28) * mm, "radius": 0.4 * mm});
            skLineSegment(sketch, "E31.3.3.0", {"start": v(41.57, 61.19) * mm, "end": v(41.57, 66.53) * mm, "construction": true});
            skCircle(sketch, "E31.3.3.1", {"center": v(41.57, 69.07) * mm, "radius": 0.4 * mm});
            skCircle(sketch, "E31.3.3.2", {"center": v(41.57, 71.88) * mm, "radius": 0.4 * mm});
            skCircle(sketch, "E31.3.3.3", {"center": v(41.57, 73.15) * mm, "radius": 0.4 * mm});
            skCircle(sketch, "E31.3.3.4", {"center": v(41.57, 74.42) * mm, "radius": 0.4 * mm});
            skCircle(sketch, "E31.3.3.5", {"center": v(41.57, 63.73) * mm, "radius": 0.4 * mm});
            skCircle(sketch, "E31.3.3.6", {"center": v(41.57, 67.8) * mm, "radius": 0.4 * mm});
            skCircle(sketch, "E31.3.3.7", {"center": v(41.57, 62.46) * mm, "radius": 0.4 * mm});
            skCircle(sketch, "E31.3.3.8", {"center": v(41.57, 66.53) * mm, "radius": 0.4 * mm});
            skCircle(sketch, "E31.3.3.9", {"center": v(41.57, 61.19) * mm, "radius": 0.4 * mm});
            skLineSegment(sketch, "E31.3.4.0", {"start": v(41.57, 78.1) * mm, "end": v(41.57, 83.44) * mm, "construction": true});
            skCircle(sketch, "E31.3.4.1", {"center": v(41.57, 85.98) * mm, "radius": 0.4 * mm});
            skCircle(sketch, "E31.3.4.2", {"center": v(41.57, 88.79) * mm, "radius": 0.4 * mm});
            skCircle(sketch, "E31.3.4.3", {"center": v(41.57, 90.06) * mm, "radius": 0.4 * mm});
            skCircle(sketch, "E31.3.4.4", {"center": v(41.57, 91.33) * mm, "radius": 0.4 * mm});
            skCircle(sketch, "E31.3.4.5", {"center": v(41.57, 80.64) * mm, "radius": 0.4 * mm});
            skCircle(sketch, "E31.3.4.6", {"center": v(41.57, 84.71) * mm, "radius": 0.4 * mm});
            skCircle(sketch, "E31.3.4.7", {"center": v(41.57, 79.37) * mm, "radius": 0.4 * mm});
            skCircle(sketch, "E31.3.4.8", {"center": v(41.57, 83.44) * mm, "radius": 0.4 * mm});
            skCircle(sketch, "E31.3.4.9", {"center": v(41.57, 78.1) * mm, "radius": 0.4 * mm});
            skLineSegment(sketch, "E31.4.0.0", {"start": v(51.82, 10.46) * mm, "end": v(51.82, 15.8) * mm, "construction": true});
            skCircle(sketch, "E31.4.0.1", {"center": v(51.82, 18.34) * mm, "radius": 0.4 * mm});
            skCircle(sketch, "E31.4.0.2", {"center": v(51.82, 21.15) * mm, "radius": 0.4 * mm});
            skCircle(sketch, "E31.4.0.3", {"center": v(51.82, 22.42) * mm, "radius": 0.4 * mm});
            skCircle(sketch, "E31.4.0.4", {"center": v(51.82, 23.7) * mm, "radius": 0.4 * mm});
            skCircle(sketch, "E31.4.0.5", {"center": v(51.82, 13) * mm, "radius": 0.4 * mm});
            skCircle(sketch, "E31.4.0.6", {"center": v(51.82, 17.07) * mm, "radius": 0.4 * mm});
            skCircle(sketch, "E31.4.0.7", {"center": v(51.82, 11.73) * mm, "radius": 0.4 * mm});
            skCircle(sketch, "E31.4.0.8", {"center": v(51.82, 15.8) * mm, "radius": 0.4 * mm});
            skCircle(sketch, "E31.4.0.9", {"center": v(51.82, 10.46) * mm, "radius": 0.4 * mm});
            skLineSegment(sketch, "E31.4.1.0", {"start": v(51.82, 27.37) * mm, "end": v(51.82, 32.71) * mm, "construction": true});
            skCircle(sketch, "E31.4.1.1", {"center": v(51.82, 35.25) * mm, "radius": 0.4 * mm});
            skCircle(sketch, "E31.4.1.2", {"center": v(51.82, 38.06) * mm, "radius": 0.4 * mm});
            skCircle(sketch, "E31.4.1.3", {"center": v(51.82, 39.33) * mm, "radius": 0.4 * mm});
            skCircle(sketch, "E31.4.1.4", {"center": v(51.82, 40.6) * mm, "radius": 0.4 * mm});
            skCircle(sketch, "E31.4.1.5", {"center": v(51.82, 29.9) * mm, "radius": 0.4 * mm});
            skCircle(sketch, "E31.4.1.6", {"center": v(51.82, 33.98) * mm, "radius": 0.4 * mm});
            skCircle(sketch, "E31.4.1.7", {"center": v(51.82, 28.64) * mm, "radius": 0.4 * mm});
            skCircle(sketch, "E31.4.1.8", {"center": v(51.82, 32.71) * mm, "radius": 0.4 * mm});
            skCircle(sketch, "E31.4.1.9", {"center": v(51.82, 27.37) * mm, "radius": 0.4 * mm});
            skLineSegment(sketch, "E31.4.2.0", {"start": v(51.82, 44.28) * mm, "end": v(51.82, 49.62) * mm, "construction": true});
            skCircle(sketch, "E31.4.2.1", {"center": v(51.82, 52.16) * mm, "radius": 0.4 * mm});
            skCircle(sketch, "E31.4.2.2", {"center": v(51.82, 54.97) * mm, "radius": 0.4 * mm});
            skCircle(sketch, "E31.4.2.3", {"center": v(51.82, 56.24) * mm, "radius": 0.4 * mm});
            skCircle(sketch, "E31.4.2.4", {"center": v(51.82, 57.5) * mm, "radius": 0.4 * mm});
            skCircle(sketch, "E31.4.2.5", {"center": v(51.82, 46.82) * mm, "radius": 0.4 * mm});
            skCircle(sketch, "E31.4.2.6", {"center": v(51.82, 50.9) * mm, "radius": 0.4 * mm});
            skCircle(sketch, "E31.4.2.7", {"center": v(51.82, 45.55) * mm, "radius": 0.4 * mm});
            skCircle(sketch, "E31.4.2.8", {"center": v(51.82, 49.62) * mm, "radius": 0.4 * mm});
            skCircle(sketch, "E31.4.2.9", {"center": v(51.82, 44.28) * mm, "radius": 0.4 * mm});
            skLineSegment(sketch, "E31.4.3.0", {"start": v(51.82, 61.19) * mm, "end": v(51.82, 66.53) * mm, "construction": true});
            skCircle(sketch, "E31.4.3.1", {"center": v(51.82, 69.07) * mm, "radius": 0.4 * mm});
            skCircle(sketch, "E31.4.3.2", {"center": v(51.82, 71.88) * mm, "radius": 0.4 * mm});
            skCircle(sketch, "E31.4.3.3", {"center": v(51.82, 73.15) * mm, "radius": 0.4 * mm});
            skCircle(sketch, "E31.4.3.4", {"center": v(51.82, 74.42) * mm, "radius": 0.4 * mm});
            skCircle(sketch, "E31.4.3.5", {"center": v(51.82, 63.73) * mm, "radius": 0.4 * mm});
            skCircle(sketch, "E31.4.3.6", {"center": v(51.82, 67.8) * mm, "radius": 0.4 * mm});
            skCircle(sketch, "E31.4.3.7", {"center": v(51.82, 62.46) * mm, "radius": 0.4 * mm});
            skCircle(sketch, "E31.4.3.8", {"center": v(51.82, 66.53) * mm, "radius": 0.4 * mm});
            skCircle(sketch, "E31.4.3.9", {"center": v(51.82, 61.19) * mm, "radius": 0.4 * mm});
            skLineSegment(sketch, "E31.4.4.0", {"start": v(51.82, 78.1) * mm, "end": v(51.82, 83.44) * mm, "construction": true});
            skCircle(sketch, "E31.4.4.1", {"center": v(51.82, 85.98) * mm, "radius": 0.4 * mm});
            skCircle(sketch, "E31.4.4.2", {"center": v(51.82, 88.79) * mm, "radius": 0.4 * mm});
            skCircle(sketch, "E31.4.4.3", {"center": v(51.82, 90.06) * mm, "radius": 0.4 * mm});
            skCircle(sketch, "E31.4.4.4", {"center": v(51.82, 91.33) * mm, "radius": 0.4 * mm});
            skCircle(sketch, "E31.4.4.5", {"center": v(51.82, 80.64) * mm, "radius": 0.4 * mm});
            skCircle(sketch, "E31.4.4.6", {"center": v(51.82, 84.71) * mm, "radius": 0.4 * mm});
            skCircle(sketch, "E31.4.4.7", {"center": v(51.82, 79.37) * mm, "radius": 0.4 * mm});
            skCircle(sketch, "E31.4.4.8", {"center": v(51.82, 83.44) * mm, "radius": 0.4 * mm});
            skCircle(sketch, "E31.4.4.9", {"center": v(51.82, 78.1) * mm, "radius": 0.4 * mm});
            skLineSegment(sketch, "E31.direction1", {"start": v(10.8, 10.46) * mm, "end": v(21.06, 10.46) * mm, "construction": true});
            skLineSegment(sketch, "E31.direction2", {"start": v(10.8, 10.46) * mm, "end": v(10.8, 27.37) * mm, "construction": true});
            skLineSegment(sketch, "E32.1.0.0", {"start": v(71.7, 10.46) * mm, "end": v(96.7, 10.46) * mm, "construction": true});
            skCircle(sketch, "E32.1.0.1", {"center": v(92.2, 38.06) * mm, "radius": 0.4 * mm});
            skCircle(sketch, "E32.1.0.2", {"center": v(102.46, 54.97) * mm, "radius": 0.4 * mm});
            skCircle(sketch, "E32.1.0.3", {"center": v(71.7, 38.06) * mm, "radius": 0.4 * mm});
            skCircle(sketch, "E32.1.0.4", {"center": v(71.7, 39.33) * mm, "radius": 0.4 * mm});
            skCircle(sketch, "E32.1.0.5", {"center": v(81.95, 74.42) * mm, "radius": 0.4 * mm});
            skCircle(sketch, "E32.1.0.6", {"center": v(92.2, 21.15) * mm, "radius": 0.4 * mm});
            skCircle(sketch, "E32.1.0.7", {"center": v(102.46, 56.24) * mm, "radius": 0.4 * mm});
            skCircle(sketch, "E32.1.0.8", {"center": v(112.71, 91.33) * mm, "radius": 0.4 * mm});
            skCircle(sketch, "E32.1.0.9", {"center": v(92.2, 39.33) * mm, "radius": 0.4 * mm});
            skCircle(sketch, "E32.1.0.10", {"center": v(102.46, 74.42) * mm, "radius": 0.4 * mm});
            skCircle(sketch, "E32.1.0.11", {"center": v(112.71, 21.15) * mm, "radius": 0.4 * mm});
            skCircle(sketch, "E32.1.0.12", {"center": v(71.7, 40.6) * mm, "radius": 0.4 * mm});
            skCircle(sketch, "E32.1.0.13", {"center": v(71.7, 71.88) * mm, "radius": 0.4 * mm});
            skCircle(sketch, "E32.1.0.14", {"center": v(71.7, 88.79) * mm, "radius": 0.4 * mm});
            skCircle(sketch, "E32.1.0.15", {"center": v(71.7, 57.5) * mm, "radius": 0.4 * mm});
            skCircle(sketch, "E32.1.0.16", {"center": v(92.2, 22.42) * mm, "radius": 0.4 * mm});
            skCircle(sketch, "E32.1.0.17", {"center": v(102.46, 88.79) * mm, "radius": 0.4 * mm});
            skCircle(sketch, "E32.1.0.18", {"center": v(102.46, 57.5) * mm, "radius": 0.4 * mm});
            skCircle(sketch, "E32.1.0.19", {"center": v(112.71, 80.64) * mm, "radius": 0.4 * mm});
            skCircle(sketch, "E32.1.0.20", {"center": v(92.2, 71.88) * mm, "radius": 0.4 * mm});
            skCircle(sketch, "E32.1.0.21", {"center": v(112.71, 22.42) * mm, "radius": 0.4 * mm});
            skCircle(sketch, "E32.1.0.22", {"center": v(71.7, 73.15) * mm, "radius": 0.4 * mm});
            skCircle(sketch, "E32.1.0.23", {"center": v(92.2, 54.97) * mm, "radius": 0.4 * mm});
            skCircle(sketch, "E32.1.0.24", {"center": v(92.2, 23.7) * mm, "radius": 0.4 * mm});
            skCircle(sketch, "E32.1.0.25", {"center": v(71.7, 90.06) * mm, "radius": 0.4 * mm});
            skCircle(sketch, "E32.1.0.26", {"center": v(71.7, 21.15) * mm, "radius": 0.4 * mm});
            skCircle(sketch, "E32.1.0.27", {"center": v(92.2, 40.6) * mm, "radius": 0.4 * mm});
            skCircle(sketch, "E32.1.0.28", {"center": v(112.71, 35.25) * mm, "radius": 0.4 * mm});
            skCircle(sketch, "E32.1.0.29", {"center": v(102.46, 90.06) * mm, "radius": 0.4 * mm});
            skCircle(sketch, "E32.1.0.30", {"center": v(112.71, 54.97) * mm, "radius": 0.4 * mm});
            skCircle(sketch, "E32.1.0.31", {"center": v(112.71, 23.7) * mm, "radius": 0.4 * mm});
            skLineSegment(sketch, "E32.1.0.32", {"start": v(71.7, 10.46) * mm, "end": v(81.95, 10.46) * mm, "construction": true});
            skCircle(sketch, "E32.1.0.33", {"center": v(81.95, 21.15) * mm, "radius": 0.4 * mm});
            skCircle(sketch, "E32.1.0.34", {"center": v(71.7, 74.42) * mm, "radius": 0.4 * mm});
            skCircle(sketch, "E32.1.0.35", {"center": v(92.2, 56.24) * mm, "radius": 0.4 * mm});
            skCircle(sketch, "E32.1.0.36", {"center": v(102.46, 91.33) * mm, "radius": 0.4 * mm});
            skCircle(sketch, "E32.1.0.37", {"center": v(71.7, 91.33) * mm, "radius": 0.4 * mm});
            skCircle(sketch, "E32.1.0.38", {"center": v(71.7, 22.42) * mm, "radius": 0.4 * mm});
            skCircle(sketch, "E32.1.0.39", {"center": v(81.95, 38.06) * mm, "radius": 0.4 * mm});
            skCircle(sketch, "E32.1.0.40", {"center": v(102.46, 40.6) * mm, "radius": 0.4 * mm});
            skCircle(sketch, "E32.1.0.41", {"center": v(92.2, 73.15) * mm, "radius": 0.4 * mm});
            skLineSegment(sketch, "E32.1.0.42", {"start": v(71.7, 10.46) * mm, "end": v(71.7, 27.37) * mm, "construction": true});
            skCircle(sketch, "E32.1.0.43", {"center": v(81.95, 22.42) * mm, "radius": 0.4 * mm});
            skCircle(sketch, "E32.1.0.44", {"center": v(71.7, 63.73) * mm, "radius": 0.4 * mm});
            skCircle(sketch, "E32.1.0.45", {"center": v(92.2, 57.5) * mm, "radius": 0.4 * mm});
            skCircle(sketch, "E32.1.0.46", {"center": v(71.7, 23.7) * mm, "radius": 0.4 * mm});
            skCircle(sketch, "E32.1.0.47", {"center": v(81.95, 39.33) * mm, "radius": 0.4 * mm});
            skCircle(sketch, "E32.1.0.48", {"center": v(102.46, 38.06) * mm, "radius": 0.4 * mm});
            skCircle(sketch, "E32.1.0.49", {"center": v(92.2, 91.33) * mm, "radius": 0.4 * mm});
            skCircle(sketch, "E32.1.0.50", {"center": v(92.2, 74.42) * mm, "radius": 0.4 * mm});
            skCircle(sketch, "E32.1.0.51", {"center": v(112.71, 85.98) * mm, "radius": 0.4 * mm});
            skCircle(sketch, "E32.1.0.52", {"center": v(112.71, 73.15) * mm, "radius": 0.4 * mm});
            skCircle(sketch, "E32.1.0.53", {"center": v(81.95, 23.7) * mm, "radius": 0.4 * mm});
            skCircle(sketch, "E32.1.0.54", {"center": v(112.71, 71.88) * mm, "radius": 0.4 * mm});
            skCircle(sketch, "E32.1.0.55", {"center": v(71.7, 52.16) * mm, "radius": 0.4 * mm});
            skCircle(sketch, "E32.1.0.56", {"center": v(81.95, 40.6) * mm, "radius": 0.4 * mm});
            skCircle(sketch, "E32.1.0.57", {"center": v(102.46, 69.07) * mm, "radius": 0.4 * mm});
            skCircle(sketch, "E32.1.0.58", {"center": v(102.46, 39.33) * mm, "radius": 0.4 * mm});
            skCircle(sketch, "E32.1.0.59", {"center": v(112.71, 74.42) * mm, "radius": 0.4 * mm});
            skCircle(sketch, "E32.1.0.60", {"center": v(81.95, 91.33) * mm, "radius": 0.4 * mm});
            skCircle(sketch, "E32.1.0.61", {"center": v(71.7, 56.24) * mm, "radius": 0.4 * mm});
            skCircle(sketch, "E32.1.0.62", {"center": v(81.95, 29.9) * mm, "radius": 0.4 * mm});
            skCircle(sketch, "E32.1.0.63", {"center": v(102.46, 23.7) * mm, "radius": 0.4 * mm});
            skCircle(sketch, "E32.1.0.64", {"center": v(81.95, 50.9) * mm, "radius": 0.4 * mm});
            skCircle(sketch, "E32.1.0.65", {"center": v(102.46, 73.15) * mm, "radius": 0.4 * mm});
            skCircle(sketch, "E32.1.0.66", {"center": v(102.46, 29.9) * mm, "radius": 0.4 * mm});
            skCircle(sketch, "E32.1.0.67", {"center": v(81.95, 73.15) * mm, "radius": 0.4 * mm});
            skCircle(sketch, "E32.1.0.68", {"center": v(102.46, 61.19) * mm, "radius": 0.4 * mm});
            skCircle(sketch, "E32.1.0.69", {"center": v(81.95, 15.8) * mm, "radius": 0.4 * mm});
            skLineSegment(sketch, "E32.1.0.70", {"start": v(102.46, 10.46) * mm, "end": v(102.46, 15.8) * mm, "construction": true});
            skCircle(sketch, "E32.1.0.71", {"center": v(92.2, 18.34) * mm, "radius": 0.4 * mm});
            skLineSegment(sketch, "E32.1.0.72", {"start": v(112.71, 27.37) * mm, "end": v(112.71, 32.71) * mm, "construction": true});
            skCircle(sketch, "E32.1.0.73", {"center": v(112.71, 11.73) * mm, "radius": 0.4 * mm});
            skCircle(sketch, "E32.1.0.74", {"center": v(71.7, 85.98) * mm, "radius": 0.4 * mm});
            skCircle(sketch, "E32.1.0.75", {"center": v(92.2, 32.71) * mm, "radius": 0.4 * mm});
            skCircle(sketch, "E32.1.0.76", {"center": v(71.7, 79.37) * mm, "radius": 0.4 * mm});
            skCircle(sketch, "E32.1.0.77", {"center": v(71.7, 44.28) * mm, "radius": 0.4 * mm});
            skCircle(sketch, "E32.1.0.78", {"center": v(112.71, 46.82) * mm, "radius": 0.4 * mm});
            skCircle(sketch, "E32.1.0.79", {"center": v(92.2, 67.8) * mm, "radius": 0.4 * mm});
            skCircle(sketch, "E32.1.0.80", {"center": v(112.71, 90.06) * mm, "radius": 0.4 * mm});
            skCircle(sketch, "E32.1.0.81", {"center": v(92.2, 79.37) * mm, "radius": 0.4 * mm});
            skCircle(sketch, "E32.1.0.82", {"center": v(92.2, 44.28) * mm, "radius": 0.4 * mm});
            skCircle(sketch, "E32.1.0.83", {"center": v(112.71, 67.8) * mm, "radius": 0.4 * mm});
            skCircle(sketch, "E32.1.0.84", {"center": v(112.71, 18.34) * mm, "radius": 0.4 * mm});
            skLineSegment(sketch, "E32.1.0.85", {"start": v(112.71, 44.28) * mm, "end": v(112.71, 49.62) * mm, "construction": true});
            skCircle(sketch, "E32.1.0.86", {"center": v(81.95, 33.98) * mm, "radius": 0.4 * mm});
            skCircle(sketch, "E32.1.0.87", {"center": v(71.7, 83.44) * mm, "radius": 0.4 * mm});
            skCircle(sketch, "E32.1.0.88", {"center": v(71.7, 69.07) * mm, "radius": 0.4 * mm});
            skCircle(sketch, "E32.1.0.89", {"center": v(102.46, 13) * mm, "radius": 0.4 * mm});
            skCircle(sketch, "E32.1.0.90", {"center": v(92.2, 62.46) * mm, "radius": 0.4 * mm});
            skCircle(sketch, "E32.1.0.91", {"center": v(92.2, 27.37) * mm, "radius": 0.4 * mm});
            skCircle(sketch, "E32.1.0.92", {"center": v(112.71, 15.8) * mm, "radius": 0.4 * mm});
            skCircle(sketch, "E32.1.0.93", {"center": v(102.46, 85.98) * mm, "radius": 0.4 * mm});
            skCircle(sketch, "E32.1.0.94", {"center": v(81.95, 80.64) * mm, "radius": 0.4 * mm});
            skCircle(sketch, "E32.1.0.95", {"center": v(81.95, 45.55) * mm, "radius": 0.4 * mm});
            skCircle(sketch, "E32.1.0.96", {"center": v(102.46, 33.98) * mm, "radius": 0.4 * mm});
            skCircle(sketch, "E32.1.0.97", {"center": v(92.2, 83.44) * mm, "radius": 0.4 * mm});
            skCircle(sketch, "E32.1.0.98", {"center": v(92.2, 69.07) * mm, "radius": 0.4 * mm});
            skCircle(sketch, "E32.1.0.99", {"center": v(112.71, 62.46) * mm, "radius": 0.4 * mm});
            skCircle(sketch, "E32.1.0.100", {"center": v(112.71, 27.37) * mm, "radius": 0.4 * mm});
            skLineSegment(sketch, "E32.1.0.101", {"start": v(112.71, 61.19) * mm, "end": v(112.71, 66.53) * mm, "construction": true});
            skCircle(sketch, "E32.1.0.102", {"center": v(81.95, 63.73) * mm, "radius": 0.4 * mm});
            skCircle(sketch, "E32.1.0.103", {"center": v(81.95, 28.64) * mm, "radius": 0.4 * mm});
            skCircle(sketch, "E32.1.0.104", {"center": v(71.7, 78.1) * mm, "radius": 0.4 * mm});
            skCircle(sketch, "E32.1.0.105", {"center": v(71.7, 18.34) * mm, "radius": 0.4 * mm});
            skLineSegment(sketch, "E32.1.0.106", {"start": v(102.46, 27.37) * mm, "end": v(102.46, 32.71) * mm, "construction": true});
            skCircle(sketch, "E32.1.0.107", {"center": v(92.2, 66.53) * mm, "radius": 0.4 * mm});
            skCircle(sketch, "E32.1.0.108", {"center": v(92.2, 52.16) * mm, "radius": 0.4 * mm});
            skCircle(sketch, "E32.1.0.109", {"center": v(112.71, 45.55) * mm, "radius": 0.4 * mm});
            skCircle(sketch, "E32.1.0.110", {"center": v(112.71, 10.46) * mm, "radius": 0.4 * mm});
            skCircle(sketch, "E32.1.0.111", {"center": v(102.46, 63.73) * mm, "radius": 0.4 * mm});
            skCircle(sketch, "E32.1.0.112", {"center": v(102.46, 28.64) * mm, "radius": 0.4 * mm});
            skCircle(sketch, "E32.1.0.113", {"center": v(92.2, 78.1) * mm, "radius": 0.4 * mm});
            skCircle(sketch, "E32.1.0.114", {"center": v(112.71, 66.53) * mm, "radius": 0.4 * mm});
            skCircle(sketch, "E32.1.0.115", {"center": v(112.71, 52.16) * mm, "radius": 0.4 * mm});
            skCircle(sketch, "E32.1.0.116", {"center": v(71.7, 29.9) * mm, "radius": 0.4 * mm});
            skLineSegment(sketch, "E32.1.0.117", {"start": v(112.71, 78.1) * mm, "end": v(112.71, 83.44) * mm, "construction": true});
            skCircle(sketch, "E32.1.0.118", {"center": v(81.95, 67.8) * mm, "radius": 0.4 * mm});
            skCircle(sketch, "E32.1.0.119", {"center": v(81.95, 32.71) * mm, "radius": 0.4 * mm});
            skCircle(sketch, "E32.1.0.120", {"center": v(81.95, 18.34) * mm, "radius": 0.4 * mm});
            skCircle(sketch, "E32.1.0.121", {"center": v(102.46, 11.73) * mm, "radius": 0.4 * mm});
            skCircle(sketch, "E32.1.0.122", {"center": v(92.2, 61.19) * mm, "radius": 0.4 * mm});
            skCircle(sketch, "E32.1.0.123", {"center": v(71.7, 46.82) * mm, "radius": 0.4 * mm});
            skLineSegment(sketch, "E32.1.0.124", {"start": v(102.46, 44.28) * mm, "end": v(102.46, 49.62) * mm, "construction": true});
            skCircle(sketch, "E32.1.0.125", {"center": v(81.95, 84.71) * mm, "radius": 0.4 * mm});
            skCircle(sketch, "E32.1.0.126", {"center": v(81.95, 49.62) * mm, "radius": 0.4 * mm});
            skCircle(sketch, "E32.1.0.127", {"center": v(81.95, 35.25) * mm, "radius": 0.4 * mm});
            skCircle(sketch, "E32.1.0.128", {"center": v(102.46, 46.82) * mm, "radius": 0.4 * mm});
            skCircle(sketch, "E32.1.0.129", {"center": v(112.71, 63.73) * mm, "radius": 0.4 * mm});
            skCircle(sketch, "E32.1.0.130", {"center": v(112.71, 61.19) * mm, "radius": 0.4 * mm});
            skCircle(sketch, "E32.1.0.131", {"center": v(112.71, 28.64) * mm, "radius": 0.4 * mm});
            skCircle(sketch, "E32.1.0.132", {"center": v(102.46, 78.1) * mm, "radius": 0.4 * mm});
            skCircle(sketch, "E32.1.0.133", {"center": v(71.7, 33.98) * mm, "radius": 0.4 * mm});
            skCircle(sketch, "E32.1.0.134", {"center": v(81.95, 62.46) * mm, "radius": 0.4 * mm});
            skCircle(sketch, "E32.1.0.135", {"center": v(81.95, 27.37) * mm, "radius": 0.4 * mm});
            skCircle(sketch, "E32.1.0.136", {"center": v(92.2, 85.98) * mm, "radius": 0.4 * mm});
            skCircle(sketch, "E32.1.0.137", {"center": v(92.2, 13) * mm, "radius": 0.4 * mm});
            skCircle(sketch, "E32.1.0.138", {"center": v(112.71, 44.28) * mm, "radius": 0.4 * mm});
            skCircle(sketch, "E32.1.0.139", {"center": v(112.71, 38.06) * mm, "radius": 0.4 * mm});
            skCircle(sketch, "E32.1.0.140", {"center": v(102.46, 50.9) * mm, "radius": 0.4 * mm});
            skCircle(sketch, "E32.1.0.141", {"center": v(71.7, 61.19) * mm, "radius": 0.4 * mm});
            skCircle(sketch, "E32.1.0.142", {"center": v(71.7, 54.97) * mm, "radius": 0.4 * mm});
            skCircle(sketch, "E32.1.0.143", {"center": v(71.7, 50.9) * mm, "radius": 0.4 * mm});
            skLineSegment(sketch, "E32.1.0.144", {"start": v(102.46, 61.19) * mm, "end": v(102.46, 66.53) * mm, "construction": true});
            skCircle(sketch, "E32.1.0.145", {"center": v(92.2, 35.25) * mm, "radius": 0.4 * mm});
            skCircle(sketch, "E32.1.0.146", {"center": v(92.2, 29.9) * mm, "radius": 0.4 * mm});
            skCircle(sketch, "E32.1.0.147", {"center": v(81.95, 90.06) * mm, "radius": 0.4 * mm});
            skCircle(sketch, "E32.1.0.148", {"center": v(81.95, 79.37) * mm, "radius": 0.4 * mm});
            skCircle(sketch, "E32.1.0.149", {"center": v(81.95, 44.28) * mm, "radius": 0.4 * mm});
            skCircle(sketch, "E32.1.0.150", {"center": v(81.95, 46.82) * mm, "radius": 0.4 * mm});
            skCircle(sketch, "E32.1.0.151", {"center": v(102.46, 67.8) * mm, "radius": 0.4 * mm});
            skCircle(sketch, "E32.1.0.152", {"center": v(102.46, 71.88) * mm, "radius": 0.4 * mm});
            skCircle(sketch, "E32.1.0.153", {"center": v(102.46, 32.71) * mm, "radius": 0.4 * mm});
            skCircle(sketch, "E32.1.0.154", {"center": v(102.46, 18.34) * mm, "radius": 0.4 * mm});
            skCircle(sketch, "E32.1.0.155", {"center": v(92.2, 84.71) * mm, "radius": 0.4 * mm});
            skCircle(sketch, "E32.1.0.156", {"center": v(92.2, 49.62) * mm, "radius": 0.4 * mm});
            skCircle(sketch, "E32.1.0.157", {"center": v(112.71, 79.37) * mm, "radius": 0.4 * mm});
            skLineSegment(sketch, "E32.1.0.158", {"start": v(92.2, 78.1) * mm, "end": v(92.2, 83.44) * mm, "construction": true});
            skCircle(sketch, "E32.1.0.159", {"center": v(81.95, 66.53) * mm, "radius": 0.4 * mm});
            skLineSegment(sketch, "E32.1.0.160", {"start": v(92.2, 44.28) * mm, "end": v(92.2, 49.62) * mm, "construction": true});
            skCircle(sketch, "E32.1.0.161", {"center": v(81.95, 52.16) * mm, "radius": 0.4 * mm});
            skCircle(sketch, "E32.1.0.162", {"center": v(102.46, 10.46) * mm, "radius": 0.4 * mm});
            skCircle(sketch, "E32.1.0.163", {"center": v(92.2, 88.79) * mm, "radius": 0.4 * mm});
            skLineSegment(sketch, "E32.1.0.164", {"start": v(92.2, 61.19) * mm, "end": v(92.2, 66.53) * mm, "construction": true});
            skCircle(sketch, "E32.1.0.165", {"center": v(92.2, 17.07) * mm, "radius": 0.4 * mm});
            skCircle(sketch, "E32.1.0.166", {"center": v(112.71, 69.07) * mm, "radius": 0.4 * mm});
            skCircle(sketch, "E32.1.0.167", {"center": v(112.71, 39.33) * mm, "radius": 0.4 * mm});
            skCircle(sketch, "E32.1.0.168", {"center": v(102.46, 80.64) * mm, "radius": 0.4 * mm});
            skCircle(sketch, "E32.1.0.169", {"center": v(102.46, 45.55) * mm, "radius": 0.4 * mm});
            skLineSegment(sketch, "E32.1.0.170", {"start": v(71.7, 27.37) * mm, "end": v(71.7, 32.71) * mm, "construction": true});
            skLineSegment(sketch, "E32.1.0.171", {"start": v(71.7, 44.28) * mm, "end": v(71.7, 49.62) * mm, "construction": true});
            skCircle(sketch, "E32.1.0.172", {"center": v(71.7, 80.64) * mm, "radius": 0.4 * mm});
            skCircle(sketch, "E32.1.0.173", {"center": v(71.7, 62.46) * mm, "radius": 0.4 * mm});
            skLineSegment(sketch, "E32.1.0.174", {"start": v(71.7, 61.19) * mm, "end": v(71.7, 66.53) * mm, "construction": true});
            skCircle(sketch, "E32.1.0.175", {"center": v(71.7, 45.55) * mm, "radius": 0.4 * mm});
            skLineSegment(sketch, "E32.1.0.176", {"start": v(102.46, 78.1) * mm, "end": v(102.46, 83.44) * mm, "construction": true});
            skCircle(sketch, "E32.1.0.177", {"center": v(92.2, 33.98) * mm, "radius": 0.4 * mm});
            skCircle(sketch, "E32.1.0.178", {"center": v(92.2, 15.8) * mm, "radius": 0.4 * mm});
            skLineSegment(sketch, "E32.1.0.179", {"start": v(71.7, 78.1) * mm, "end": v(71.7, 83.44) * mm, "construction": true});
            skCircle(sketch, "E32.1.0.180", {"center": v(81.95, 83.44) * mm, "radius": 0.4 * mm});
            skCircle(sketch, "E32.1.0.181", {"center": v(81.95, 85.98) * mm, "radius": 0.4 * mm});
            skCircle(sketch, "E32.1.0.182", {"center": v(81.95, 56.24) * mm, "radius": 0.4 * mm});
            skCircle(sketch, "E32.1.0.183", {"center": v(81.95, 69.07) * mm, "radius": 0.4 * mm});
            skCircle(sketch, "E32.1.0.184", {"center": v(81.95, 13) * mm, "radius": 0.4 * mm});
            skCircle(sketch, "E32.1.0.185", {"center": v(102.46, 62.46) * mm, "radius": 0.4 * mm});
            skCircle(sketch, "E32.1.0.186", {"center": v(102.46, 44.28) * mm, "radius": 0.4 * mm});
            skCircle(sketch, "E32.1.0.187", {"center": v(102.46, 27.37) * mm, "radius": 0.4 * mm});
            skCircle(sketch, "E32.1.0.188", {"center": v(102.46, 21.15) * mm, "radius": 0.4 * mm});
            skCircle(sketch, "E32.1.0.189", {"center": v(92.2, 50.9) * mm, "radius": 0.4 * mm});
            skCircle(sketch, "E32.1.0.190", {"center": v(112.71, 29.9) * mm, "radius": 0.4 * mm});
            skLineSegment(sketch, "E32.1.0.191", {"start": v(81.95, 10.46) * mm, "end": v(81.95, 15.8) * mm, "construction": true});
            skCircle(sketch, "E32.1.0.192", {"center": v(112.71, 56.24) * mm, "radius": 0.4 * mm});
            skCircle(sketch, "E32.1.0.193", {"center": v(102.46, 79.37) * mm, "radius": 0.4 * mm});
            skCircle(sketch, "E32.1.0.194", {"center": v(112.71, 13) * mm, "radius": 0.4 * mm});
            skLineSegment(sketch, "E32.1.0.195", {"start": v(81.95, 27.37) * mm, "end": v(81.95, 32.71) * mm, "construction": true});
            skLineSegment(sketch, "E32.1.0.196", {"start": v(81.95, 44.28) * mm, "end": v(81.95, 49.62) * mm, "construction": true});
            skLineSegment(sketch, "E32.1.0.197", {"start": v(81.95, 61.19) * mm, "end": v(81.95, 66.53) * mm, "construction": true});
            skLineSegment(sketch, "E32.1.0.198", {"start": v(81.95, 78.1) * mm, "end": v(81.95, 83.44) * mm, "construction": true});
            skLineSegment(sketch, "E32.1.0.199", {"start": v(92.2, 10.46) * mm, "end": v(92.2, 15.8) * mm, "construction": true});
            skLineSegment(sketch, "E32.1.0.200", {"start": v(92.2, 27.37) * mm, "end": v(92.2, 32.71) * mm, "construction": true});
            skCircle(sketch, "E32.1.0.201", {"center": v(71.7, 32.71) * mm, "radius": 0.4 * mm});
            skCircle(sketch, "E32.1.0.202", {"center": v(81.95, 61.19) * mm, "radius": 0.4 * mm});
            skCircle(sketch, "E32.1.0.203", {"center": v(81.95, 54.97) * mm, "radius": 0.4 * mm});
            skCircle(sketch, "E32.1.0.204", {"center": v(71.7, 67.8) * mm, "radius": 0.4 * mm});
            skCircle(sketch, "E32.1.0.205", {"center": v(102.46, 35.25) * mm, "radius": 0.4 * mm});
            skCircle(sketch, "E32.1.0.206", {"center": v(92.2, 90.06) * mm, "radius": 0.4 * mm});
            skCircle(sketch, "E32.1.0.207", {"center": v(92.2, 46.82) * mm, "radius": 0.4 * mm});
            skCircle(sketch, "E32.1.0.208", {"center": v(92.2, 11.73) * mm, "radius": 0.4 * mm});
            skCircle(sketch, "E32.1.0.209", {"center": v(112.71, 40.6) * mm, "radius": 0.4 * mm});
            skCircle(sketch, "E32.1.0.210", {"center": v(102.46, 84.71) * mm, "radius": 0.4 * mm});
            skCircle(sketch, "E32.1.0.211", {"center": v(102.46, 49.62) * mm, "radius": 0.4 * mm});
            skCircle(sketch, "E32.1.0.212", {"center": v(112.71, 78.1) * mm, "radius": 0.4 * mm});
            skCircle(sketch, "E32.1.0.213", {"center": v(71.7, 84.71) * mm, "radius": 0.4 * mm});
            skCircle(sketch, "E32.1.0.214", {"center": v(71.7, 66.53) * mm, "radius": 0.4 * mm});
            skCircle(sketch, "E32.1.0.215", {"center": v(71.7, 49.62) * mm, "radius": 0.4 * mm});
            skCircle(sketch, "E32.1.0.216", {"center": v(71.7, 13) * mm, "radius": 0.4 * mm});
            skCircle(sketch, "E32.1.0.217", {"center": v(71.7, 35.25) * mm, "radius": 0.4 * mm});
            skLineSegment(sketch, "E32.1.0.218", {"start": v(112.71, 10.46) * mm, "end": v(112.71, 15.8) * mm, "construction": true});
            skCircle(sketch, "E32.1.0.219", {"center": v(92.2, 28.64) * mm, "radius": 0.4 * mm});
            skCircle(sketch, "E32.1.0.220", {"center": v(92.2, 10.46) * mm, "radius": 0.4 * mm});
            skCircle(sketch, "E32.1.0.221", {"center": v(81.95, 88.79) * mm, "radius": 0.4 * mm});
            skCircle(sketch, "E32.1.0.222", {"center": v(81.95, 78.1) * mm, "radius": 0.4 * mm});
            skCircle(sketch, "E32.1.0.223", {"center": v(81.95, 57.5) * mm, "radius": 0.4 * mm});
            skCircle(sketch, "E32.1.0.224", {"center": v(81.95, 71.88) * mm, "radius": 0.4 * mm});
            skCircle(sketch, "E32.1.0.225", {"center": v(81.95, 17.07) * mm, "radius": 0.4 * mm});
            skCircle(sketch, "E32.1.0.226", {"center": v(102.46, 66.53) * mm, "radius": 0.4 * mm});
            skCircle(sketch, "E32.1.0.227", {"center": v(102.46, 52.16) * mm, "radius": 0.4 * mm});
            skCircle(sketch, "E32.1.0.228", {"center": v(102.46, 22.42) * mm, "radius": 0.4 * mm});
            skCircle(sketch, "E32.1.0.229", {"center": v(92.2, 80.64) * mm, "radius": 0.4 * mm});
            skCircle(sketch, "E32.1.0.230", {"center": v(92.2, 45.55) * mm, "radius": 0.4 * mm});
            skCircle(sketch, "E32.1.0.231", {"center": v(92.2, 63.73) * mm, "radius": 0.4 * mm});
            skCircle(sketch, "E32.1.0.232", {"center": v(112.71, 88.79) * mm, "radius": 0.4 * mm});
            skCircle(sketch, "E32.1.0.233", {"center": v(112.71, 57.5) * mm, "radius": 0.4 * mm});
            skCircle(sketch, "E32.1.0.234", {"center": v(102.46, 83.44) * mm, "radius": 0.4 * mm});
            skCircle(sketch, "E32.1.0.235", {"center": v(112.71, 17.07) * mm, "radius": 0.4 * mm});
            skCircle(sketch, "E32.1.0.236", {"center": v(71.7, 17.07) * mm, "radius": 0.4 * mm});
            skCircle(sketch, "E32.1.0.237", {"center": v(112.71, 32.71) * mm, "radius": 0.4 * mm});
            skCircle(sketch, "E32.1.0.238", {"center": v(112.71, 50.9) * mm, "radius": 0.4 * mm});
            skCircle(sketch, "E32.1.0.239", {"center": v(81.95, 10.46) * mm, "radius": 0.4 * mm});
            skCircle(sketch, "E32.1.0.240", {"center": v(102.46, 17.07) * mm, "radius": 0.4 * mm});
            skCircle(sketch, "E32.1.0.241", {"center": v(112.71, 49.62) * mm, "radius": 0.4 * mm});
            skCircle(sketch, "E32.1.0.242", {"center": v(112.71, 84.71) * mm, "radius": 0.4 * mm});
            skCircle(sketch, "E32.1.0.243", {"center": v(102.46, 15.8) * mm, "radius": 0.4 * mm});
            skCircle(sketch, "E32.1.0.244", {"center": v(71.7, 15.8) * mm, "radius": 0.4 * mm});
            skCircle(sketch, "E32.1.0.245", {"center": v(81.95, 11.73) * mm, "radius": 0.4 * mm});
            skCircle(sketch, "E32.1.0.246", {"center": v(71.7, 28.64) * mm, "radius": 0.4 * mm});
            skCircle(sketch, "E32.1.0.247", {"center": v(112.71, 83.44) * mm, "radius": 0.4 * mm});
            skLineSegment(sketch, "E32.1.0.248", {"start": v(71.7, 10.46) * mm, "end": v(71.7, 15.8) * mm, "construction": true});
            skCircle(sketch, "E32.1.0.249", {"center": v(71.7, 27.37) * mm, "radius": 0.4 * mm});
            skCircle(sketch, "E32.1.0.250", {"center": v(112.71, 33.98) * mm, "radius": 0.4 * mm});
            skCircle(sketch, "E32.1.0.251", {"center": v(71.7, 11.73) * mm, "radius": 0.4 * mm});
            skCircle(sketch, "E32.1.0.252", {"center": v(71.7, 10.46) * mm, "radius": 0.4 * mm});
            skLineSegment(sketch, "E32.direction1", {"start": v(10.8, 10.46) * mm, "end": v(71.7, 10.46) * mm, "construction": true});
            skSolve(sketch);
        }
        {
            var Q0;
            Q0 = qSketchRegion(id + "F4", true);
            extrude(context, id + "F5", {"entities" : qUnion([Q0]), "operationType" : NewBodyOperationType.REMOVE, "oppositeDirection" : true, "depth" : 2 * mm, "offsetDistance" : 25 * mm});
        }
    });
